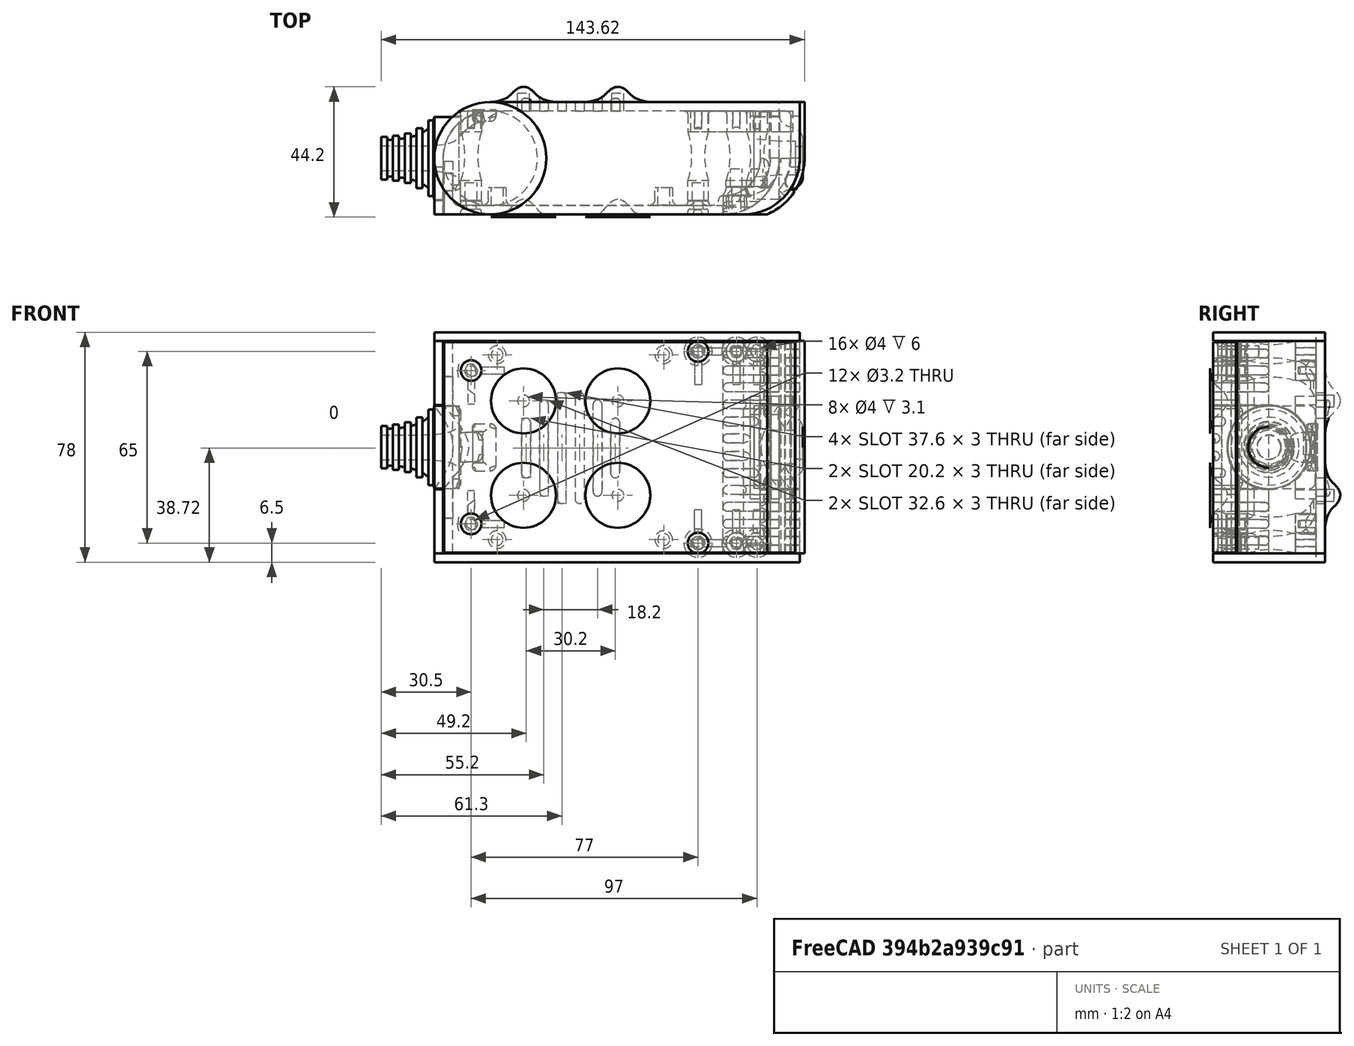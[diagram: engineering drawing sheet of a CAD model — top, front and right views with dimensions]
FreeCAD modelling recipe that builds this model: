
FCSTD DOCUMENT  (FreeCAD 0.19R0.19.2)
Label: enclosure_150
License: All rights reserved
LicenseURL: http://en.wikipedia.org/wiki/All_rights_reserved
objects: Part::Feature×96, Part::Revolution×96, Part::MultiFuse×79, Sketcher::SketchObject×53, Part::Extrusion×41, Part::Cut×39, Part::Fillet×37, Part::Cylinder×36, Part::Box×23, App::MeasureDistance×4
note: 500 computed .brp shape members not serialized (recipe doc carries the construction recipe); baked Part::Feature solids carry a one-line shape summary decoded from their .brp

FEATURE [Sketcher::SketchObject] Sketch  label="topSketch"
  FullyConstrained = true
  sketch-geometry (20):
    g0: LineSegment StartX=5.21097e-06 StartY=3 StartZ=0 EndX=5.21097e-06 EndY=19 EndZ=0
    g1: ArcOfCircle CenterX=19 CenterY=19 CenterZ=0 NormalX=0 NormalY=0 NormalZ=1 AngleXU=0 Radius=19 StartAngle=1.5708 EndAngle=3.14159
    g2: ArcOfCircle CenterX=19 CenterY=19 CenterZ=0 NormalX=0 NormalY=0 NormalZ=1 AngleXU=0 Radius=16 StartAngle=1.5708 EndAngle=3.14159
    g3: LineSegment StartX=114 StartY=35 StartZ=0 EndX=19 EndY=35 EndZ=0
    g4: LineSegment StartX=5.21097e-06 StartY=3 StartZ=0 EndX=5.21097e-06 EndY=0 EndZ=0
    g5: LineSegment StartX=3 StartY=0 StartZ=0 EndX=5.21097e-06 EndY=0 EndZ=0
    g6: LineSegment StartX=3 StartY=19 StartZ=0 EndX=3 EndY=0 EndZ=0
    g7: LineSegment StartX=19 StartY=38 StartZ=0 EndX=124 EndY=38 EndZ=0
    g8: Circle CenterX=119 CenterY=35 CenterZ=0 NormalX=0 NormalY=0 NormalZ=1 AngleXU=0 Radius=1
    g9: Circle CenterX=121 CenterY=35 CenterZ=0 NormalX=0 NormalY=0 NormalZ=1 AngleXU=0 Radius=1
    g10: Circle CenterX=121 CenterY=33 CenterZ=0 NormalX=0 NormalY=0 NormalZ=1 AngleXU=0 Radius=1
    g11: BSplineCurve PolesCount=3 KnotsCount=2 Degree=2 IsPeriodic=0
    g12: GeomPoint X=119 Y=35 Z=0
    g13: GeomPoint X=121 Y=33 Z=0
    g14: LineSegment StartX=119 StartY=35 StartZ=0 EndX=114 EndY=35 EndZ=0
    g15: ArcOfCircle CenterX=105 CenterY=19 CenterZ=0 NormalX=0 NormalY=0 NormalZ=1 AngleXU=0 Radius=19 StartAngle=5.7297 EndAngle=6.28319
    g16: ArcOfCircle CenterX=105 CenterY=19 CenterZ=0 NormalX=0 NormalY=0 NormalZ=1 AngleXU=0 Radius=16 StartAngle=5.60905 EndAngle=6.28319
    g17: LineSegment StartX=121 StartY=33 StartZ=0 EndX=121 EndY=19 EndZ=0
    g18: LineSegment StartX=124 StartY=38 StartZ=0 EndX=124 EndY=19 EndZ=0
    g19: LineSegment StartX=117.5 StartY=9.01251 StartZ=0 EndX=121.163 EndY=9.0125 EndZ=0
  constraints (46):
    c: Vertical(g0)
    c: Block(g0)
    c: Coincident(g1,g0)
    c: Block(g1)
    c: Coincident(g2,g1)
    c: Block(g2)
    c: Coincident(g3,g2)
    c: Horizontal(g3)
    c: Tangent(g3,g2)
    c: Coincident(g4,g0)
    c: Distance(g4) = 3
    c: Vertical(g4)
    c: Coincident(g5,g4)
    c: Horizontal(g5)
    c: Coincident(g6,g2)
    c: Coincident(g6,g5)
    c: Vertical(g6)
    c: Horizontal(g7)
    c: Distance(g7) = 105
    c: Coincident(g7,g1)
    c: Block(g3)
    c: Weight(g8) = 1
    c: Equal(g8,g9)
    c: Equal(g8,g10)
    c: InternalAlignment(g8,g11)
    c: InternalAlignment(g9,g11)
    c: InternalAlignment(g10,g11)
    c: InternalAlignment(g12,g11)
    c: InternalAlignment(g13,g11)
    c: Block(g11)
    c: Coincident(g14,g11)
    c: Coincident(g14,g3)
    c: Horizontal(g14)
    c: Block(g15)
    c: Coincident(g16,g15)
    c: Block(g16)
    c: Coincident(g17,g11)
    c: Coincident(g17,g16)
    c: Vertical(g17)
    c: Distance(g17) = 14
    c: Coincident(g18,g7)
    c: Coincident(g18,g15)
    c: Vertical(g18)
    c: Distance(g18) = 19
    c: Coincident(g19,g16)
    c: Coincident(g19,g15)
FEATURE [Sketcher::SketchObject] Sketch001  label="bottomSketch"
  FullyConstrained = true
  sketch-geometry (32):
    g0: LineSegment StartX=3.3 StartY=-6.03275e-07 StartZ=0 EndX=98 EndY=-6.03275e-07 EndZ=0
    g1: ArcOfCircle CenterX=98 CenterY=19 CenterZ=0 NormalX=0 NormalY=0 NormalZ=1 AngleXU=0 Radius=19 StartAngle=4.71239 EndAngle=5.71103
    g2: LineSegment StartX=6.3 StartY=8 StartZ=0 EndX=3.3 EndY=8 EndZ=0
    g3: LineSegment StartX=3.3 StartY=8 StartZ=0 EndX=3.3 EndY=-6.03275e-07 EndZ=0
    g4: ArcOfCircle CenterX=8.3 CenterY=5 CenterZ=0 NormalX=0 NormalY=0 NormalZ=1 AngleXU=0 Radius=2 StartAngle=3.14159 EndAngle=4.71239
    g5: LineSegment StartX=6.3 StartY=8 StartZ=0 EndX=6.3 EndY=5 EndZ=0
    g6: ArcOfCircle CenterX=98 CenterY=19 CenterZ=0 NormalX=0 NormalY=0 NormalZ=1 AngleXU=0 Radius=12.7 StartAngle=4.71239 EndAngle=6.28319
    g7: LineSegment StartX=94.7 StartY=3 StartZ=0 EndX=8.3 EndY=3 EndZ=0
    g8-g12: Circle x5 (B-spline internal-alignment scaffolding for g13; pole/knot coordinates omitted)
    g13: BSplineCurve PolesCount=5 KnotsCount=3 Degree=3 IsPeriodic=0
    g14: GeomPoint X=98 Y=6.3 Z=0
    g15: GeomPoint X=96.3938 Y=4.71946 Z=0
    g16: GeomPoint X=94.7 Y=3 Z=0
    g17-g23: Circle x7 (B-spline internal-alignment scaffolding for g24; pole/knot coordinates omitted)
    g24: BSplineCurve PolesCount=7 KnotsCount=5 Degree=3 IsPeriodic=0
    g25-g29: GeomPoint x5 (B-spline internal-alignment scaffolding for g24; pole/knot coordinates omitted)
    g30: ArcOfCircle CenterX=98 CenterY=19 CenterZ=0 NormalX=0 NormalY=0 NormalZ=1 AngleXU=0 Radius=15.7 StartAngle=5.81226 EndAngle=6.28319
    g31: LineSegment StartX=110.7 StartY=19 StartZ=0 EndX=113.7 EndY=19 EndZ=0
  constraints (41):
    c: Horizontal(g0)
    c: Coincident(g1,g0)
    c: Block(g1)
    c: Horizontal(g2)
    c: Distance(g2) = 3
    c: Coincident(g3,g2)
    c: Vertical(g3)
    c: Coincident(g3,g0)
    c: Block(g4)
    c: Block(g2)
    c: Coincident(g5,g2)
    c: Coincident(g5,g4)
    c: Vertical(g5)
    c: Coincident(g6,g1)
    c: Block(g6)
    c: Coincident(g7,g4)
    c: Horizontal(g7)
    c: Block(g0)
    c: Block(g7)
    c: Block(g3)
    c: Coincident(g13,g6)
    c: Weight(g8) = 1
    c: Equal(g8, g9-g12) x4
    c: Coincident(g13,g7)
    c: InternalAlignment(g8-g12 -> g13) x5
    c: InternalAlignment(g14,g13)
    c: InternalAlignment(g15,g13)
    c: InternalAlignment(g16,g13)
    c: Block(g13)
    c: Weight(g17) = 1
    c: Equal(g17, g18-g23) x6
    c: Coincident(g24,g1)
    c: InternalAlignment(g17-g23 -> g24) x7
    c: InternalAlignment(g25-g29 -> g24) x5
    c: Block(g24)
    c: Coincident(g30,g24)
    c: Coincident(g31,g6)
    c: Coincident(g31,g30)
    c: Horizontal(g31)
    c: Block(g31)
    c: Block(g30)
FEATURE [Part::Extrusion] Extrude  label="top"
  Base = -> Sketch
  Dir = (0,0,1)
  DirMode = 2
  FaceMakerClass = Part::FaceMakerBullseye
  LengthFwd = 72
  LengthRev = 0
  Solid = true
  Symmetric = false
FEATURE [Part::Extrusion] Extrude001  label="bottom"
  Base = -> Sketch001
  Dir = (0,0,1)
  DirMode = 2
  FaceMakerClass = Part::FaceMakerBullseye
  LengthFwd = 71.4
  LengthRev = 0
  Placement = pos=(0,0,0.3) rot=(0,0,1;0rad)
  Solid = true
  Symmetric = false
FEATURE [Sketcher::SketchObject] Sketch002  label="topSketch001"
  FullyConstrained = true
  sketch-geometry (6):
    g0: ArcOfCircle CenterX=19 CenterY=19 CenterZ=0 NormalX=0 NormalY=0 NormalZ=1 AngleXU=0 Radius=19 StartAngle=1.5708 EndAngle=3.14159
    g1: LineSegment StartX=5.22862e-06 StartY=19 StartZ=0 EndX=5.22862e-06 EndY=1.19904e-11 EndZ=0
    g2: LineSegment StartX=19 StartY=38 StartZ=0 EndX=124 EndY=38 EndZ=0
    g3: LineSegment StartX=5.22862e-06 StartY=1.19904e-11 StartZ=0 EndX=105 EndY=1.19904e-11 EndZ=0
    g4: ArcOfCircle CenterX=105 CenterY=19 CenterZ=0 NormalX=0 NormalY=0 NormalZ=1 AngleXU=0 Radius=19 StartAngle=4.71239 EndAngle=6.28319
    g5: LineSegment StartX=124 StartY=38 StartZ=0 EndX=124 EndY=19 EndZ=0
  constraints (16):
    c: Block(g0)
    c: Coincident(g1,g0)
    c: Vertical(g1)
    c: Horizontal(g2)
    c: Distance(g2) = 105
    c: Coincident(g2,g0)
    c: Distance(g1) = 19
    c: Coincident(g3,g1)
    c: Horizontal(g3)
    c: Distance(g3) = 105
    c: Block(g4)
    c: Coincident(g4,g3)
    c: Coincident(g5,g2)
    c: Coincident(g5,g4)
    c: Vertical(g5)
    c: Distance(g5) = 19
FEATURE [Part::Extrusion] Extrude002  label="sideA"
  Base = -> Sketch002
  Dir = (0,0,1)
  DirMode = 2
  FaceMakerClass = Part::FaceMakerBullseye
  LengthFwd = 3
  LengthRev = 0
  Placement = pos=(0,0,-3) rot=(0,0,1;0rad)
  Solid = true
  Symmetric = false
FEATURE [Sketcher::SketchObject] Sketch003  label="topSketch002"
  FullyConstrained = true
  sketch-geometry (6):
    g0: LineSegment StartX=19 StartY=38 StartZ=0 EndX=117 EndY=38 EndZ=0
    g1: ArcOfCircle CenterX=19 CenterY=19 CenterZ=0 NormalX=0 NormalY=0 NormalZ=1 AngleXU=0 Radius=19 StartAngle=1.5708 EndAngle=3.14159
    g2: LineSegment StartX=117 StartY=38 StartZ=0 EndX=117 EndY=19 EndZ=0
    g3: LineSegment StartX=98 StartY=1.0161e-12 StartZ=0 EndX=5.22862e-06 EndY=1.0161e-12 EndZ=0
    g4: LineSegment StartX=5.22862e-06 StartY=19 StartZ=0 EndX=5.22862e-06 EndY=1.0161e-12 EndZ=0
    g5: ArcOfCircle CenterX=98 CenterY=19 CenterZ=0 NormalX=0 NormalY=0 NormalZ=1 AngleXU=0 Radius=19 StartAngle=4.71239 EndAngle=6.28319
  constraints (16):
    c: Horizontal(g0)
    c: Distance(g0) = 98
    c: Coincident(g1,g0)
    c: Block(g1)
    c: Coincident(g2,g0)
    c: Vertical(g2)
    c: Distance(g2) = 19
    c: Horizontal(g3)
    c: Coincident(g4,g1)
    c: Vertical(g4)
    c: Coincident(g3,g4)
    c: Block(g3)
    c: Coincident(g5,g2)
    c: Coincident(g5,g3)
    c: Block(g0)
    c: Block(g5)
FEATURE [Sketcher::SketchObject] Sketch004
  FullyConstrained = true
  MapMode = 3
  Placement = pos=(0,0,0) rot=(1,0,0;1.5708rad)
  Support = -> [Extrude]
  sketch-geometry (8):
    g0: Circle CenterX=80.351 CenterY=-67.6202 CenterZ=0 NormalX=0 NormalY=0 NormalZ=1 AngleXU=0 Radius=2
    g1: Circle CenterX=80.351 CenterY=-67.6202 CenterZ=0 NormalX=0 NormalY=0 NormalZ=1 AngleXU=0 Radius=3
    g2: Circle CenterX=80.351 CenterY=-4.92017 CenterZ=0 NormalX=0 NormalY=0 NormalZ=1 AngleXU=0 Radius=2
    g3: Circle CenterX=80.351 CenterY=-4.92017 CenterZ=0 NormalX=0 NormalY=0 NormalZ=1 AngleXU=0 Radius=3
    g4: Circle CenterX=23.851 CenterY=-4.92017 CenterZ=0 NormalX=0 NormalY=0 NormalZ=1 AngleXU=0 Radius=2
    g5: Circle CenterX=23.851 CenterY=-4.92017 CenterZ=0 NormalX=0 NormalY=0 NormalZ=1 AngleXU=0 Radius=3
    g6: Circle CenterX=23.851 CenterY=-67.6202 CenterZ=0 NormalX=0 NormalY=0 NormalZ=1 AngleXU=0 Radius=2
    g7: Circle CenterX=23.851 CenterY=-67.6202 CenterZ=0 NormalX=0 NormalY=0 NormalZ=1 AngleXU=0 Radius=3
  constraints (8):
    c: Block(g3)
    c: Block(g2)
    c: Block(g1)
    c: Block(g0)
    c: Block(g6)
    c: Block(g7)
    c: Block(g4)
    c: Block(g5)
FEATURE [Part::Extrusion] Extrude004
  Base = -> Sketch004
  Dir = (0,-1,2e-16)
  DirMode = 2
  FaceMakerClass = Part::FaceMakerBullseye
  LengthFwd = 6
  LengthRev = 0
  Placement = pos=(0,9,0) rot=(0,0,1;0rad)
  Solid = true
  Symmetric = false
FEATURE [Sketcher::SketchObject] Sketch005
  FullyConstrained = true
  MapMode = 3
  Placement = pos=(0,0,0) rot=(1,0,0;1.5708rad)
  Support = -> [Extrude]
  sketch-geometry (8):
    g0: Circle CenterX=80.351 CenterY=-67.6202 CenterZ=0 NormalX=0 NormalY=0 NormalZ=1 AngleXU=0 Radius=3
    g1: Circle CenterX=80.351 CenterY=-4.92017 CenterZ=0 NormalX=0 NormalY=0 NormalZ=1 AngleXU=0 Radius=3
    g2: Circle CenterX=23.851 CenterY=-4.92017 CenterZ=0 NormalX=0 NormalY=0 NormalZ=1 AngleXU=0 Radius=3
    g3: Circle CenterX=23.851 CenterY=-67.6202 CenterZ=0 NormalX=0 NormalY=0 NormalZ=1 AngleXU=0 Radius=3
    g4: Circle CenterX=23.851 CenterY=-67.6202 CenterZ=0 NormalX=0 NormalY=0 NormalZ=1 AngleXU=0 Radius=5
    g5: Circle CenterX=80.351 CenterY=-67.6202 CenterZ=0 NormalX=0 NormalY=0 NormalZ=1 AngleXU=0 Radius=5
    g6: Circle CenterX=23.851 CenterY=-4.92017 CenterZ=0 NormalX=0 NormalY=0 NormalZ=1 AngleXU=0 Radius=5
    g7: Circle CenterX=80.351 CenterY=-4.92017 CenterZ=0 NormalX=0 NormalY=0 NormalZ=1 AngleXU=0 Radius=5
  constraints (8):
    c: Block(g1)
    c: Block(g0)
    c: Block(g3)
    c: Block(g2)
    c: Block(g5)
    c: Block(g4)
    c: Block(g6)
    c: Block(g7)
FEATURE [Part::Extrusion] Extrude005
  Base = -> Sketch005
  Dir = (0,-1,2e-16)
  DirMode = 2
  FaceMakerClass = Part::FaceMakerBullseye
  LengthFwd = 2
  LengthRev = 0
  Solid = true
  Symmetric = false
FEATURE [Sketcher::SketchObject] Sketch006
  FullyConstrained = true
  MapMode = 3
  Placement = pos=(0,0,0) rot=(1,0,0;1.5708rad)
  sketch-geometry (8):
    g0: Circle CenterX=80.351 CenterY=-67.6202 CenterZ=0 NormalX=0 NormalY=0 NormalZ=1 AngleXU=0 Radius=3
    g1: Circle CenterX=80.351 CenterY=-4.92017 CenterZ=0 NormalX=0 NormalY=0 NormalZ=1 AngleXU=0 Radius=3
    g2: Circle CenterX=23.851 CenterY=-4.92017 CenterZ=0 NormalX=0 NormalY=0 NormalZ=1 AngleXU=0 Radius=3
    g3: Circle CenterX=23.851 CenterY=-67.6202 CenterZ=0 NormalX=0 NormalY=0 NormalZ=1 AngleXU=0 Radius=3
    g4: Circle CenterX=23.851 CenterY=-67.6202 CenterZ=0 NormalX=0 NormalY=0 NormalZ=1 AngleXU=0 Radius=5
    g5: Circle CenterX=80.351 CenterY=-67.6202 CenterZ=0 NormalX=0 NormalY=0 NormalZ=1 AngleXU=0 Radius=5
    g6: Circle CenterX=23.851 CenterY=-4.92017 CenterZ=0 NormalX=0 NormalY=0 NormalZ=1 AngleXU=0 Radius=5
    g7: Circle CenterX=80.351 CenterY=-4.92017 CenterZ=0 NormalX=0 NormalY=0 NormalZ=1 AngleXU=0 Radius=5
  constraints (8):
    c: Block(g1)
    c: Block(g0)
    c: Block(g3)
    c: Block(g2)
    c: Block(g5)
    c: Block(g4)
    c: Block(g6)
    c: Block(g7)
FEATURE [Part::Extrusion] Extrude007
  Base = -> Sketch006
  Dir = (0,-1,2e-16)
  DirMode = 2
  FaceMakerClass = Part::FaceMakerBullseye
  LengthFwd = 2
  LengthRev = 0
  Solid = true
  Symmetric = false
FEATURE [Part::Fillet] Fillet
  Base = -> Extrude007
  Edges = 4 edges r=1.99: [Edge6,Edge12,Edge18,Edge24]
FEATURE [Part::Cut] Cut
  Base = -> Extrude005
  Placement = pos=(0,5,0) rot=(0,0,1;0rad)
  Tool = -> Fillet
FEATURE [Part::MultiFuse] Fusion  label="pCBScrews"
  Placement = pos=(-2.5,0,72.3) rot=(0,0,1;0rad)
  Shapes = -> [Extrude004,Cut]
FEATURE [App::MeasureDistance] Distance  label="Distance: 0.69 mm"
  Distance = 0.685967
  P1 = (24.0138,2.9647,0.3)
  P2 = (23.8901,3,-0.373787)
FEATURE [App::MeasureDistance] Distance001  label="Distance: 0.53 mm"
  Distance = 0.533607
  P1 = (80.2939,3,72.2334)
  P2 = (80.281,2.99661,71.7)
FEATURE [Part::Fillet] Fillet001
  Base = -> Extrude001
  Edges = 1 edges r=2.4: [Edge17]
FEATURE [Part::Fillet] Fillet002  label="bottom001"
  Base = -> Fillet001
  Edges = 1 edges r=2.4: [Edge36]
FEATURE [Part::Fillet] Fillet003  label="top001"
  Base = -> Extrude
  Edges = 1 edges r=2: [Edge1]
FEATURE [Sketcher::SketchObject] Sketch007
  FullyConstrained = true
  sketch-geometry (16):
    g0: LineSegment StartX=4 StartY=0 StartZ=0 EndX=4 EndY=2.4 EndZ=0
    g1: LineSegment StartX=4 StartY=2.4 StartZ=0 EndX=7 EndY=2.4 EndZ=0
    g2: LineSegment StartX=4 StartY=0 StartZ=0 EndX=5.7 EndY=0 EndZ=0
    g3: LineSegment StartX=5.7 StartY=0 StartZ=0 EndX=5.7 EndY=-5.6 EndZ=0
    g4-g8: Circle x5 (B-spline internal-alignment scaffolding for g9; pole/knot coordinates omitted)
    g9: BSplineCurve PolesCount=5 KnotsCount=3 Degree=3 IsPeriodic=0
    g10: GeomPoint X=7 Y=2.4 Z=0
    g11: GeomPoint X=10.4582 Y=-1.55472 Z=0
    g12: GeomPoint X=14 Y=-5.6 Z=0
    g13: LineSegment StartX=14 StartY=-5.6 StartZ=0 EndX=14 EndY=-14.1 EndZ=0
    g14: LineSegment StartX=14 StartY=-14.1 StartZ=0 EndX=6.5 EndY=-14.1 EndZ=0
    g15: LineSegment StartX=5.7 StartY=-5.6 StartZ=0 EndX=6.5 EndY=-14.1 EndZ=0
  constraints (28):
    c: Distance(g0) = 2.4
    c: Vertical(g0)
    c: Block(g0)
    c: Coincident(g1,g0)
    c: Horizontal(g1)
    c: Distance(g1) = 3
    c: Coincident(g2,g0)
    c: Horizontal(g2)
    c: Distance(g2) = 1.7
    c: Coincident(g3,g2)
    c: Vertical(g3)
    c: Distance(g3) = 5.6
    c: Coincident(g9,g1)
    c: Weight(g4) = 1
    c: Equal(g4, g5-g8) x4
    c: InternalAlignment(g4-g8 -> g9) x5
    c: InternalAlignment(g10,g9)
    c: InternalAlignment(g11,g9)
    c: InternalAlignment(g12,g9)
    c: Block(g9)
    c: Coincident(g13,g9)
    c: Vertical(g13)
    c: Distance(g13) = 8.5
    c: Coincident(g14,g13)
    c: Horizontal(g14)
    c: Distance(g14) = 7.5
    c: Coincident(g15,g3)
    c: Coincident(g15,g14)
FEATURE [Part::Feature] Face
  shape: bbox 10 x 16.5 x 2e-07 mm, 1 faces, 0 solids (baked)
FEATURE [Part::Revolution] Revolve  label="plugHousing"
  Angle = 360
  Axis = (0,1,0)
  Base = (0,0,0)
  FaceMakerClass = Part::FaceMakerBullseye
  Placement = pos=(0,0,36.15) rot=(0,0,1;0rad)
  Solid = false
  Source = -> Face
  Symmetric = false
FEATURE [Part::Feature] Face001
  shape: bbox 10 x 16.5 x 2e-07 mm, 1 faces, 0 solids (baked)
FEATURE [Part::Revolution] Revolve001  label="plugHousing001"
  Angle = 360
  Axis = (0,1,0)
  Base = (0,0,0)
  FaceMakerClass = Part::FaceMakerBullseye
  Placement = pos=(0,0,36.15) rot=(0,0,1;0rad)
  Solid = false
  Source = -> Face001
  Symmetric = false
FEATURE [Part::MultiFuse] Fusion001  label="plugHousing002"
  Placement = pos=(0,0,0) rot=(0,0,1;1.5708rad)
  Shapes = -> [Revolve001,Revolve]
FEATURE [Part::Feature] Face002
  shape: bbox 10 x 16.5 x 2e-07 mm, 1 faces, 0 solids (baked)
FEATURE [Part::Revolution] Revolve003  label="plugHousing005"
  Angle = 360
  Axis = (0,1,0)
  Base = (0,0,0)
  FaceMakerClass = Part::FaceMakerBullseye
  Placement = pos=(0,0,36.15) rot=(0,0,1;0rad)
  Solid = false
  Source = -> Face002
  Symmetric = false
FEATURE [Part::Feature] Face003
  shape: bbox 10 x 16.5 x 2e-07 mm, 1 faces, 0 solids (baked)
FEATURE [Part::Revolution] Revolve002  label="plugHousing003"
  Angle = 360
  Axis = (0,1,0)
  Base = (0,0,0)
  FaceMakerClass = Part::FaceMakerBullseye
  Placement = pos=(0,0,36.15) rot=(0,0,1;0rad)
  Solid = false
  Source = -> Face003
  Symmetric = false
FEATURE [Part::MultiFuse] Fusion002  label="plugHousing004"
  Placement = pos=(0,0,0) rot=(0,0,1;1.5708rad)
  Shapes = -> [Revolve002,Revolve003]
FEATURE [Part::MultiFuse] Fusion003  label="plugHousing006"
  Placement = pos=(0,19,0) rot=(0,0,1;3.14159rad)
  Shapes = -> [Fusion002,Fusion001]
FEATURE [Part::Feature] Face004
  shape: bbox 10 x 16.5 x 2e-07 mm, 1 faces, 0 solids (baked)
FEATURE [Part::Revolution] Revolve006  label="plugHousing010"
  Angle = 360
  Axis = (0,1,0)
  Base = (0,0,0)
  FaceMakerClass = Part::FaceMakerBullseye
  Placement = pos=(0,0,36.15) rot=(0,0,1;0rad)
  Solid = false
  Source = -> Face004
  Symmetric = false
FEATURE [Part::Feature] Face005
  shape: bbox 10 x 16.5 x 2e-07 mm, 1 faces, 0 solids (baked)
FEATURE [Part::Revolution] Revolve007  label="plugHousing011"
  Angle = 360
  Axis = (0,1,0)
  Base = (0,0,0)
  FaceMakerClass = Part::FaceMakerBullseye
  Placement = pos=(0,0,36.15) rot=(0,0,1;0rad)
  Solid = false
  Source = -> Face005
  Symmetric = false
FEATURE [Part::Feature] Face006
  shape: bbox 10 x 16.5 x 2e-07 mm, 1 faces, 0 solids (baked)
FEATURE [Part::Revolution] Revolve004  label="plugHousing007"
  Angle = 360
  Axis = (0,1,0)
  Base = (0,0,0)
  FaceMakerClass = Part::FaceMakerBullseye
  Placement = pos=(0,0,36.15) rot=(0,0,1;0rad)
  Solid = false
  Source = -> Face006
  Symmetric = false
FEATURE [Part::MultiFuse] Fusion004  label="plugHousing009"
  Placement = pos=(0,0,0) rot=(0,0,1;1.5708rad)
  Shapes = -> [Revolve004,Revolve007]
FEATURE [Part::Feature] Face007
  shape: bbox 10 x 16.5 x 2e-07 mm, 1 faces, 0 solids (baked)
FEATURE [Part::Revolution] Revolve005  label="plugHousing008"
  Angle = 360
  Axis = (0,1,0)
  Base = (0,0,0)
  FaceMakerClass = Part::FaceMakerBullseye
  Placement = pos=(0,0,36.15) rot=(0,0,1;0rad)
  Solid = false
  Source = -> Face007
  Symmetric = false
FEATURE [Part::MultiFuse] Fusion005  label="plugHousing012"
  Placement = pos=(0,0,0) rot=(0,0,1;1.5708rad)
  Shapes = -> [Revolve006,Revolve005]
FEATURE [Part::MultiFuse] Fusion006  label="plugHousing013"
  Placement = pos=(0,19,0) rot=(0,0,1;3.14159rad)
  Shapes = -> [Fusion005,Fusion004]
FEATURE [Part::MultiFuse] Fusion007  label="plugHousing014"
  Placement = pos=(122.621,0,-0.15) rot=(0,0,1;0rad)
  Shapes = -> [Fusion003,Fusion006]
FEATURE [Part::Cylinder] Cylinder002
  Angle = 360
  AttacherType = Attacher::AttachEngine3D
  Height = 20
  Placement = pos=(0,0,36.15) rot=(0,0,1;0rad)
  Radius = 4
FEATURE [Part::Cylinder] Cylinder003
  Angle = 360
  AttacherType = Attacher::AttachEngine3D
  Height = 10
  Placement = pos=(0,0,36.15) rot=(0,0,1;0rad)
  Radius = 4
FEATURE [Part::MultiFuse] Fusion009  label="removeToCreateHoleForPlugHousing"
  Placement = pos=(70,19,36.15) rot=(0,1,0;1.5708rad)
  Shapes = -> [Cylinder002,Cylinder003]
FEATURE [Part::Cylinder] Cylinder004
  Angle = 360
  AttacherType = Attacher::AttachEngine3D
  Height = 20
  Placement = pos=(0,0,36.15) rot=(0,0,1;0rad)
  Radius = 4
FEATURE [Part::Cylinder] Cylinder005
  Angle = 360
  AttacherType = Attacher::AttachEngine3D
  Height = 10
  Placement = pos=(0,0,36.15) rot=(0,0,1;0rad)
  Radius = 4
FEATURE [Part::MultiFuse] Fusion010  label="removeToCreateHoleForPlugHousing001"
  Placement = pos=(70,19,36.15) rot=(0,1,0;1.5708rad)
  Shapes = -> [Cylinder004,Cylinder005]
FEATURE [Part::Cut] Cut001
  Base = -> Fillet003
  Tool = -> Fusion010
FEATURE [Part::Cut] Cut002  label="Bottom"
  Base = -> Fillet002
  Tool = -> Fusion009
FEATURE [Part::Feature] Face008
  shape: bbox 10 x 16.5 x 2e-07 mm, 1 faces, 0 solids (baked)
FEATURE [Part::Revolution] Revolve011  label="plugHousing021"
  Angle = 360
  Axis = (0,1,0)
  Base = (0,0,0)
  FaceMakerClass = Part::FaceMakerBullseye
  Placement = pos=(0,0,36.15) rot=(0,0,1;0rad)
  Solid = false
  Source = -> Face008
  Symmetric = false
FEATURE [Part::Feature] Face009
  shape: bbox 10 x 16.5 x 2e-07 mm, 1 faces, 0 solids (baked)
FEATURE [Part::Revolution] Revolve012  label="plugHousing022"
  Angle = 360
  Axis = (0,1,0)
  Base = (0,0,0)
  FaceMakerClass = Part::FaceMakerBullseye
  Placement = pos=(0,0,36.15) rot=(0,0,1;0rad)
  Solid = false
  Source = -> Face009
  Symmetric = false
FEATURE [Part::Feature] Face010 .. Face013  x4 (patterned run collapsed; names and placements below)
  shape: bbox 10 x 16.5 x 2e-07 mm, 1 faces, 0 solids (baked)
FEATURE [Part::Revolution] Revolve015  label="plugHousing027"
  Angle = 360
  Axis = (0,1,0)
  Base = (0,0,0)
  FaceMakerClass = Part::FaceMakerBullseye
  Placement = pos=(0,0,36.15) rot=(0,0,1;0rad)
  Solid = false
  Source = -> Face013
  Symmetric = false
FEATURE [Part::Feature] Face014
  shape: bbox 10 x 16.5 x 2e-07 mm, 1 faces, 0 solids (baked)
FEATURE [Part::Feature] Face015
  shape: bbox 10 x 16.5 x 2e-07 mm, 1 faces, 0 solids (baked)
FEATURE [Part::Feature] Face016
  shape: bbox 10 x 16.5 x 2e-07 mm, 1 faces, 0 solids (baked)
FEATURE [Part::Revolution] Revolve019  label="plugHousing033"
  Angle = 360
  Axis = (0,1,0)
  Base = (0,0,0)
  FaceMakerClass = Part::FaceMakerBullseye
  Placement = pos=(0,0,36.15) rot=(0,0,1;0rad)
  Solid = false
  Source = -> Face016
  Symmetric = false
FEATURE [Part::Feature] Face017
  shape: bbox 10 x 16.5 x 2e-07 mm, 1 faces, 0 solids (baked)
FEATURE [Part::Revolution] Revolve020  label="plugHousing034"
  Angle = 360
  Axis = (0,1,0)
  Base = (0,0,0)
  FaceMakerClass = Part::FaceMakerBullseye
  Placement = pos=(0,0,36.15) rot=(0,0,1;0rad)
  Solid = false
  Source = -> Face017
  Symmetric = false
FEATURE [Part::Feature] Face018
  shape: bbox 10 x 16.5 x 2e-07 mm, 1 faces, 0 solids (baked)
FEATURE [Part::Revolution] Revolve016  label="plugHousing030"
  Angle = 360
  Axis = (0,1,0)
  Base = (0,0,0)
  FaceMakerClass = Part::FaceMakerBullseye
  Placement = pos=(0,0,36.15) rot=(0,0,1;0rad)
  Solid = false
  Source = -> Face018
  Symmetric = false
FEATURE [Part::MultiFuse] Fusion020  label="plugHousing038"
  Placement = pos=(0,0,0) rot=(0,0,1;1.5708rad)
  Shapes = -> [Revolve016,Revolve020]
FEATURE [Part::Feature] Face019
  shape: bbox 10 x 16.5 x 2e-07 mm, 1 faces, 0 solids (baked)
FEATURE [Part::Feature] Face020
  shape: bbox 10 x 16.5 x 2e-07 mm, 1 faces, 0 solids (baked)
FEATURE [Part::Revolution] Revolve017  label="plugHousing031"
  Angle = 360
  Axis = (0,1,0)
  Base = (0,0,0)
  FaceMakerClass = Part::FaceMakerBullseye
  Placement = pos=(0,0,36.15) rot=(0,0,1;0rad)
  Solid = false
  Source = -> Face020
  Symmetric = false
FEATURE [Part::MultiFuse] Fusion021  label="plugHousing039"
  Placement = pos=(0,0,0) rot=(0,0,1;1.5708rad)
  Shapes = -> [Revolve019,Revolve017]
FEATURE [Part::MultiFuse] Fusion023  label="plugHousing041"
  Placement = pos=(0,19,0) rot=(0,0,1;3.14159rad)
  Shapes = -> [Fusion021,Fusion020]
FEATURE [Part::Revolution] Revolve022  label="plugHousing043"
  Angle = 360
  Axis = (0,1,0)
  Base = (0,0,0)
  FaceMakerClass = Part::FaceMakerBullseye
  Placement = pos=(0,0,36.15) rot=(0,0,1;0rad)
  Solid = false
  Source = -> Face019
  Symmetric = false
FEATURE [Part::Feature] Face021
  shape: bbox 10 x 16.5 x 2e-07 mm, 1 faces, 0 solids (baked)
FEATURE [Part::Revolution] Revolve023  label="plugHousing044"
  Angle = 360
  Axis = (0,1,0)
  Base = (0,0,0)
  FaceMakerClass = Part::FaceMakerBullseye
  Placement = pos=(0,0,36.15) rot=(0,0,1;0rad)
  Solid = false
  Source = -> Face021
  Symmetric = false
FEATURE [Part::Feature] Face022
  shape: bbox 10 x 16.5 x 2e-07 mm, 1 faces, 0 solids (baked)
FEATURE [Part::Revolution] Revolve018  label="plugHousing032"
  Angle = 360
  Axis = (0,1,0)
  Base = (0,0,0)
  FaceMakerClass = Part::FaceMakerBullseye
  Placement = pos=(0,0,36.15) rot=(0,0,1;0rad)
  Solid = false
  Source = -> Face022
  Symmetric = false
FEATURE [Part::MultiFuse] Fusion022  label="plugHousing040"
  Placement = pos=(0,0,0) rot=(0,0,1;1.5708rad)
  Shapes = -> [Revolve018,Revolve023]
FEATURE [Part::Feature] Face023
  shape: bbox 10 x 16.5 x 2e-07 mm, 1 faces, 0 solids (baked)
FEATURE [Part::Revolution] Revolve021  label="plugHousing035"
  Angle = 360
  Axis = (0,1,0)
  Base = (0,0,0)
  FaceMakerClass = Part::FaceMakerBullseye
  Placement = pos=(0,0,36.15) rot=(0,0,1;0rad)
  Solid = false
  Source = -> Face023
  Symmetric = false
FEATURE [Part::MultiFuse] Fusion018  label="plugHousing036"
  Placement = pos=(0,0,0) rot=(0,0,1;1.5708rad)
  Shapes = -> [Revolve022,Revolve021]
FEATURE [Part::MultiFuse] Fusion019  label="plugHousing037"
  Placement = pos=(0,19,0) rot=(0,0,1;3.14159rad)
  Shapes = -> [Fusion018,Fusion022]
FEATURE [Part::MultiFuse] Fusion024  label="plugHousing042"
  Placement = pos=(122.621,0,-0.15) rot=(0,0,1;0rad)
  Shapes = -> [Fusion023,Fusion019]
FEATURE [Part::Cylinder] Cylinder006
  Angle = 360
  AttacherType = Attacher::AttachEngine3D
  Height = 20
  Placement = pos=(0,0,36.15) rot=(0,0,1;0rad)
  Radius = 14.3
FEATURE [Part::Cylinder] Cylinder007
  Angle = 360
  AttacherType = Attacher::AttachEngine3D
  Height = 10
  Placement = pos=(0,0,36.15) rot=(0,0,1;0rad)
  Radius = 4
FEATURE [Part::MultiFuse] Fusion026  label="removeToCreteHoleForPlugHousing"
  Placement = pos=(70,19,36) rot=(0,1,0;1.5708rad)
  Shapes = -> [Cylinder006,Cylinder007]
FEATURE [Part::Box] Box001  label="Cube001"
  AttacherType = Attacher::AttachEngine3D
  Height = 28
  Length = 3
  Placement = pos=(110.7,19,22) rot=(0,0,1;0rad)
  Width = 15.7
FEATURE [Part::Cut] Cut003  label="top002"
  Base = -> Cut001
  Tool = -> Fusion007
FEATURE [Part::Revolution] Revolve008  label="plugHousing015"
  Angle = 360
  Axis = (0,1,0)
  Base = (0,0,0)
  FaceMakerClass = Part::FaceMakerBullseye
  Placement = pos=(0,0,36.15) rot=(0,0,1;0rad)
  Solid = false
  Source = -> Face010
  Symmetric = false
FEATURE [Part::MultiFuse] Fusion013  label="plugHousing020"
  Placement = pos=(0,0,0) rot=(0,0,1;1.5708rad)
  Shapes = -> [Revolve008,Revolve012]
FEATURE [Part::Cut] Cut004  label="top003"
  Base = -> Cut003
  Placement = pos=(1,0,0) rot=(0,0,1;0rad)
  Tool = -> Fusion026
FEATURE [Part::Cylinder] Cylinder008
  Angle = 360
  AttacherType = Attacher::AttachEngine3D
  Height = 20
  Placement = pos=(0,0,36.15) rot=(0,0,1;0rad)
  Radius = 10.3
FEATURE [Part::Cylinder] Cylinder009
  Angle = 360
  AttacherType = Attacher::AttachEngine3D
  Height = 10
  Placement = pos=(0,0,36.15) rot=(0,0,1;0rad)
  Radius = 4
FEATURE [Part::MultiFuse] Fusion027  label="removeToCreteHoleForPlugHousing001"
  Placement = pos=(70,19,36) rot=(0,1,0;1.5708rad)
  Shapes = -> [Cylinder008,Cylinder009]
FEATURE [Part::Cut] Cut005  label="plugHousingTab"
  Base = -> Box001
  Tool = -> Fusion027
FEATURE [Part::MultiFuse] Fusion028  label="plugHousing045"
  Shapes = -> [Fusion024,Cut005]
FEATURE [Part::Box] Box002  label="Cube002"
  AttacherType = Attacher::AttachEngine3D
  Height = 28.8
  Length = 3
  Placement = pos=(107.3,28,21.6) rot=(0,0,1;0rad)
  Width = 7
FEATURE [Part::Box] Box003  label="Cube003"
  AttacherType = Attacher::AttachEngine3D
  Height = 3
  Length = 6.4
  Placement = pos=(107.3,28,18.6) rot=(0,0,1;0rad)
  Width = 7
FEATURE [Part::Box] Box004  label="Cube004"
  AttacherType = Attacher::AttachEngine3D
  Height = 3
  Length = 6.4
  Placement = pos=(107.3,28,50.4) rot=(0,0,1;0rad)
  Width = 7
FEATURE [Part::MultiFuse] Fusion029  label="plugHousingBracketHolder"
  Shapes = -> [Box004,Box002,Box003]
FEATURE [Part::Cylinder] Cylinder010
  Angle = 360
  AttacherType = Attacher::AttachEngine3D
  Height = 20
  Placement = pos=(0,0,36.15) rot=(0,0,1;0rad)
  Radius = 14.3
FEATURE [Part::Cylinder] Cylinder011
  Angle = 360
  AttacherType = Attacher::AttachEngine3D
  Height = 10
  Placement = pos=(0,0,36.15) rot=(0,0,1;0rad)
  Radius = 4
FEATURE [Part::MultiFuse] Fusion030  label="removeToCreteHoleForPlugHousing002"
  Placement = pos=(70,19,36) rot=(0,1,0;1.5708rad)
  Shapes = -> [Cylinder010,Cylinder011]
FEATURE [Part::Cut] Cut006  label="plugHousingBracketHolder001"
  Base = -> Fusion029
  Tool = -> Fusion030
FEATURE [Part::Cylinder] Cylinder012
  Angle = 360
  AttacherType = Attacher::AttachEngine3D
  Height = 20
  Placement = pos=(0,0,36.15) rot=(0,0,1;0rad)
  Radius = 7
FEATURE [Part::Cylinder] Cylinder013
  Angle = 360
  AttacherType = Attacher::AttachEngine3D
  Height = 10
  Placement = pos=(0,0,36.15) rot=(0,0,1;0rad)
  Radius = 4
FEATURE [Part::MultiFuse] Fusion032  label="removeToCreteHoleForPlugHousing003"
  Placement = pos=(70,19,36) rot=(0,1,0;1.5708rad)
  Shapes = -> [Cylinder012,Cylinder013]
FEATURE [Part::Cut] Cut007  label="bottom002"
  Base = -> Cut002
  Tool = -> Fusion032
FEATURE [Sketcher::SketchObject] Sketch008
  FullyConstrained = true
  sketch-geometry (54):
    g0: LineSegment StartX=-4.2 StartY=0 StartZ=0 EndX=-6.2 EndY=0 EndZ=0
    g1: LineSegment StartX=-14 StartY=-18 StartZ=0 EndX=-14 EndY=-26.5 EndZ=0
    g2: LineSegment StartX=-4.2 StartY=0 StartZ=0 EndX=-4.2 EndY=-13.4877 EndZ=0
    g3: Circle CenterX=-4.2 CenterY=-13.4877 CenterZ=0 NormalX=0 NormalY=0 NormalZ=1 AngleXU=0 Radius=1
    g4: Circle CenterX=-4.2 CenterY=-26.5 CenterZ=0 NormalX=0 NormalY=0 NormalZ=1 AngleXU=0 Radius=1
    g5: Circle CenterX=-8.2 CenterY=-26.5 CenterZ=0 NormalX=0 NormalY=0 NormalZ=1 AngleXU=0 Radius=1
    g6: BSplineCurve PolesCount=3 KnotsCount=2 Degree=2 IsPeriodic=0
    g7: GeomPoint X=-4.2 Y=-13.4877 Z=0
    g8: GeomPoint X=-8.2 Y=-26.5 Z=0
    g9: LineSegment StartX=-14 StartY=-26.5 StartZ=0 EndX=-8.2 EndY=-26.5 EndZ=0
    g10: LineSegment StartX=-10.15 StartY=-12 StartZ=0 EndX=-10.15 EndY=-14 EndZ=0
    g11: LineSegment StartX=-12.8401 StartY=-16 StartZ=0 EndX=-10.1571 EndY=-16 EndZ=0
    g12: LineSegment StartX=-10.15 StartY=-14 StartZ=0 EndX=-8.70761 EndY=-14 EndZ=0
    g13: LineSegment StartX=-12.8401 StartY=-16 StartZ=0 EndX=-12.8401 EndY=-17.6958 EndZ=0
    g14: LineSegment StartX=-10.15 StartY=-12 StartZ=0 EndX=-7.79258 EndY=-12 EndZ=0
    g15: Circle CenterX=-6.2215 CenterY=-2 CenterZ=0 NormalX=0 NormalY=0 NormalZ=1 AngleXU=0 Radius=1
    g16: Circle CenterX=-6.22762 CenterY=-2.58724 CenterZ=0 NormalX=0 NormalY=0 NormalZ=1 AngleXU=0 Radius=1
    g17: Circle CenterX=-6.32538 CenterY=-4 CenterZ=0 NormalX=0 NormalY=0 NormalZ=1 AngleXU=0 Radius=1
    g18: BSplineCurve PolesCount=3 KnotsCount=2 Degree=2 IsPeriodic=0
    g19: GeomPoint X=-6.2215 Y=-2 Z=0
    g20: GeomPoint X=-6.32538 Y=-4 Z=0
    g21: Circle CenterX=-6.48644 CenterY=-5.99526 CenterZ=0 NormalX=0 NormalY=0 NormalZ=1 AngleXU=0 Radius=1
    g22: Circle CenterX=-6.58486 CenterY=-6.99526 CenterZ=0 NormalX=0 NormalY=0 NormalZ=1 AngleXU=0 Radius=1
    g23: Circle CenterX=-6.77343 CenterY=-8 CenterZ=0 NormalX=0 NormalY=0 NormalZ=1 AngleXU=0 Radius=1
    g24: BSplineCurve PolesCount=3 KnotsCount=2 Degree=2 IsPeriodic=0
    g25: GeomPoint X=-6.48644 Y=-5.99526 Z=0
    g26: GeomPoint X=-6.77343 Y=-8 Z=0
    g27: Circle CenterX=-7.19003 CenterY=-10 CenterZ=0 NormalX=0 NormalY=0 NormalZ=1 AngleXU=0 Radius=1
    g28: Circle CenterX=-7.44407 CenterY=-11.0915 CenterZ=0 NormalX=0 NormalY=0 NormalZ=1 AngleXU=0 Radius=1
    g29: Circle CenterX=-7.79258 CenterY=-12 CenterZ=0 NormalX=0 NormalY=0 NormalZ=1 AngleXU=0 Radius=1
    g30: BSplineCurve PolesCount=3 KnotsCount=2 Degree=2 IsPeriodic=0
    g31: GeomPoint X=-7.19003 Y=-10 Z=0
    g32: GeomPoint X=-7.79258 Y=-12 Z=0
    g33: Circle CenterX=-8.70761 CenterY=-14 CenterZ=0 NormalX=0 NormalY=0 NormalZ=1 AngleXU=0 Radius=1
    g34: Circle CenterX=-9.33087 CenterY=-15.1837 CenterZ=0 NormalX=0 NormalY=0 NormalZ=1 AngleXU=0 Radius=1
    g35: Circle CenterX=-10.1571 CenterY=-16 CenterZ=0 NormalX=0 NormalY=0 NormalZ=1 AngleXU=0 Radius=1
    g36: BSplineCurve PolesCount=3 KnotsCount=2 Degree=2 IsPeriodic=0
    g37: GeomPoint X=-8.70761 Y=-14 Z=0
    g38: GeomPoint X=-10.1571 Y=-16 Z=0
    g39: Circle CenterX=-12.8401 CenterY=-17.6958 CenterZ=0 NormalX=0 NormalY=0 NormalZ=1 AngleXU=0 Radius=1
    g40: Circle CenterX=-13.3521 CenterY=-17.9027 CenterZ=0 NormalX=0 NormalY=0 NormalZ=1 AngleXU=0 Radius=1
    g41: Circle CenterX=-14 CenterY=-18 CenterZ=0 NormalX=0 NormalY=0 NormalZ=1 AngleXU=0 Radius=1
    g42: BSplineCurve PolesCount=3 KnotsCount=2 Degree=2 IsPeriodic=0
    g43: GeomPoint X=-12.8401 Y=-17.6958 Z=0
    g44: GeomPoint X=-14 Y=-18 Z=0
    g45: LineSegment StartX=-6.2 StartY=0 StartZ=0 EndX=-7.2 EndY=0 EndZ=0
    g46: LineSegment StartX=-7.2 StartY=0 StartZ=0 EndX=-7.2 EndY=-2 EndZ=0
    g47: LineSegment StartX=-7.2 StartY=-2 StartZ=0 EndX=-6.2215 EndY=-2 EndZ=0
    g48: LineSegment StartX=-6.32538 StartY=-4 StartZ=0 EndX=-7.65538 EndY=-4 EndZ=0
    g49: LineSegment StartX=-7.65538 StartY=-4 StartZ=0 EndX=-7.65538 EndY=-5.99526 EndZ=0
    g50: LineSegment StartX=-7.65538 StartY=-5.99526 StartZ=0 EndX=-6.48644 EndY=-5.99526 EndZ=0
    g51: LineSegment StartX=-6.77343 StartY=-8 StartZ=0 EndX=-8.43343 EndY=-8 EndZ=0
    g52: LineSegment StartX=-8.43343 StartY=-8 StartZ=0 EndX=-8.43343 EndY=-10 EndZ=0
    g53: LineSegment StartX=-8.43343 StartY=-10 StartZ=0 EndX=-7.19003 EndY=-10 EndZ=0
  constraints (112):
    c: Horizontal(g0)
    c: Distance(g0) = 2
    c: Block(g0)
    c: Vertical(g1)
    c: Coincident(g2,g0)
    c: Vertical(g2)
    c: Block(g2)
    c: Coincident(g6,g2)
    c: Weight(g3) = 1
    c: Equal(g3,g4)
    c: Equal(g3,g5)
    c: InternalAlignment(g3,g6)
    c: InternalAlignment(g4,g6)
    c: InternalAlignment(g5,g6)
    c: InternalAlignment(g7,g6)
    c: InternalAlignment(g8,g6)
    c: Block(g6)
    c: Coincident(g9,g1)
    c: Coincident(g9,g6)
    c: Horizontal(g9)
    c: Vertical(g10)
    c: Block(g10)
    c: Horizontal(g11)
    c: Block(g11)
    c: Coincident(g12,g10)
    c: Horizontal(g12)
    c: Block(g12)
    c: Coincident(g13,g11)
    c: Vertical(g13)
    c: Block(g13)
    c: Coincident(g14,g10)
    c: Horizontal(g14)
    c: Block(g14)
    c: Block(g9)
    c: Block(g1)
    c: Weight(g15) = 1
    c: Equal(g15,g16)
    c: Equal(g15,g17)
    c: InternalAlignment(g15,g18)
    c: InternalAlignment(g16,g18)
    c: InternalAlignment(g17,g18)
    c: InternalAlignment(g19,g18)
    c: InternalAlignment(g20,g18)
    c: Weight(g21) = 1
    c: Equal(g21,g22)
    c: Equal(g21,g23)
    c: InternalAlignment(g21,g24)
    c: InternalAlignment(g22,g24)
    c: InternalAlignment(g23,g24)
    c: InternalAlignment(g25,g24)
    c: InternalAlignment(g26,g24)
    c: Weight(g27) = 1
    c: Equal(g27,g28)
    c: Equal(g27,g29)
    c: Coincident(g30,g14)
    c: InternalAlignment(g27,g30)
    c: InternalAlignment(g28,g30)
    c: InternalAlignment(g29,g30)
    c: InternalAlignment(g31,g30)
    c: InternalAlignment(g32,g30)
    c: Coincident(g36,g12)
    c: Weight(g33) = 1
    c: Equal(g33,g34)
    c: Equal(g33,g35)
    c: Coincident(g36,g11)
    c: InternalAlignment(g33,g36)
    c: InternalAlignment(g34,g36)
    c: InternalAlignment(g35,g36)
    c: InternalAlignment(g37,g36)
    c: InternalAlignment(g38,g36)
    c: Coincident(g42,g13)
    c: Weight(g39) = 1
    c: Equal(g39,g40)
    c: Equal(g39,g41)
    c: Coincident(g42,g1)
    c: InternalAlignment(g39,g42)
    c: InternalAlignment(g40,g42)
    c: InternalAlignment(g41,g42)
    c: InternalAlignment(g43,g42)
    c: InternalAlignment(g44,g42)
    c: Block(g18)
    c: Block(g24)
    c: Block(g30)
    c: Block(g36)
    c: Block(g42)
    c: Horizontal(g45)
    c: Coincident(g45,g0)
    c: Vertical(g46)
    c: Coincident(g46,g45)
    c: Coincident(g47,g46)
    c: Coincident(g47,g18)
    c: Horizontal(g47)
    c: Block(g46)
    c: Coincident(g48,g18)
    c: Horizontal(g48)
    c: Distance(g48) = 1.33
    c: Vertical(g49)
    c: Coincident(g49,g48)
    c: Coincident(g50,g49)
    c: Coincident(g50,g24)
    c: Horizontal(g50)
    c: Tangent(g50,g22)
    c: Horizontal(g51)
    c: Coincident(g51,g24)
    c: Block(g51)
    c: Vertical(g52)
    c: Block(g52)
    c: Coincident(g52,g51)
    c: Coincident(g53,g52)
    c: Coincident(g53,g30)
    c: Horizontal(g53)
    c: Distance(g1) = 8.5
FEATURE [Part::Feature] Face024
  shape: bbox 9.8 x 26.5 x 2e-07 mm, 1 faces, 0 solids (baked)
FEATURE [Part::Revolution] Revolve024
  Angle = 360
  Axis = (0,1,0)
  Base = (0,0,0)
  FaceMakerClass = Part::FaceMakerBullseye
  Placement = pos=(0,0,0) rot=(0,0,1;1.5708rad)
  Solid = false
  Source = -> Face024
  Symmetric = false
FEATURE [Part::Feature] Face025
  shape: bbox 9.8 x 26.5 x 2e-07 mm, 1 faces, 0 solids (baked)
FEATURE [Part::Revolution] Revolve025
  Angle = 360
  Axis = (0,1,0)
  Base = (0,0,0)
  FaceMakerClass = Part::FaceMakerBullseye
  Placement = pos=(0,0,0) rot=(0,0,1;1.5708rad)
  Solid = false
  Source = -> Face025
  Symmetric = false
FEATURE [Part::MultiFuse] Fusion033
  Placement = pos=(-18,19,36) rot=(0,0,1;0rad)
  Shapes = -> [Revolve025,Revolve024]
FEATURE [Part::Cylinder] Cylinder014
  Angle = 360
  AttacherType = Attacher::AttachEngine3D
  Height = 20
  Placement = pos=(0,0,36.15) rot=(0,0,1;0rad)
  Radius = 14.3
FEATURE [Part::Cylinder] Cylinder015
  Angle = 360
  AttacherType = Attacher::AttachEngine3D
  Height = 10
  Placement = pos=(0,0,36.15) rot=(0,0,1;0rad)
  Radius = 4
FEATURE [Part::MultiFuse] Fusion034  label="removeToCreteHoleForPlugHousing004"
  Placement = pos=(-42,19,36) rot=(0,1,0;1.5708rad)
  Shapes = -> [Cylinder014,Cylinder015]
FEATURE [Part::Cut] Cut008  label="top004"
  Base = -> Cut004
  Placement = pos=(-1,0,0) rot=(0,0,1;0rad)
  Tool = -> Fusion034
FEATURE [Part::Box] Box005  label="Cube005"
  AttacherType = Attacher::AttachEngine3D
  Height = 28
  Length = 3
  Placement = pos=(110.7,19,22) rot=(0,0,1;0rad)
  Width = 15.7
FEATURE [Part::Cylinder] Cylinder016
  Angle = 360
  AttacherType = Attacher::AttachEngine3D
  Height = 10
  Placement = pos=(0,0,36.15) rot=(0,0,1;0rad)
  Radius = 4
FEATURE [Part::Cylinder] Cylinder017
  Angle = 360
  AttacherType = Attacher::AttachEngine3D
  Height = 20
  Placement = pos=(0,0,36.15) rot=(0,0,1;0rad)
  Radius = 10.3
FEATURE [Part::MultiFuse] Fusion035  label="removeToCreteHoleForPlugHousing005"
  Placement = pos=(70,19,36) rot=(0,1,0;1.5708rad)
  Shapes = -> [Cylinder017,Cylinder016]
FEATURE [Part::Cut] Cut009  label="plugHousingTab001"
  Base = -> Box005
  Placement = pos=(-107.4,-14,0) rot=(0,0,1;0rad)
  Tool = -> Fusion035
FEATURE [Part::Box] Box006  label="Cube006"
  AttacherType = Attacher::AttachEngine3D
  Height = 28
  Length = 3
  Placement = pos=(110.7,19,22) rot=(0,0,1;0rad)
  Width = 15.7
FEATURE [Part::Cylinder] Cylinder018
  Angle = 360
  AttacherType = Attacher::AttachEngine3D
  Height = 10
  Placement = pos=(0,0,36.15) rot=(0,0,1;0rad)
  Radius = 4
FEATURE [Part::Cylinder] Cylinder019
  Angle = 360
  AttacherType = Attacher::AttachEngine3D
  Height = 20
  Placement = pos=(0,0,36.15) rot=(0,0,1;0rad)
  Radius = 10.3
FEATURE [Part::MultiFuse] Fusion036  label="removeToCreteHoleForPlugHousing006"
  Placement = pos=(70,19,36) rot=(0,1,0;1.5708rad)
  Shapes = -> [Cylinder019,Cylinder018]
FEATURE [Part::Cut] Cut010  label="plugHousingTab002"
  Base = -> Box006
  Placement = pos=(-107.4,-14,0) rot=(0,0,1;0rad)
  Tool = -> Fusion036
FEATURE [Part::MultiFuse] Fusion037
  Placement = pos=(9.6,23,0) rot=(0,0,1;3.14159rad)
  Shapes = -> [Cut009,Cut010]
FEATURE [Part::Box] Box  label="Cube"
  AttacherType = Attacher::AttachEngine3D
  Height = 10
  Length = 3
  Placement = pos=(3.3,4,12) rot=(0,0,1;0rad)
  Width = 10
FEATURE [Part::Fillet] Fillet004
  Base = -> Fusion028
  Edges = 1 edges r=2: [Edge25]
FEATURE [Part::Fillet] Fillet005  label="plugHousing046"
  Base = -> Fillet004
  Edges = 1 edges r=2: [Edge8]
FEATURE [Part::Fillet] Fillet006
  Base = -> Box
  Edges = 1 edges r=2: [Edge11]
FEATURE [Part::Box] Box007  label="Cube007"
  AttacherType = Attacher::AttachEngine3D
  Height = 10
  Length = 3
  Placement = pos=(3.3,4,50) rot=(0,0,1;0rad)
  Width = 10
FEATURE [Part::Fillet] Fillet007
  Base = -> Box007
  Edges = 1 edges r=2: [Edge12]
FEATURE [Part::Box] Box008  label="Cube008"
  AttacherType = Attacher::AttachEngine3D
  Height = 28
  Length = 4
  Placement = pos=(5,0,22) rot=(0,0,1;0rad)
  Width = 10
FEATURE [Part::Fillet] Fillet008
  Base = -> Box008
  Edges = 1 edges r=1: [Edge7]
FEATURE [Part::Fillet] Fillet009
  Base = -> Fillet008
  Edges = 1 edges r=2: [Edge5]
FEATURE [Part::Fillet] Fillet010
  Base = -> Fillet009
  Edges = 1 edges r=2: [Edge2]
FEATURE [Sketcher::SketchObject] Sketch009  label="topSketch003"
  FullyConstrained = true
  sketch-geometry (4):
    g0: LineSegment StartX=16.8446 StartY=31.512 StartZ=0 EndX=16.3251 EndY=34.4666 EndZ=0
    g1: ArcOfCircle CenterX=19 CenterY=19.2524 CenterZ=0 NormalX=0 NormalY=0 NormalZ=1 AngleXU=0 Radius=15.4476 StartAngle=1.74483 EndAngle=2.72717
    g2: ArcOfCircle CenterX=19 CenterY=19.2524 CenterZ=0 NormalX=0 NormalY=0 NormalZ=1 AngleXU=0 Radius=12.4476 StartAngle=1.74483 EndAngle=2.73189
    g3: LineSegment StartX=4.86004 StartY=25.4725 StartZ=0 EndX=7.58253 EndY=24.2107 EndZ=0
  constraints (7):
    c: Block(g0)
    c: Coincident(g1,g0)
    c: Coincident(g2,g0)
    c: Coincident(g3,g1)
    c: Coincident(g3,g2)
    c: Block(g1)
    c: Block(g2)
FEATURE [Part::Extrusion] Extrude008
  Base = -> Sketch009
  Dir = (0,0,1)
  DirMode = 2
  FaceMakerClass = Part::FaceMakerBullseye
  LengthFwd = 10
  LengthRev = 0
  Placement = pos=(0,0,31) rot=(0,0,1;0rad)
  Solid = true
  Symmetric = false
FEATURE [Part::Cylinder] Cylinder020
  Angle = 360
  AttacherType = Attacher::AttachEngine3D
  Height = 20
  Placement = pos=(0,0,36.15) rot=(0,0,1;0rad)
  Radius = 8.2
FEATURE [Part::Cylinder] Cylinder021
  Angle = 360
  AttacherType = Attacher::AttachEngine3D
  Height = 10
  Placement = pos=(0,0,36.15) rot=(0,0,1;0rad)
  Radius = 4
FEATURE [Part::MultiFuse] Fusion038  label="removeToCreteHoleForPlugHousing007"
  Placement = pos=(-42,19,36) rot=(0,1,0;1.5708rad)
  Shapes = -> [Cylinder020,Cylinder021]
FEATURE [Part::Cut] Cut011
  Base = -> Extrude008
  Tool = -> Fusion038
FEATURE [Part::Fillet] Fillet011
  Base = -> Cut011
  Edges = 1 edges r=2: [Edge1]
FEATURE [Part::Fillet] Fillet012
  Base = -> Fillet011
  Edges = 1 edges r=2.5: [Edge1]
FEATURE [Part::Fillet] Fillet013
  Base = -> Fillet012
  Edges = 1 edges r=2.5: [Edge2]
FEATURE [Part::Box] Box010  label="Cube010"
  AttacherType = Attacher::AttachEngine3D
  Height = 16
  Length = 8
  Placement = pos=(12.7,31.52,28) rot=(0,0,1;0rad)
  Width = 4
FEATURE [Sketcher::SketchObject] Sketch010  label="topSketch004"
  FullyConstrained = true
  sketch-geometry (4):
    g0: LineSegment StartX=16.8446 StartY=31.512 StartZ=0 EndX=16.3251 EndY=34.4666 EndZ=0
    g1: ArcOfCircle CenterX=19 CenterY=19.2524 CenterZ=0 NormalX=0 NormalY=0 NormalZ=1 AngleXU=0 Radius=15.4476 StartAngle=1.74483 EndAngle=2.72717
    g2: ArcOfCircle CenterX=19 CenterY=19.2524 CenterZ=0 NormalX=0 NormalY=0 NormalZ=1 AngleXU=0 Radius=12.4476 StartAngle=1.74483 EndAngle=2.73189
    g3: LineSegment StartX=4.86004 StartY=25.4725 StartZ=0 EndX=7.58253 EndY=24.2107 EndZ=0
  constraints (7):
    c: Block(g0)
    c: Coincident(g1,g0)
    c: Coincident(g2,g0)
    c: Coincident(g3,g1)
    c: Coincident(g3,g2)
    c: Block(g1)
    c: Block(g2)
FEATURE [Part::Cylinder] Cylinder022
  Angle = 360
  AttacherType = Attacher::AttachEngine3D
  Height = 10
  Placement = pos=(0,0,36.15) rot=(0,0,1;0rad)
  Radius = 4
FEATURE [Sketcher::SketchObject] Sketch011  label="topSketch005"
  FullyConstrained = true
  sketch-geometry (4):
    g0: LineSegment StartX=16.8446 StartY=31.512 StartZ=0 EndX=16.3251 EndY=34.4666 EndZ=0
    g1: ArcOfCircle CenterX=19 CenterY=19.2524 CenterZ=0 NormalX=0 NormalY=0 NormalZ=1 AngleXU=0 Radius=15.4476 StartAngle=1.74483 EndAngle=2.72717
    g2: ArcOfCircle CenterX=19 CenterY=19.2524 CenterZ=0 NormalX=0 NormalY=0 NormalZ=1 AngleXU=0 Radius=12.4476 StartAngle=1.74483 EndAngle=2.73189
    g3: LineSegment StartX=4.86004 StartY=25.4725 StartZ=0 EndX=7.58253 EndY=24.2107 EndZ=0
  constraints (7):
    c: Block(g0)
    c: Coincident(g1,g0)
    c: Coincident(g2,g0)
    c: Coincident(g3,g1)
    c: Coincident(g3,g2)
    c: Block(g1)
    c: Block(g2)
FEATURE [Part::Extrusion] Extrude010
  Base = -> Sketch011
  Dir = (0,0,1)
  DirMode = 2
  FaceMakerClass = Part::FaceMakerBullseye
  LengthFwd = 10.6
  LengthRev = 0
  Placement = pos=(0,0,31) rot=(0,0,1;0rad)
  Solid = true
  Symmetric = false
FEATURE [Part::Cylinder] Cylinder023
  Angle = 360
  AttacherType = Attacher::AttachEngine3D
  Height = 20
  Placement = pos=(0,0,36.15) rot=(0,0,1;0rad)
  Radius = 8.2
FEATURE [Part::MultiFuse] Fusion039  label="removeToCreteHoleForPlugHousing008"
  Placement = pos=(-42,19,36) rot=(0,1,0;1.5708rad)
  Shapes = -> [Cylinder023,Cylinder022]
FEATURE [Part::Cut] Cut012
  Base = -> Extrude010
  Placement = pos=(0,0,-0.3) rot=(0,0,1;0rad)
  Tool = -> Fusion039
FEATURE [Part::Cut] Cut013
  Base = -> Box010
  Tool = -> Cut012
FEATURE [Part::Fillet] Fillet014
  Base = -> Cut013
  Edges = 1 edges r=0.7: [Edge13]
FEATURE [Part::Fillet] Fillet015
  Base = -> Fillet014
  Edges = 1 edges r=0.7: [Edge13]
FEATURE [Part::Fillet] Fillet016
  Base = -> Fillet015
  Edges = 1 edges r=0.7: [Edge16]
FEATURE [Part::Fillet] Fillet017
  Base = -> Fillet016
  Edges = 1 edges r=0.7: [Edge11]
FEATURE [Part::Fillet] Fillet018
  Base = -> Fillet017
  Edges = 1 edges r=0.7: [Edge10]
FEATURE [Part::Fillet] Fillet019
  Base = -> Fillet018
  Edges = 1 edges r=1.2: [Edge5]
FEATURE [Part::Fillet] Fillet020
  Base = -> Fillet019
  Edges = 1 edges r=1.2: [Edge12]
FEATURE [Part::Fillet] Fillet021
  Base = -> Fillet020
  Edges = 1 edges r=2: [Edge1]
  Placement = pos=(0.3,0,0) rot=(0,0,1;0rad)
FEATURE [Part::MultiFuse] Fusion040  label="top005"
  Shapes = -> [Cut008,Fillet021]
FEATURE [Part::MultiFuse] Fusion041  label="wireHolder"
  Shapes = -> [Fusion033,Fillet013]
FEATURE [Part::MultiFuse] Fusion042
  Shapes = -> [Fillet007,Fusion041]
FEATURE [Part::MultiFuse] Fusion043  label="wireHolder001"
  Shapes = -> [Fusion042,Fillet010]
FEATURE [Part::MultiFuse] Fusion044  label="wireHolder002"
  Shapes = -> [Fillet006,Fusion037,Fusion043]
FEATURE [Part::Feature] Face026
  shape: bbox 11 x 6 x 2e-07 mm, 1 faces, 0 solids (baked)
FEATURE [Part::Revolution] Revolve026
  Angle = 360
  Axis = (0,1,0)
  Base = (0,0,0)
  FaceMakerClass = Part::FaceMakerBullseye
  Placement = pos=(30.3,-1,19.7) rot=(0,0,1;0rad)
  Solid = false
  Source = -> Face026
  Symmetric = false
FEATURE [Sketcher::SketchObject] Sketch013  label="topSketch006"
  FullyConstrained = true
  sketch-geometry (13):
    g0: LineSegment StartX=117 StartY=19 StartZ=0 EndX=117 EndY=38 EndZ=0
    g1: ArcOfCircle CenterX=98 CenterY=19 CenterZ=0 NormalX=0 NormalY=0 NormalZ=1 AngleXU=0 Radius=19 StartAngle=5.7297 EndAngle=6.28319
    g2: LineSegment StartX=0 StartY=3 StartZ=0 EndX=0 EndY=19 EndZ=0
    g3: LineSegment StartX=19 StartY=38 StartZ=0 EndX=117 EndY=38 EndZ=0
    g4: ArcOfCircle CenterX=19 CenterY=19 CenterZ=0 NormalX=0 NormalY=0 NormalZ=1 AngleXU=0 Radius=19 StartAngle=1.5708 EndAngle=3.14159
    g5: ArcOfCircle CenterX=19 CenterY=19 CenterZ=0 NormalX=0 NormalY=0 NormalZ=1 AngleXU=0 Radius=16 StartAngle=1.5708 EndAngle=3.14159
    g6: ArcOfCircle CenterX=98 CenterY=19 CenterZ=0 NormalX=0 NormalY=0 NormalZ=1 AngleXU=0 Radius=16 StartAngle=5.60905 EndAngle=6.28319
    g7: LineSegment StartX=114 StartY=19 StartZ=0 EndX=114 EndY=35 EndZ=0
    g8: LineSegment StartX=110.5 StartY=9.01251 StartZ=0 EndX=114.163 EndY=9.01251 EndZ=0
    g9: LineSegment StartX=114 StartY=35 StartZ=0 EndX=19 EndY=35 EndZ=0
    g10: LineSegment StartX=0 StartY=3 StartZ=0 EndX=0 EndY=0 EndZ=0
    g11: LineSegment StartX=3 StartY=0 StartZ=0 EndX=0 EndY=0 EndZ=0
    g12: LineSegment StartX=3 StartY=19 StartZ=0 EndX=3 EndY=0 EndZ=0
  constraints (33):
    c: Vertical(g0)
    c: Distance(g0) = 19
    c: Block(g0)
    c: Coincident(g1,g0)
    c: Block(g1)
    c: Vertical(g2)
    c: Block(g2)
    c: Coincident(g3,g0)
    c: Horizontal(g3)
    c: Distance(g3) = 98
    c: Coincident(g4,g3)
    c: Coincident(g4,g2)
    c: Block(g4)
    c: Coincident(g5,g4)
    c: Coincident(g6,g1)
    c: Block(g6)
    c: Block(g5)
    c: Coincident(g7,g6)
    c: Vertical(g7)
    c: Coincident(g8,g6)
    c: Coincident(g8,g1)
    c: Coincident(g9,g7)
    c: Coincident(g9,g5)
    c: Horizontal(g9)
    c: Tangent(g9,g5)
    c: Coincident(g10,g2)
    c: Distance(g10) = 3
    c: Vertical(g10)
    c: Coincident(g11,g10)
    c: Horizontal(g11)
    c: Coincident(g12,g5)
    c: Coincident(g12,g11)
    c: Vertical(g12)
FEATURE [Part::Extrusion] Extrude011  label="top006"
  Base = -> Sketch013
  Dir = (0,0,1)
  DirMode = 2
  FaceMakerClass = Part::FaceMakerBullseye
  LengthFwd = 72
  LengthRev = 0
  Solid = true
  Symmetric = false
FEATURE [Sketcher::SketchObject] Sketch014
  FullyConstrained = true
  MapMode = 3
  Placement = pos=(0,0,0) rot=(1,0,0;1.5708rad)
  Support = -> [Extrude011]
  sketch-geometry (8):
    g0: Circle CenterX=80.351 CenterY=-67.6202 CenterZ=0 NormalX=0 NormalY=0 NormalZ=1 AngleXU=0 Radius=2
    g1: Circle CenterX=80.351 CenterY=-67.6202 CenterZ=0 NormalX=0 NormalY=0 NormalZ=1 AngleXU=0 Radius=3
    g2: Circle CenterX=80.351 CenterY=-4.92017 CenterZ=0 NormalX=0 NormalY=0 NormalZ=1 AngleXU=0 Radius=2
    g3: Circle CenterX=80.351 CenterY=-4.92017 CenterZ=0 NormalX=0 NormalY=0 NormalZ=1 AngleXU=0 Radius=3
    g4: Circle CenterX=23.851 CenterY=-4.92017 CenterZ=0 NormalX=0 NormalY=0 NormalZ=1 AngleXU=0 Radius=2
    g5: Circle CenterX=23.851 CenterY=-4.92017 CenterZ=0 NormalX=0 NormalY=0 NormalZ=1 AngleXU=0 Radius=3
    g6: Circle CenterX=23.851 CenterY=-67.6202 CenterZ=0 NormalX=0 NormalY=0 NormalZ=1 AngleXU=0 Radius=2
    g7: Circle CenterX=23.851 CenterY=-67.6202 CenterZ=0 NormalX=0 NormalY=0 NormalZ=1 AngleXU=0 Radius=3
  constraints (8):
    c: Block(g3)
    c: Block(g2)
    c: Block(g1)
    c: Block(g0)
    c: Block(g6)
    c: Block(g7)
    c: Block(g4)
    c: Block(g5)
FEATURE [Part::Feature] Face027
  shape: bbox 11 x 6 x 2e-07 mm, 1 faces, 0 solids (baked)
FEATURE [Part::Revolution] Revolve027
  Angle = 360
  Axis = (0,1,0)
  Base = (0,0,0)
  FaceMakerClass = Part::FaceMakerBullseye
  Placement = pos=(30.3,-1,51.7) rot=(0,0,1;0rad)
  Solid = false
  Source = -> Face027
  Symmetric = false
FEATURE [Part::Feature] Face028
  shape: bbox 11 x 6 x 2e-07 mm, 1 faces, 0 solids (baked)
FEATURE [Part::Revolution] Revolve028
  Angle = 360
  Axis = (0,1,0)
  Base = (0,0,0)
  FaceMakerClass = Part::FaceMakerBullseye
  Placement = pos=(62.3,-1,19.7) rot=(0,0,1;0rad)
  Solid = false
  Source = -> Face028
  Symmetric = false
FEATURE [Part::Feature] Face029
  shape: bbox 11 x 6 x 2e-07 mm, 1 faces, 0 solids (baked)
FEATURE [Part::Revolution] Revolve029
  Angle = 360
  Axis = (0,1,0)
  Base = (0,0,0)
  FaceMakerClass = Part::FaceMakerBullseye
  Placement = pos=(62.3,-1,51.7) rot=(0,0,1;0rad)
  Solid = false
  Source = -> Face029
  Symmetric = false
FEATURE [Part::Feature] Wire
  shape: bbox 11 x 5.2 x 2e-07 mm, 0 faces, 0 solids (baked)
FEATURE [Part::Revolution] Revolve030
  Angle = 360
  Axis = (0,1,0)
  Base = (0,0,0)
  FaceMakerClass = Part::FaceMakerBullseye
  Placement = pos=(30.3,38,19.7) rot=(0,0,1;0rad)
  Solid = true
  Source = -> Wire
  Symmetric = false
FEATURE [Part::Feature] Wire001
  shape: bbox 11 x 5.2 x 2e-07 mm, 0 faces, 0 solids (baked)
FEATURE [Part::Revolution] Revolve031
  Angle = 360
  Axis = (0,1,0)
  Base = (0,0,0)
  FaceMakerClass = Part::FaceMakerBullseye
  Placement = pos=(30.3,38,51.7) rot=(0,0,1;0rad)
  Solid = true
  Source = -> Wire001
  Symmetric = false
FEATURE [Part::Feature] Wire002
  shape: bbox 11 x 5.2 x 2e-07 mm, 0 faces, 0 solids (baked)
FEATURE [Part::Revolution] Revolve032
  Angle = 360
  Axis = (0,1,0)
  Base = (0,0,0)
  FaceMakerClass = Part::FaceMakerBullseye
  Placement = pos=(62.3,38,51.7) rot=(0,0,1;0rad)
  Solid = true
  Source = -> Wire002
  Symmetric = false
FEATURE [Part::Feature] Wire003
  shape: bbox 11 x 5.2 x 2e-07 mm, 0 faces, 0 solids (baked)
FEATURE [Part::Revolution] Revolve033
  Angle = 360
  Axis = (0,1,0)
  Base = (0,0,0)
  FaceMakerClass = Part::FaceMakerBullseye
  Placement = pos=(62.3,38,19.7) rot=(0,0,1;0rad)
  Solid = true
  Source = -> Wire003
  Symmetric = false
FEATURE [Part::MultiFuse] Fusion045  label="altRandScrewHousing"
  Shapes = -> [Revolve029,Revolve027,Revolve028,Revolve026]
FEATURE [Part::MultiFuse] Fusion046  label="fanScrewHousing"
  Shapes = -> [Revolve033,Revolve032,Revolve031,Revolve030]
FEATURE [Sketcher::SketchObject] Sketch015
  FullyConstrained = true
  sketch-geometry (17):
    g0: Circle CenterX=-3.5 CenterY=23.5 CenterZ=0 NormalX=0 NormalY=0 NormalZ=1 AngleXU=0 Radius=1
    g1: Circle CenterX=-1 CenterY=15.25 CenterZ=0 NormalX=0 NormalY=0 NormalZ=1 AngleXU=0 Radius=1
    g2: Circle CenterX=-3.5 CenterY=7 CenterZ=0 NormalX=0 NormalY=0 NormalZ=1 AngleXU=0 Radius=1
    g3: BSplineCurve PolesCount=3 KnotsCount=2 Degree=2 IsPeriodic=0
    g4: GeomPoint X=-3.5 Y=23.5 Z=0
    g5: GeomPoint X=-3.5 Y=7 Z=0
    g6: Circle CenterX=-4.8 CenterY=30.5 CenterZ=0 NormalX=0 NormalY=0 NormalZ=1 AngleXU=0 Radius=1
    g7: Circle CenterX=-3.5 CenterY=30.5 CenterZ=0 NormalX=0 NormalY=0 NormalZ=1 AngleXU=0 Radius=1
    g8: Circle CenterX=-3.5 CenterY=29.2 CenterZ=0 NormalX=0 NormalY=0 NormalZ=1 AngleXU=0 Radius=1
    g9: BSplineCurve PolesCount=3 KnotsCount=2 Degree=2 IsPeriodic=0
    g10: GeomPoint X=-4.8 Y=30.5 Z=0
    g11: GeomPoint X=-3.5 Y=29.2 Z=0
    g12: LineSegment StartX=-3.5 StartY=29.2 StartZ=0 EndX=-3.5 EndY=23.5 EndZ=0
    g13: LineSegment StartX=-4.8 StartY=30.5 StartZ=0 EndX=0 EndY=30.5 EndZ=0
    g14: LineSegment StartX=-3.5 StartY=0.3 StartZ=0 EndX=0 EndY=0.3 EndZ=0
    g15: LineSegment StartX=-3.5 StartY=0.3 StartZ=0 EndX=-3.5 EndY=7 EndZ=0
    g16: LineSegment StartX=0 StartY=0.3 StartZ=0 EndX=0 EndY=30.5 EndZ=0
  constraints (33):
    c: Weight(g0) = 1
    c: Equal(g0,g1)
    c: Equal(g0,g2)
    c: InternalAlignment(g0,g3)
    c: InternalAlignment(g1,g3)
    c: InternalAlignment(g2,g3)
    c: InternalAlignment(g4,g3)
    c: InternalAlignment(g5,g3)
    c: Block(g3)
    c: Weight(g6) = 1
    c: Equal(g6,g7)
    c: Equal(g6,g8)
    c: InternalAlignment(g6,g9)
    c: InternalAlignment(g7,g9)
    c: InternalAlignment(g8,g9)
    c: InternalAlignment(g10,g9)
    c: InternalAlignment(g11,g9)
    c: Block(g9)
    c: Coincident(g12,g9)
    c: Coincident(g12,g3)
    c: Vertical(g12)
    c: Coincident(g13,g9)
    c: Horizontal(g13)
    c: Distance(g13) = 4.8
    c: Horizontal(g14)
    c: Block(g14)
    c: Coincident(g15,g14)
    c: Coincident(g15,g3)
    c: Vertical(g15)
    c: Coincident(g16,g14)
    c: Coincident(g16,g13)
    c: Vertical(g16)
    c: Tangent(g16,g1)
FEATURE [Sketcher::SketchObject] Sketch016
  FullyConstrained = true
  sketch-geometry (16):
    g0: Circle CenterX=-3.5 CenterY=23.5 CenterZ=0 NormalX=0 NormalY=0 NormalZ=1 AngleXU=0 Radius=1
    g1: Circle CenterX=-1 CenterY=15.25 CenterZ=0 NormalX=0 NormalY=0 NormalZ=1 AngleXU=0 Radius=1
    g2: Circle CenterX=-3.5 CenterY=7 CenterZ=0 NormalX=0 NormalY=0 NormalZ=1 AngleXU=0 Radius=1
    g3: BSplineCurve PolesCount=3 KnotsCount=2 Degree=2 IsPeriodic=0
    g4: GeomPoint X=-3.5 Y=23.5 Z=0
    g5: GeomPoint X=-3.5 Y=7 Z=0
    g6: LineSegment StartX=-3.5 StartY=28.2 StartZ=0 EndX=-3.5 EndY=23.5 EndZ=0
    g7: LineSegment StartX=0 StartY=29.5 StartZ=0 EndX=0 EndY=30 EndZ=0
    g8: LineSegment StartX=-3.5 StartY=28.2 StartZ=0 EndX=-3.5 EndY=30 EndZ=0
    g9: LineSegment StartX=0 StartY=30 StartZ=0 EndX=0 EndY=30.5 EndZ=0
    g10: LineSegment StartX=0 StartY=30.5 StartZ=0 EndX=-3.5 EndY=30.5 EndZ=0
    g11: LineSegment StartX=-3.5 StartY=30.5 StartZ=0 EndX=-3.5 EndY=30 EndZ=0
    g12: LineSegment StartX=0 StartY=29.5 StartZ=0 EndX=0 EndY=5 EndZ=0
    g13: LineSegment StartX=-3.5 StartY=0.3 StartZ=0 EndX=-3.5 EndY=7 EndZ=0
    g14: LineSegment StartX=-3.5 StartY=0.3 StartZ=0 EndX=0 EndY=0.3 EndZ=0
    g15: LineSegment StartX=0 StartY=5 StartZ=0 EndX=0 EndY=0.3 EndZ=0
  constraints (39):
    c: Weight(g0) = 1
    c: Equal(g0,g1)
    c: Equal(g0,g2)
    c: InternalAlignment(g0,g3)
    c: InternalAlignment(g1,g3)
    c: InternalAlignment(g2,g3)
    c: InternalAlignment(g4,g3)
    c: InternalAlignment(g5,g3)
    c: Block(g3)
    c: Coincident(g6,g3)
    c: Vertical(g6)
    c: Vertical(g7)
    c: Distance(g7) = 0.5
    c: Coincident(g8,g6)
    c: Vertical(g8)
    c: Block(g6)
    c: Block(g7)
    c: Vertical(g9)
    c: Equal(g7,g9) = 0.5
    c: Block(g9)
    c: Coincident(g9,g7)
    c: Horizontal(g10)
    c: Coincident(g10,g9)
    c: Coincident(g11,g10)
    c: Coincident(g11,g8)
    c: Vertical(g11)
    c: Block(g11)
    c: Coincident(g12,g7)
    c: Vertical(g12)
    c: Coincident(g13,g3)
    c: Vertical(g13)
    c: Distance(g13) = 6.7
    c: Coincident(g14,g13)
    c: Horizontal(g14)
    c: Block(g14)
    c: Coincident(g15,g12)
    c: Coincident(g15,g14)
    c: Vertical(g15)
    c: Block(g15)
FEATURE [Sketcher::SketchObject] Sketch017
  FullyConstrained = true
  sketch-geometry (11):
    g0: LineSegment StartX=-3.5 StartY=1e-16 StartZ=0 EndX=-1.6 EndY=1e-16 EndZ=0
    g1: LineSegment StartX=-1.6 StartY=1e-16 StartZ=0 EndX=-1.6 EndY=1.5 EndZ=0
    g2: LineSegment StartX=-3.5 StartY=1.5 StartZ=0 EndX=-1.6 EndY=1.5 EndZ=0
    g3: LineSegment StartX=-3.5 StartY=1e-16 StartZ=0 EndX=-4.8 EndY=1e-16 EndZ=0
    g4: Circle CenterX=-3.5 CenterY=1.3 CenterZ=0 NormalX=0 NormalY=0 NormalZ=1 AngleXU=0 Radius=1
    g5: Circle CenterX=-3.5 CenterY=1e-16 CenterZ=0 NormalX=0 NormalY=0 NormalZ=1 AngleXU=0 Radius=1
    g6: Circle CenterX=-4.8 CenterY=1e-16 CenterZ=0 NormalX=0 NormalY=0 NormalZ=1 AngleXU=0 Radius=1
    g7: BSplineCurve PolesCount=3 KnotsCount=2 Degree=2 IsPeriodic=0
    g8: GeomPoint X=-3.5 Y=1.3 Z=0
    g9: GeomPoint X=-4.8 Y=1e-16 Z=0
    g10: LineSegment StartX=-3.5 StartY=1.3 StartZ=0 EndX=-3.5 EndY=1.5 EndZ=0
  constraints (24):
    c: Horizontal(g0)
    c: Distance(g0) = 1.9
    c: Block(g0)
    c: Coincident(g1,g0)
    c: Vertical(g1)
    c: Coincident(g2,g1)
    c: Horizontal(g2)
    c: Coincident(g3,g0)
    c: Horizontal(g3)
    c: Distance(g3) = 1.3
    c: Weight(g4) = 1
    c: Equal(g4,g5)
    c: Coincident(g5,g0)
    c: Equal(g4,g6)
    c: Coincident(g7,g3)
    c: InternalAlignment(g4,g7)
    c: InternalAlignment(g5,g7)
    c: InternalAlignment(g6,g7)
    c: InternalAlignment(g8,g7)
    c: InternalAlignment(g9,g7)
    c: Coincident(g10,g7)
    c: Coincident(g10,g2)
    c: Vertical(g10)
    c: Block(g10)
FEATURE [Part::Feature] Face035
  shape: bbox 3.2 x 1.5 x 2e-07 mm, 1 faces, 0 solids (baked)
FEATURE [Part::Revolution] Revolve039  label="backCaseScrewRetainer"
  Angle = 360
  Axis = (0,1,0)
  Base = (0,0,0)
  FaceMakerClass = Part::FaceMakerBullseye
  Placement = pos=(12.5,3,62) rot=(0,0,1;0rad)
  Solid = false
  Source = -> Face035
  Symmetric = false
FEATURE [Part::Feature] Face036
  shape: bbox 3.2 x 1.5 x 2e-07 mm, 1 faces, 0 solids (baked)
FEATURE [Part::Feature] Face039
  shape: bbox 4.8 x 30.2 x 2e-07 mm, 1 faces, 0 solids (baked)
FEATURE [Part::Revolution] Revolve043  label="frontCaseScrewPost002"
  Angle = 360
  Axis = (0,1,0)
  Base = (0,0,0)
  FaceMakerClass = Part::FaceMakerBullseye
  Placement = pos=(89.5,4.5,3.5) rot=(0,0,1;0rad)
  Solid = false
  Source = -> Face039
  Symmetric = false
FEATURE [Part::Feature] Face042
  shape: bbox 4.8 x 30.2 x 2e-07 mm, 1 faces, 0 solids (baked)
FEATURE [Part::Revolution] Revolve046  label="frontCaseScrewPost003"
  Angle = 360
  Axis = (0,1,0)
  Base = (0,0,0)
  FaceMakerClass = Part::FaceMakerBullseye
  Placement = pos=(89.5,4.5,68.5) rot=(0,0,1;0rad)
  Solid = false
  Source = -> Face042
  Symmetric = false
FEATURE [Part::Feature] Face043
  shape: bbox 3.2 x 1.5 x 2e-07 mm, 1 faces, 0 solids (baked)
FEATURE [Part::Revolution] Revolve047  label="frontCaseScrewRetainer002"
  Angle = 360
  Axis = (0,1,0)
  Base = (0,0,0)
  FaceMakerClass = Part::FaceMakerBullseye
  Placement = pos=(89.5,3,68.5) rot=(0,0,1;0rad)
  Solid = false
  Source = -> Face043
  Symmetric = false
FEATURE [Part::Feature] Face044
  shape: bbox 3.2 x 1.5 x 2e-07 mm, 1 faces, 0 solids (baked)
FEATURE [Part::Revolution] Revolve048  label="frontCaseScrewRetainer003"
  Angle = 360
  Axis = (0,1,0)
  Base = (0,0,0)
  FaceMakerClass = Part::FaceMakerBullseye
  Placement = pos=(89.5,3,3.5) rot=(0,0,1;0rad)
  Solid = false
  Source = -> Face044
  Symmetric = false
FEATURE [App::MeasureDistance] Distance002  label="Distance: 1.67 mm"
  Distance = 1.66921
  P1 = (99.2361,4.7524,71.7)
  P2 = (99.2347,6.42161,71.7)
FEATURE [Sketcher::SketchObject] Sketch018
  FullyConstrained = true
  sketch-geometry (7):
    g0: LineSegment StartX=0 StartY=0 StartZ=0 EndX=0 EndY=6 EndZ=0
    g1: Circle CenterX=0 CenterY=0 CenterZ=0 NormalX=0 NormalY=0 NormalZ=1 AngleXU=0 Radius=1
    g2: Circle CenterX=8 CenterY=6 CenterZ=0 NormalX=0 NormalY=0 NormalZ=1 AngleXU=0 Radius=1
    g3: BSplineCurve PolesCount=3 KnotsCount=2 Degree=2 IsPeriodic=0
    g4: GeomPoint X=0 Y=0 Z=0
    g5: GeomPoint X=8 Y=6 Z=0
    g6: LineSegment StartX=0 StartY=6 StartZ=0 EndX=8 EndY=6 EndZ=0
  constraints (14):
    c: Coincident(g0,g-1)
    c: Distance(g0) = 6
    c: Vertical(g0)
    c: Coincident(g3,g0)
    c: Weight(g1) = 1
    c: Equal(g1,g2)
    c: InternalAlignment(g1,g3)
    c: InternalAlignment(g2,g3)
    c: InternalAlignment(g4,g3)
    c: InternalAlignment(g5,g3)
    c: Block(g3)
    c: Coincident(g6,g0)
    c: Coincident(g6,g3)
    c: Horizontal(g6)
FEATURE [Part::Extrusion] Extrude012  label="caseScrewPillarBracket"
  Base = -> Sketch018
  Dir = (0,0,1)
  DirMode = 2
  FaceMakerClass = Part::FaceMakerBullseye
  LengthFwd = 2.4
  LengthRev = 0
  Placement = pos=(15.76,29,8.8) rot=(0,1,0;0rad)
  Solid = true
  Symmetric = false
FEATURE [Sketcher::SketchObject] Sketch019
  FullyConstrained = true
  sketch-geometry (7):
    g0: LineSegment StartX=0 StartY=0 StartZ=0 EndX=0 EndY=6 EndZ=0
    g1: Circle CenterX=0 CenterY=0 CenterZ=0 NormalX=0 NormalY=0 NormalZ=1 AngleXU=0 Radius=1
    g2: Circle CenterX=8 CenterY=6 CenterZ=0 NormalX=0 NormalY=0 NormalZ=1 AngleXU=0 Radius=1
    g3: BSplineCurve PolesCount=3 KnotsCount=2 Degree=2 IsPeriodic=0
    g4: GeomPoint X=0 Y=0 Z=0
    g5: GeomPoint X=8 Y=6 Z=0
    g6: LineSegment StartX=0 StartY=6 StartZ=0 EndX=8 EndY=6 EndZ=0
  constraints (14):
    c: Coincident(g0,g-1)
    c: Distance(g0) = 6
    c: Vertical(g0)
    c: Coincident(g3,g0)
    c: Weight(g1) = 1
    c: Equal(g1,g2)
    c: InternalAlignment(g1,g3)
    c: InternalAlignment(g2,g3)
    c: InternalAlignment(g4,g3)
    c: InternalAlignment(g5,g3)
    c: Block(g3)
    c: Coincident(g6,g0)
    c: Coincident(g6,g3)
    c: Horizontal(g6)
FEATURE [Part::Extrusion] Extrude013  label="caseScrewPillarBracket001"
  Base = -> Sketch019
  Dir = (0,0,1)
  DirMode = 2
  FaceMakerClass = Part::FaceMakerBullseye
  LengthFwd = 2.4
  LengthRev = 0
  Placement = pos=(15.76,29,60.8) rot=(0,0,1;0rad)
  Solid = true
  Symmetric = false
FEATURE [Sketcher::SketchObject] Sketch020
  FullyConstrained = true
  sketch-geometry (7):
    g0: LineSegment StartX=0 StartY=0 StartZ=0 EndX=0 EndY=6 EndZ=0
    g1: Circle CenterX=0 CenterY=0 CenterZ=0 NormalX=0 NormalY=0 NormalZ=1 AngleXU=0 Radius=1
    g2: Circle CenterX=8 CenterY=6 CenterZ=0 NormalX=0 NormalY=0 NormalZ=1 AngleXU=0 Radius=1
    g3: BSplineCurve PolesCount=3 KnotsCount=2 Degree=2 IsPeriodic=0
    g4: GeomPoint X=0 Y=0 Z=0
    g5: GeomPoint X=8 Y=6 Z=0
    g6: LineSegment StartX=0 StartY=6 StartZ=0 EndX=8 EndY=6 EndZ=0
  constraints (14):
    c: Coincident(g0,g-1)
    c: Distance(g0) = 6
    c: Vertical(g0)
    c: Coincident(g3,g0)
    c: Weight(g1) = 1
    c: Equal(g1,g2)
    c: InternalAlignment(g1,g3)
    c: InternalAlignment(g2,g3)
    c: InternalAlignment(g4,g3)
    c: InternalAlignment(g5,g3)
    c: Block(g3)
    c: Coincident(g6,g0)
    c: Coincident(g6,g3)
    c: Horizontal(g6)
FEATURE [Part::Extrusion] Extrude014  label="caseScrewPillarBracket002"
  Base = -> Sketch020
  Dir = (0,0,1)
  DirMode = 2
  FaceMakerClass = Part::FaceMakerBullseye
  LengthFwd = 2.4
  LengthRev = 0
  Placement = pos=(13.7,29,13.26) rot=(0,-1,0;1.5708rad)
  Solid = true
  Symmetric = false
FEATURE [Sketcher::SketchObject] Sketch021
  FullyConstrained = true
  sketch-geometry (7):
    g0: LineSegment StartX=0 StartY=0 StartZ=0 EndX=0 EndY=6 EndZ=0
    g1: Circle CenterX=0 CenterY=0 CenterZ=0 NormalX=0 NormalY=0 NormalZ=1 AngleXU=0 Radius=1
    g2: Circle CenterX=8 CenterY=6 CenterZ=0 NormalX=0 NormalY=0 NormalZ=1 AngleXU=0 Radius=1
    g3: BSplineCurve PolesCount=3 KnotsCount=2 Degree=2 IsPeriodic=0
    g4: GeomPoint X=0 Y=0 Z=0
    g5: GeomPoint X=8 Y=6 Z=0
    g6: LineSegment StartX=0 StartY=6 StartZ=0 EndX=8 EndY=6 EndZ=0
  constraints (14):
    c: Coincident(g0,g-1)
    c: Distance(g0) = 6
    c: Vertical(g0)
    c: Coincident(g3,g0)
    c: Weight(g1) = 1
    c: Equal(g1,g2)
    c: InternalAlignment(g1,g3)
    c: InternalAlignment(g2,g3)
    c: InternalAlignment(g4,g3)
    c: InternalAlignment(g5,g3)
    c: Block(g3)
    c: Coincident(g6,g0)
    c: Coincident(g6,g3)
    c: Horizontal(g6)
FEATURE [Part::Extrusion] Extrude015  label="caseScrewPillarBracket003"
  Base = -> Sketch021
  Dir = (0,0,1)
  DirMode = 2
  FaceMakerClass = Part::FaceMakerBullseye
  LengthFwd = 2.4
  LengthRev = 0
  Placement = pos=(11.3,29,58.74) rot=(0,1,0;1.5708rad)
  Solid = true
  Symmetric = false
FEATURE [Sketcher::SketchObject] Sketch022
  FullyConstrained = true
  sketch-geometry (7):
    g0: LineSegment StartX=0 StartY=0 StartZ=0 EndX=0 EndY=6 EndZ=0
    g1: Circle CenterX=0 CenterY=0 CenterZ=0 NormalX=0 NormalY=0 NormalZ=1 AngleXU=0 Radius=1
    g2: Circle CenterX=8 CenterY=6 CenterZ=0 NormalX=0 NormalY=0 NormalZ=1 AngleXU=0 Radius=1
    g3: BSplineCurve PolesCount=3 KnotsCount=2 Degree=2 IsPeriodic=0
    g4: GeomPoint X=0 Y=0 Z=0
    g5: GeomPoint X=8 Y=6 Z=0
    g6: LineSegment StartX=0 StartY=6 StartZ=0 EndX=8 EndY=6 EndZ=0
  constraints (14):
    c: Coincident(g0,g-1)
    c: Distance(g0) = 6
    c: Vertical(g0)
    c: Coincident(g3,g0)
    c: Weight(g1) = 1
    c: Equal(g1,g2)
    c: InternalAlignment(g1,g3)
    c: InternalAlignment(g2,g3)
    c: InternalAlignment(g4,g3)
    c: InternalAlignment(g5,g3)
    c: Block(g3)
    c: Coincident(g6,g0)
    c: Coincident(g6,g3)
    c: Horizontal(g6)
FEATURE [Part::Extrusion] Extrude016  label="caseScrewPillarBracket004"
  Base = -> Sketch022
  Dir = (0,0,1)
  DirMode = 2
  FaceMakerClass = Part::FaceMakerBullseye
  LengthFwd = 2.4
  LengthRev = 0
  Placement = pos=(88.3,29,65.23) rot=(0,1,0;1.5708rad)
  Solid = true
  Symmetric = false
FEATURE [Sketcher::SketchObject] Sketch023
  FullyConstrained = true
  sketch-geometry (7):
    g0: LineSegment StartX=0 StartY=0 StartZ=0 EndX=0 EndY=6 EndZ=0
    g1: Circle CenterX=0 CenterY=0 CenterZ=0 NormalX=0 NormalY=0 NormalZ=1 AngleXU=0 Radius=1
    g2: Circle CenterX=8 CenterY=6 CenterZ=0 NormalX=0 NormalY=0 NormalZ=1 AngleXU=0 Radius=1
    g3: BSplineCurve PolesCount=3 KnotsCount=2 Degree=2 IsPeriodic=0
    g4: GeomPoint X=0 Y=0 Z=0
    g5: GeomPoint X=8 Y=6 Z=0
    g6: LineSegment StartX=0 StartY=6 StartZ=0 EndX=8 EndY=6 EndZ=0
  constraints (14):
    c: Coincident(g0,g-1)
    c: Distance(g0) = 6
    c: Vertical(g0)
    c: Coincident(g3,g0)
    c: Weight(g1) = 1
    c: Equal(g1,g2)
    c: InternalAlignment(g1,g3)
    c: InternalAlignment(g2,g3)
    c: InternalAlignment(g4,g3)
    c: InternalAlignment(g5,g3)
    c: Block(g3)
    c: Coincident(g6,g0)
    c: Coincident(g6,g3)
    c: Horizontal(g6)
FEATURE [Part::Extrusion] Extrude017  label="caseScrewPillarBracket005"
  Base = -> Sketch023
  Dir = (0,0,1)
  DirMode = 2
  FaceMakerClass = Part::FaceMakerBullseye
  LengthFwd = 2.4
  LengthRev = 0
  Placement = pos=(90.7,29,6.77) rot=(0,-1,0;1.5708rad)
  Solid = true
  Symmetric = false
FEATURE [Sketcher::SketchObject] Sketch024
  FullyConstrained = true
  sketch-geometry (7):
    g0: LineSegment StartX=0 StartY=0 StartZ=0 EndX=0 EndY=6 EndZ=0
    g1: Circle CenterX=0 CenterY=0 CenterZ=0 NormalX=0 NormalY=0 NormalZ=1 AngleXU=0 Radius=1
    g2: Circle CenterX=8 CenterY=6 CenterZ=0 NormalX=0 NormalY=0 NormalZ=1 AngleXU=0 Radius=1
    g3: BSplineCurve PolesCount=3 KnotsCount=2 Degree=2 IsPeriodic=0
    g4: GeomPoint X=0 Y=0 Z=0
    g5: GeomPoint X=8 Y=6 Z=0
    g6: LineSegment StartX=0 StartY=6 StartZ=0 EndX=8 EndY=6 EndZ=0
  constraints (14):
    c: Coincident(g0,g-1)
    c: Distance(g0) = 6
    c: Vertical(g0)
    c: Coincident(g3,g0)
    c: Weight(g1) = 1
    c: Equal(g1,g2)
    c: InternalAlignment(g1,g3)
    c: InternalAlignment(g2,g3)
    c: InternalAlignment(g4,g3)
    c: InternalAlignment(g5,g3)
    c: Block(g3)
    c: Coincident(g6,g0)
    c: Coincident(g6,g3)
    c: Horizontal(g6)
FEATURE [Part::Extrusion] Extrude018  label="caseScrewPillarBracket006"
  Base = -> Sketch024
  Dir = (0,0,1)
  DirMode = 2
  FaceMakerClass = Part::FaceMakerBullseye
  LengthFwd = 2.4
  LengthRev = 0
  Placement = pos=(103.7,29,6.77) rot=(0,-1,0;1.5708rad)
  Solid = true
  Symmetric = false
FEATURE [Sketcher::SketchObject] Sketch025
  FullyConstrained = true
  sketch-geometry (7):
    g0: LineSegment StartX=0 StartY=0 StartZ=0 EndX=0 EndY=6 EndZ=0
    g1: Circle CenterX=0 CenterY=0 CenterZ=0 NormalX=0 NormalY=0 NormalZ=1 AngleXU=0 Radius=1
    g2: Circle CenterX=8 CenterY=6 CenterZ=0 NormalX=0 NormalY=0 NormalZ=1 AngleXU=0 Radius=1
    g3: BSplineCurve PolesCount=3 KnotsCount=2 Degree=2 IsPeriodic=0
    g4: GeomPoint X=0 Y=0 Z=0
    g5: GeomPoint X=8 Y=6 Z=0
    g6: LineSegment StartX=0 StartY=6 StartZ=0 EndX=8 EndY=6 EndZ=0
  constraints (14):
    c: Coincident(g0,g-1)
    c: Distance(g0) = 6
    c: Vertical(g0)
    c: Coincident(g3,g0)
    c: Weight(g1) = 1
    c: Equal(g1,g2)
    c: InternalAlignment(g1,g3)
    c: InternalAlignment(g2,g3)
    c: InternalAlignment(g4,g3)
    c: InternalAlignment(g5,g3)
    c: Block(g3)
    c: Coincident(g6,g0)
    c: Coincident(g6,g3)
    c: Horizontal(g6)
FEATURE [Part::Extrusion] Extrude019  label="caseScrewPillarBracket007"
  Base = -> Sketch025
  Dir = (0,0,1)
  DirMode = 2
  FaceMakerClass = Part::FaceMakerBullseye
  LengthFwd = 2.4
  LengthRev = 0
  Placement = pos=(101.3,29,65.23) rot=(0,1,0;1.5708rad)
  Solid = true
  Symmetric = false
FEATURE [Part::Box] Box011  label="frontCaseScrewPillarBracket"
  AttacherType = Attacher::AttachEngine3D
  Height = 2.4
  Length = 16
  Placement = pos=(87,28,2.3) rot=(0,0,1;0rad)
  Width = 7
FEATURE [Part::Box] Box012  label="frontCaseScrewPillarBracket001"
  AttacherType = Attacher::AttachEngine3D
  Height = 2.4
  Length = 16
  Placement = pos=(87,28,67.3) rot=(0,0,1;0rad)
  Width = 7
FEATURE [Sketcher::SketchObject] Sketch026
  FullyConstrained = true
  sketch-geometry (17):
    g0: Circle CenterX=-3.5 CenterY=23.5 CenterZ=0 NormalX=0 NormalY=0 NormalZ=1 AngleXU=0 Radius=1
    g1: Circle CenterX=-1 CenterY=15.25 CenterZ=0 NormalX=0 NormalY=0 NormalZ=1 AngleXU=0 Radius=1
    g2: Circle CenterX=-3.5 CenterY=7 CenterZ=0 NormalX=0 NormalY=0 NormalZ=1 AngleXU=0 Radius=1
    g3: BSplineCurve PolesCount=3 KnotsCount=2 Degree=2 IsPeriodic=0
    g4: GeomPoint X=-3.5 Y=23.5 Z=0
    g5: GeomPoint X=-3.5 Y=7 Z=0
    g6: Circle CenterX=-4.8 CenterY=30.5 CenterZ=0 NormalX=0 NormalY=0 NormalZ=1 AngleXU=0 Radius=1
    g7: Circle CenterX=-3.5 CenterY=30.5 CenterZ=0 NormalX=0 NormalY=0 NormalZ=1 AngleXU=0 Radius=1
    g8: Circle CenterX=-3.5 CenterY=29.2 CenterZ=0 NormalX=0 NormalY=0 NormalZ=1 AngleXU=0 Radius=1
    g9: BSplineCurve PolesCount=3 KnotsCount=2 Degree=2 IsPeriodic=0
    g10: GeomPoint X=-4.8 Y=30.5 Z=0
    g11: GeomPoint X=-3.5 Y=29.2 Z=0
    g12: LineSegment StartX=-3.5 StartY=29.2 StartZ=0 EndX=-3.5 EndY=23.5 EndZ=0
    g13: LineSegment StartX=-4.8 StartY=30.5 StartZ=0 EndX=0 EndY=30.5 EndZ=0
    g14: LineSegment StartX=-3.5 StartY=5 StartZ=0 EndX=-3.5 EndY=7 EndZ=0
    g15: LineSegment StartX=0 StartY=5 StartZ=0 EndX=0 EndY=30.5 EndZ=0
    g16: LineSegment StartX=-3.5 StartY=5 StartZ=0 EndX=0 EndY=5 EndZ=0
  constraints (33):
    c: Weight(g0) = 1
    c: Equal(g0,g1)
    c: Equal(g0,g2)
    c: InternalAlignment(g0,g3)
    c: InternalAlignment(g1,g3)
    c: InternalAlignment(g2,g3)
    c: InternalAlignment(g4,g3)
    c: InternalAlignment(g5,g3)
    c: Block(g3)
    c: Weight(g6) = 1
    c: Equal(g6,g7)
    c: Equal(g6,g8)
    c: InternalAlignment(g6,g9)
    c: InternalAlignment(g7,g9)
    c: InternalAlignment(g8,g9)
    c: InternalAlignment(g10,g9)
    c: InternalAlignment(g11,g9)
    c: Block(g9)
    c: Coincident(g12,g9)
    c: Coincident(g12,g3)
    c: Vertical(g12)
    c: Coincident(g13,g9)
    c: Horizontal(g13)
    c: Distance(g13) = 4.8
    c: Coincident(g14,g3)
    c: Vertical(g14)
    c: Coincident(g15,g13)
    c: Vertical(g15)
    c: Tangent(g15,g1)
    c: Distance(g14) = 2
    c: Coincident(g16,g14)
    c: Horizontal(g16)
    c: Coincident(g15,g16)
FEATURE [Part::Feature] Face050
  shape: bbox 4.8 x 25.5 x 2e-07 mm, 1 faces, 0 solids (baked)
FEATURE [Part::Revolution] Revolve054  label="moreFrontCaseScrewPost001"
  Angle = 360
  Axis = (0,1,0)
  Base = (0,0,0)
  FaceMakerClass = Part::FaceMakerBullseye
  Placement = pos=(102.5,4.5,3.5) rot=(0,0,1;0rad)
  Solid = false
  Source = -> Face050
  Symmetric = false
FEATURE [Part::Feature] Face051
  shape: bbox 4.8 x 25.5 x 2e-07 mm, 1 faces, 0 solids (baked)
FEATURE [Part::Revolution] Revolve055  label="moreFrontCaseScrewPost002"
  Angle = 360
  Axis = (0,1,0)
  Base = (0,0,0)
  FaceMakerClass = Part::FaceMakerBullseye
  Placement = pos=(102.5,4.5,68.5) rot=(0,0,1;0rad)
  Solid = false
  Source = -> Face051
  Symmetric = false
FEATURE [Sketcher::SketchObject] Sketch027
  FullyConstrained = true
  sketch-geometry (10):
    g0: LineSegment StartX=-1.6 StartY=4.7 StartZ=0 EndX=-1.6 EndY=1.7 EndZ=0
    g1: LineSegment StartX=-3.5 StartY=4.7 StartZ=0 EndX=-1.6 EndY=4.7 EndZ=0
    g2: LineSegment StartX=-1.6 StartY=1.7 StartZ=0 EndX=-1.6 EndY=1.5 EndZ=0
    g3: LineSegment StartX=-1.6 StartY=1.5 StartZ=0 EndX=-5.2 EndY=1.5 EndZ=0
    g4: Circle CenterX=-3.5 CenterY=4.7 CenterZ=0 NormalX=0 NormalY=0 NormalZ=1 AngleXU=0 Radius=1
    g5: Circle CenterX=-3.59627 CenterY=2.99743 CenterZ=0 NormalX=0 NormalY=0 NormalZ=1 AngleXU=0 Radius=1
    g6: Circle CenterX=-5.2 CenterY=1.5 CenterZ=0 NormalX=0 NormalY=0 NormalZ=1 AngleXU=0 Radius=1
    g7: BSplineCurve PolesCount=3 KnotsCount=2 Degree=2 IsPeriodic=0
    g8: GeomPoint X=-3.5 Y=4.7 Z=0
    g9: GeomPoint X=-5.2 Y=1.5 Z=0
  constraints (23):
    c: Vertical(g0)
    c: Distance(g0) = 3
    c: Coincident(g1,g0)
    c: Horizontal(g1)
    c: Block(g0)
    c: Block(g1)
    c: Coincident(g2,g0)
    c: Vertical(g2)
    c: Distance(g2) = 0.2
    c: Coincident(g3,g2)
    c: Horizontal(g3)
    c: Block(g3)
    c: Coincident(g7,g1)
    c: Weight(g4) = 1
    c: Equal(g4,g5)
    c: Equal(g4,g6)
    c: Coincident(g7,g3)
    c: InternalAlignment(g4,g7)
    c: InternalAlignment(g5,g7)
    c: InternalAlignment(g6,g7)
    c: InternalAlignment(g8,g7)
    c: InternalAlignment(g9,g7)
    c: Block(g7)
FEATURE [Sketcher::SketchObject] Sketch028
  FullyConstrained = true
  sketch-geometry (18):
    g0: LineSegment StartX=0 StartY=3e-16 StartZ=0 EndX=0 EndY=1.7 EndZ=0
    g1: LineSegment StartX=-3.5 StartY=0 StartZ=0 EndX=-3.5 EndY=0.9 EndZ=0
    g2: Circle CenterX=-2.7 CenterY=1.7 CenterZ=0 NormalX=0 NormalY=0 NormalZ=1 AngleXU=0 Radius=1
    g3: Circle CenterX=-3.5 CenterY=1.7 CenterZ=0 NormalX=0 NormalY=0 NormalZ=1 AngleXU=0 Radius=1
    g4: Circle CenterX=-3.5 CenterY=0.9 CenterZ=0 NormalX=0 NormalY=0 NormalZ=1 AngleXU=0 Radius=1
    g5: BSplineCurve PolesCount=3 KnotsCount=2 Degree=2 IsPeriodic=0
    g6: GeomPoint X=-2.7 Y=1.7 Z=0
    g7: GeomPoint X=-3.5 Y=0.9 Z=0
    g8: LineSegment StartX=-3.5 StartY=0 StartZ=0 EndX=-3.5 EndY=-7 EndZ=0
    g9: LineSegment StartX=0 StartY=3e-16 StartZ=0 EndX=0 EndY=-7 EndZ=0
    g10: LineSegment StartX=-3.5 StartY=-7 StartZ=0 EndX=0 EndY=-7 EndZ=0
    g11: LineSegment StartX=-2.7 StartY=1.7 StartZ=0 EndX=-1.6 EndY=1.7 EndZ=0
    g12: LineSegment StartX=0 StartY=1.7 StartZ=0 EndX=0 EndY=4.5 EndZ=0
    g13: LineSegment StartX=0 StartY=4.5 StartZ=0 EndX=0 EndY=10.8 EndZ=0
    g14: LineSegment StartX=0 StartY=10.8 StartZ=0 EndX=-2 EndY=10.8 EndZ=0
    g15: LineSegment StartX=-1.6 StartY=4.7 StartZ=0 EndX=-1.6 EndY=1.7 EndZ=0
    g16: LineSegment StartX=-1.6 StartY=4.7 StartZ=0 EndX=-2 EndY=4.7 EndZ=0
    g17: LineSegment StartX=-2 StartY=4.7 StartZ=0 EndX=-2 EndY=10.8 EndZ=0
  constraints (44):
    c: Vertical(g0)
    c: Vertical(g1)
    c: Distance(g1) = 0.9
    c: Block(g0)
    c: Distance(g0) = 1.7
    c: Weight(g2) = 1
    c: Equal(g2,g3)
    c: Equal(g2,g4)
    c: Coincident(g5,g1)
    c: InternalAlignment(g2,g5)
    c: InternalAlignment(g3,g5)
    c: InternalAlignment(g4,g5)
    c: InternalAlignment(g6,g5)
    c: InternalAlignment(g7,g5)
    c: Block(g5)
    c: Coincident(g8,g1)
    c: Vertical(g8)
    c: Distance(g8) = 7
    c: Vertical(g9)
    c: Equal(g8,g9) = 7
    c: Coincident(g9,g0)
    c: Coincident(g10,g8)
    c: Coincident(g10,g9)
    c: Horizontal(g10)
    c: Coincident(g11,g5)
    c: Horizontal(g11)
    c: Coincident(g12,g0)
    c: Vertical(g12)
    c: Distance(g12) = 2.8
    c: Coincident(g13,g12)
    c: Vertical(g13)
    c: Distance(g13) = 6.3
    c: Coincident(g14,g13)
    c: Horizontal(g14)
    c: Distance(g14) = 2
    c: Vertical(g15)
    c: Distance(g15) = 3
    c: Block(g11)
    c: Coincident(g15,g11)
    c: Coincident(g16,g15)
    c: Horizontal(g16)
    c: Coincident(g17,g16)
    c: Coincident(g17,g14)
    c: Vertical(g17)
FEATURE [Part::Revolution] Revolve040  label="backCaseScrewRetainer001"
  Angle = 360
  Axis = (0,1,0)
  Base = (0,0,0)
  FaceMakerClass = Part::FaceMakerBullseye
  Placement = pos=(12.5,3,10) rot=(0,0,1;0rad)
  Solid = false
  Source = -> Face036
  Symmetric = false
FEATURE [Part::Feature] Face055
  shape: bbox 3.5 x 30.2 x 2e-07 mm, 1 faces, 0 solids (baked)
FEATURE [Part::Revolution] Revolve059  label="backCaseScrewPost"
  Angle = 360
  Axis = (0,1,0)
  Base = (0,0,0)
  FaceMakerClass = Part::FaceMakerBullseye
  Placement = pos=(12.5,4.5,10) rot=(0,0,1;0rad)
  Solid = false
  Source = -> Face055
  Symmetric = false
FEATURE [Part::Feature] Face056
  shape: bbox 3.5 x 30.2 x 2e-07 mm, 1 faces, 0 solids (baked)
FEATURE [Part::Revolution] Revolve060  label="backCaseScrewPost001"
  Angle = 360
  Axis = (0,1,0)
  Base = (0,0,0)
  FaceMakerClass = Part::FaceMakerBullseye
  Placement = pos=(12.5,4.5,62) rot=(0,0,1;0rad)
  Solid = false
  Source = -> Face056
  Symmetric = false
FEATURE [Part::Feature] Face057
  shape: bbox 3.5 x 17.8 x 2e-07 mm, 1 faces, 0 solids (baked)
FEATURE [Part::Revolution] Revolve061  label="removeToCreateScrewAndThreadedInsertHole"
  Angle = 360
  Axis = (0,1,0)
  Base = (0,0,0)
  FaceMakerClass = Part::FaceMakerBullseye
  Placement = pos=(12.5,0,10) rot=(0,0,1;0rad)
  Solid = false
  Source = -> Face057
  Symmetric = false
FEATURE [Part::Feature] Face058
  shape: bbox 3.5 x 17.8 x 2e-07 mm, 1 faces, 0 solids (baked)
FEATURE [Part::Revolution] Revolve062  label="removeToCreateScrewAndThreadedInsertHole001"
  Angle = 360
  Axis = (0,1,0)
  Base = (0,0,0)
  FaceMakerClass = Part::FaceMakerBullseye
  Placement = pos=(12.5,0,62) rot=(0,0,1;0rad)
  Solid = false
  Source = -> Face058
  Symmetric = false
FEATURE [Part::Feature] Face059
  shape: bbox 3.5 x 17.8 x 2e-07 mm, 1 faces, 0 solids (baked)
FEATURE [Part::Revolution] Revolve063  label="removeToCreateScrewAndThreadedInsertHole002"
  Angle = 360
  Axis = (0,1,0)
  Base = (0,0,0)
  FaceMakerClass = Part::FaceMakerBullseye
  Placement = pos=(89.5,0,68.5) rot=(0,0,1;0rad)
  Solid = false
  Source = -> Face059
  Symmetric = false
FEATURE [Part::Feature] Face060
  shape: bbox 3.5 x 17.8 x 2e-07 mm, 1 faces, 0 solids (baked)
FEATURE [Part::Revolution] Revolve064  label="removeToCreateScrewAndThreadedInsertHole003"
  Angle = 360
  Axis = (0,1,0)
  Base = (0,0,0)
  FaceMakerClass = Part::FaceMakerBullseye
  Placement = pos=(89.5,0,3.5) rot=(0,0,1;0rad)
  Solid = false
  Source = -> Face060
  Symmetric = false
FEATURE [Part::Feature] Face061
  shape: bbox 3.5 x 17.8 x 2e-07 mm, 1 faces, 0 solids (baked)
FEATURE [Part::Revolution] Revolve065  label="removeToCreateScrewAndThreadedInsertHole004"
  Angle = 360
  Axis = (0,1,0)
  Base = (0,0,0)
  FaceMakerClass = Part::FaceMakerBullseye
  Placement = pos=(102.5,4.7,3.5) rot=(0,0,1;0rad)
  Solid = false
  Source = -> Face061
  Symmetric = false
FEATURE [Part::Feature] Face062
  shape: bbox 3.5 x 17.8 x 2e-07 mm, 1 faces, 0 solids (baked)
FEATURE [Part::Revolution] Revolve066  label="removeToCreateScrewAndThreadedInsertHole005"
  Angle = 360
  Axis = (0,1,0)
  Base = (0,0,0)
  FaceMakerClass = Part::FaceMakerBullseye
  Placement = pos=(102.5,4.7,68.5) rot=(0,0,1;0rad)
  Solid = false
  Source = -> Face062
  Symmetric = false
FEATURE [Part::MultiFuse] Fusion047  label="makeHoles"
  Shapes = -> [Revolve066,Revolve065,Revolve064,Revolve063,Revolve062,Revolve061]
FEATURE [Part::Feature] Face063
  shape: bbox 3.6 x 3.2 x 2e-07 mm, 1 faces, 0 solids (baked)
FEATURE [Part::Revolution] Revolve067  label="moreFrontCaseScrewRetainer002"
  Angle = 360
  Axis = (0,1,0)
  Base = (0,0,0)
  FaceMakerClass = Part::FaceMakerBullseye
  Placement = pos=(102.5,4.5,68.5) rot=(0,0,1;0rad)
  Solid = false
  Source = -> Face063
  Symmetric = false
FEATURE [Part::Feature] Face064
  shape: bbox 3.6 x 3.2 x 2e-07 mm, 1 faces, 0 solids (baked)
FEATURE [Part::Revolution] Revolve068  label="moreFrontCaseScrewRetainer003"
  Angle = 360
  Axis = (0,1,0)
  Base = (0,0,0)
  FaceMakerClass = Part::FaceMakerBullseye
  Placement = pos=(102.5,4.5,3.5) rot=(0,0,1;0rad)
  Solid = false
  Source = -> Face064
  Symmetric = false
FEATURE [Part::Feature] Face065
  shape: bbox 3.5 x 17.8 x 2e-07 mm, 1 faces, 0 solids (baked)
FEATURE [Part::Revolution] Revolve069  label="removeToCreateScrewAndThreadedInsertHole006"
  Angle = 360
  Axis = (0,1,0)
  Base = (0,0,0)
  FaceMakerClass = Part::FaceMakerBullseye
  Placement = pos=(12.5,0,10) rot=(0,0,1;0rad)
  Solid = false
  Source = -> Face065
  Symmetric = false
FEATURE [Part::Feature] Face066
  shape: bbox 3.5 x 17.8 x 2e-07 mm, 1 faces, 0 solids (baked)
FEATURE [Part::Revolution] Revolve070  label="removeToCreateScrewAndThreadedInsertHole007"
  Angle = 360
  Axis = (0,1,0)
  Base = (0,0,0)
  FaceMakerClass = Part::FaceMakerBullseye
  Placement = pos=(12.5,0,62) rot=(0,0,1;0rad)
  Solid = false
  Source = -> Face066
  Symmetric = false
FEATURE [Part::Feature] Face067
  shape: bbox 3.5 x 17.8 x 2e-07 mm, 1 faces, 0 solids (baked)
FEATURE [Part::Revolution] Revolve071  label="removeToCreateScrewAndThreadedInsertHole008"
  Angle = 360
  Axis = (0,1,0)
  Base = (0,0,0)
  FaceMakerClass = Part::FaceMakerBullseye
  Placement = pos=(89.5,0,68.5) rot=(0,0,1;0rad)
  Solid = false
  Source = -> Face067
  Symmetric = false
FEATURE [Part::Feature] Face068
  shape: bbox 3.5 x 17.8 x 2e-07 mm, 1 faces, 0 solids (baked)
FEATURE [Part::Revolution] Revolve072  label="removeToCreateScrewAndThreadedInsertHole009"
  Angle = 360
  Axis = (0,1,0)
  Base = (0,0,0)
  FaceMakerClass = Part::FaceMakerBullseye
  Placement = pos=(89.5,0,3.5) rot=(0,0,1;0rad)
  Solid = false
  Source = -> Face068
  Symmetric = false
FEATURE [Part::Feature] Face069
  shape: bbox 3.5 x 17.8 x 2e-07 mm, 1 faces, 0 solids (baked)
FEATURE [Part::Feature] Face070
  shape: bbox 3.5 x 17.8 x 2e-07 mm, 1 faces, 0 solids (baked)
FEATURE [Part::Revolution] Revolve073  label="removeToCreateScrewAndThreadedInsertHole010"
  Angle = 360
  Axis = (0,1,0)
  Base = (0,0,0)
  FaceMakerClass = Part::FaceMakerBullseye
  Placement = pos=(102.5,4.7,3.5) rot=(0,0,1;0rad)
  Solid = false
  Source = -> Face069
  Symmetric = false
FEATURE [Part::Revolution] Revolve074  label="removeToCreateScrewAndThreadedInsertHole011"
  Angle = 360
  Axis = (0,1,0)
  Base = (0,0,0)
  FaceMakerClass = Part::FaceMakerBullseye
  Placement = pos=(102.5,4.7,68.5) rot=(0,0,1;0rad)
  Solid = false
  Source = -> Face070
  Symmetric = false
FEATURE [Part::MultiFuse] Fusion048  label="makeHoles001"
  Shapes = -> [Revolve074,Revolve073,Revolve072,Revolve071,Revolve070,Revolve069]
FEATURE [Part::MultiFuse] Fusion049  label="caseScrewRetainers"
  Shapes = -> [Revolve067,Revolve068,Revolve048,Revolve047,Revolve039,Revolve040]
FEATURE [Part::Cut] Cut015  label="caseScrewRetainers001"
  Base = -> Fusion049
  Tool = -> Fusion048
FEATURE [Part::MultiFuse] Fusion050  label="casePillars"
  Shapes = -> [Revolve055,Revolve054,Revolve043,Revolve046,Revolve059,Revolve060]
FEATURE [Part::Feature] Face071 .. Face076  x6 (patterned run collapsed; names and placements below)
  shape: bbox 3.5 x 17.8 x 2e-07 mm, 1 faces, 0 solids (baked)
FEATURE [Part::Revolution] Revolve075  label="removeToCreateScrewAndThreadedInsertHole012"
  Angle = 360
  Axis = (0,1,0)
  Base = (0,0,0)
  FaceMakerClass = Part::FaceMakerBullseye
  Placement = pos=(12.5,0,10) rot=(0,0,1;0rad)
  Solid = false
  Source = -> Face071
  Symmetric = false
FEATURE [Part::Revolution] Revolve076  label="removeToCreateScrewAndThreadedInsertHole013"
  Angle = 360
  Axis = (0,1,0)
  Base = (0,0,0)
  FaceMakerClass = Part::FaceMakerBullseye
  Placement = pos=(12.5,0,62) rot=(0,0,1;0rad)
  Solid = false
  Source = -> Face072
  Symmetric = false
FEATURE [Part::Revolution] Revolve077  label="removeToCreateScrewAndThreadedInsertHole014"
  Angle = 360
  Axis = (0,1,0)
  Base = (0,0,0)
  FaceMakerClass = Part::FaceMakerBullseye
  Placement = pos=(89.5,0,68.5) rot=(0,0,1;0rad)
  Solid = false
  Source = -> Face073
  Symmetric = false
FEATURE [Part::Revolution] Revolve078  label="removeToCreateScrewAndThreadedInsertHole015"
  Angle = 360
  Axis = (0,1,0)
  Base = (0,0,0)
  FaceMakerClass = Part::FaceMakerBullseye
  Placement = pos=(89.5,0,3.5) rot=(0,0,1;0rad)
  Solid = false
  Source = -> Face074
  Symmetric = false
FEATURE [Part::Revolution] Revolve079  label="removeToCreateScrewAndThreadedInsertHole016"
  Angle = 360
  Axis = (0,1,0)
  Base = (0,0,0)
  FaceMakerClass = Part::FaceMakerBullseye
  Placement = pos=(102.5,4.7,3.5) rot=(0,0,1;0rad)
  Solid = false
  Source = -> Face075
  Symmetric = false
FEATURE [Part::Revolution] Revolve080  label="removeToCreateScrewAndThreadedInsertHole017"
  Angle = 360
  Axis = (0,1,0)
  Base = (0,0,0)
  FaceMakerClass = Part::FaceMakerBullseye
  Placement = pos=(102.5,4.7,68.5) rot=(0,0,1;0rad)
  Solid = false
  Source = -> Face076
  Symmetric = false
FEATURE [Part::MultiFuse] Fusion051  label="makeHoles002"
  Shapes = -> [Revolve080,Revolve079,Revolve078,Revolve077,Revolve076,Revolve075]
FEATURE [Part::Cut] Cut016  label="caesPillars"
  Base = -> Fusion050
  Tool = -> Fusion051
FEATURE [Part::Revolution] Revolve009  label="plugHousing016"
  Angle = 360
  Axis = (0,1,0)
  Base = (0,0,0)
  FaceMakerClass = Part::FaceMakerBullseye
  Placement = pos=(0,0,36.15) rot=(0,0,1;0rad)
  Solid = false
  Source = -> Face012
  Symmetric = false
FEATURE [Part::MultiFuse] Fusion014  label="plugHousing023"
  Placement = pos=(0,0,0) rot=(0,0,1;1.5708rad)
  Shapes = -> [Revolve011,Revolve009]
FEATURE [Part::Revolution] Revolve010  label="plugHousing017"
  Angle = 360
  Axis = (0,1,0)
  Base = (0,0,0)
  FaceMakerClass = Part::FaceMakerBullseye
  Placement = pos=(0,0,36.15) rot=(0,0,1;0rad)
  Solid = false
  Source = -> Face014
  Symmetric = false
FEATURE [Part::MultiFuse] Fusion015  label="plugHousing024"
  Placement = pos=(0,0,0) rot=(0,0,1;1.5708rad)
  Shapes = -> [Revolve010,Revolve015]
FEATURE [Part::Revolution] Revolve014  label="plugHousing026"
  Angle = 360
  Axis = (0,1,0)
  Base = (0,0,0)
  FaceMakerClass = Part::FaceMakerBullseye
  Placement = pos=(0,0,36.15) rot=(0,0,1;0rad)
  Solid = false
  Source = -> Face011
  Symmetric = false
FEATURE [Part::Revolution] Revolve013  label="plugHousing025"
  Angle = 360
  Axis = (0,1,0)
  Base = (0,0,0)
  FaceMakerClass = Part::FaceMakerBullseye
  Placement = pos=(0,0,36.15) rot=(0,0,1;0rad)
  Solid = false
  Source = -> Face015
  Symmetric = false
FEATURE [Part::MultiFuse] Fusion016  label="plugHousing028"
  Placement = pos=(0,19,0) rot=(0,0,1;3.14159rad)
  Shapes = -> [Fusion014,Fusion013]
FEATURE [Part::MultiFuse] Fusion011  label="plugHousing018"
  Placement = pos=(0,0,0) rot=(0,0,1;1.5708rad)
  Shapes = -> [Revolve014,Revolve013]
FEATURE [Part::MultiFuse] Fusion012  label="plugHousing019"
  Placement = pos=(0,19,0) rot=(0,0,1;3.14159rad)
  Shapes = -> [Fusion011,Fusion015]
FEATURE [Part::MultiFuse] Fusion017  label="plugHousing029"
  Placement = pos=(122.621,0,-0.15) rot=(0,0,1;0rad)
  Shapes = -> [Fusion016,Fusion012]
FEATURE [Part::MultiFuse] Fusion052  label="casePillarRetainers"
  Shapes = -> [Extrude012,Extrude013,Extrude014,Extrude015,Extrude016,Extrude017,Extrude018,Extrude019,Box011,Box012]
FEATURE [Part::Feature] Face077
  shape: bbox 3.5 x 17.8 x 2e-07 mm, 1 faces, 0 solids (baked)
FEATURE [Part::Revolution] Revolve081  label="removeToCreateScrewAndThreadedInsertHole018"
  Angle = 360
  Axis = (0,1,0)
  Base = (0,0,0)
  FaceMakerClass = Part::FaceMakerBullseye
  Placement = pos=(62.3,30.3,19.7) rot=(0,0,1;0rad)
  Solid = false
  Source = -> Face077
  Symmetric = false
FEATURE [Part::Feature] Face078
  shape: bbox 3.5 x 17.8 x 2e-07 mm, 1 faces, 0 solids (baked)
FEATURE [Part::Revolution] Revolve082  label="removeToCreateScrewAndThreadedInsertHole019"
  Angle = 360
  Axis = (0,1,0)
  Base = (0,0,0)
  FaceMakerClass = Part::FaceMakerBullseye
  Placement = pos=(62.3,30.3,51.7) rot=(0,0,1;0rad)
  Solid = false
  Source = -> Face078
  Symmetric = false
FEATURE [Part::Feature] Face079
  shape: bbox 3.5 x 17.8 x 2e-07 mm, 1 faces, 0 solids (baked)
FEATURE [Part::Revolution] Revolve083  label="removeToCreateScrewAndThreadedInsertHole020"
  Angle = 360
  Axis = (0,1,0)
  Base = (0,0,0)
  FaceMakerClass = Part::FaceMakerBullseye
  Placement = pos=(30.3,30.3,19.7) rot=(0,0,1;0rad)
  Solid = false
  Source = -> Face079
  Symmetric = false
FEATURE [Part::Feature] Face080
  shape: bbox 3.5 x 17.8 x 2e-07 mm, 1 faces, 0 solids (baked)
FEATURE [Part::Revolution] Revolve084  label="removeToCreateScrewAndThreadedInsertHole021"
  Angle = 360
  Axis = (0,1,0)
  Base = (0,0,0)
  FaceMakerClass = Part::FaceMakerBullseye
  Placement = pos=(30.3,30.3,51.7) rot=(0,0,1;0rad)
  Solid = false
  Source = -> Face080
  Symmetric = false
FEATURE [Part::MultiFuse] Fusion053  label="createThreadedInsertHolesForFan"
  Shapes = -> [Revolve081,Revolve082,Revolve083,Revolve084]
FEATURE [Part::Cut] Cut017  label="fanScrewHousing001"
  Base = -> Fusion046
  Tool = -> Fusion053
FEATURE [Part::Feature] Face081
  shape: bbox 3.5 x 17.8 x 2e-07 mm, 1 faces, 0 solids (baked)
FEATURE [Part::Revolution] Revolve085  label="removeToCreateScrewAndThreadedInsertHole022"
  Angle = 360
  Axis = (0,1,0)
  Base = (0,0,0)
  FaceMakerClass = Part::FaceMakerBullseye
  Placement = pos=(62.3,30.3,19.7) rot=(0,0,1;0rad)
  Solid = false
  Source = -> Face081
  Symmetric = false
FEATURE [Part::Feature] Face082
  shape: bbox 3.5 x 17.8 x 2e-07 mm, 1 faces, 0 solids (baked)
FEATURE [Part::Revolution] Revolve086  label="removeToCreateScrewAndThreadedInsertHole023"
  Angle = 360
  Axis = (0,1,0)
  Base = (0,0,0)
  FaceMakerClass = Part::FaceMakerBullseye
  Placement = pos=(62.3,30.3,51.7) rot=(0,0,1;0rad)
  Solid = false
  Source = -> Face082
  Symmetric = false
FEATURE [Part::Feature] Face083
  shape: bbox 3.5 x 17.8 x 2e-07 mm, 1 faces, 0 solids (baked)
FEATURE [Part::Revolution] Revolve087  label="removeToCreateScrewAndThreadedInsertHole024"
  Angle = 360
  Axis = (0,1,0)
  Base = (0,0,0)
  FaceMakerClass = Part::FaceMakerBullseye
  Placement = pos=(30.3,30.3,19.7) rot=(0,0,1;0rad)
  Solid = false
  Source = -> Face083
  Symmetric = false
FEATURE [Part::Feature] Face084
  shape: bbox 3.5 x 17.8 x 2e-07 mm, 1 faces, 0 solids (baked)
FEATURE [Part::Revolution] Revolve088  label="removeToCreateScrewAndThreadedInsertHole025"
  Angle = 360
  Axis = (0,1,0)
  Base = (0,0,0)
  FaceMakerClass = Part::FaceMakerBullseye
  Placement = pos=(30.3,30.3,51.7) rot=(0,0,1;0rad)
  Solid = false
  Source = -> Face084
  Symmetric = false
FEATURE [Part::MultiFuse] Fusion054  label="createThreadedInsertHolesForFan001"
  Shapes = -> [Revolve085,Revolve086,Revolve087,Revolve088]
FEATURE [Part::Cut] Cut018  label="top007"
  Base = -> Fusion040
  Tool = -> Fusion054
FEATURE [Sketcher::SketchObject] Sketch029
  FullyConstrained = false
  Placement = pos=(0,0,0) rot=(1,0,0;1.5708rad)
  sketch-geometry (24):
    g0: ArcOfCircle CenterX=-4 CenterY=-10.5 CenterZ=0 NormalX=0 NormalY=0 NormalZ=1 AngleXU=0 Radius=1.5 StartAngle=6e-16 EndAngle=3.14159
    g1: ArcOfCircle CenterX=-34.2 CenterY=-10.5 CenterZ=0 NormalX=0 NormalY=0 NormalZ=1 AngleXU=0 Radius=1.5 StartAngle=0 EndAngle=3.14159
    g2: ArcOfCircle CenterX=-34.2 CenterY=-27.7 CenterZ=0 NormalX=0 NormalY=0 NormalZ=1 AngleXU=0 Radius=1.5 StartAngle=3.14159 EndAngle=6.28319
    g3: ArcOfCircle CenterX=-4 CenterY=-27.7 CenterZ=0 NormalX=0 NormalY=0 NormalZ=1 AngleXU=0 Radius=1.5 StartAngle=3.1416 EndAngle=6.28319
    g4: ArcOfCircle CenterX=-10 CenterY=-4.3 CenterZ=0 NormalX=0 NormalY=0 NormalZ=1 AngleXU=0 Radius=1.5 StartAngle=2e-16 EndAngle=3.14159
    g5: ArcOfCircle CenterX=-16.1 CenterY=-1.8 CenterZ=0 NormalX=0 NormalY=0 NormalZ=1 AngleXU=0 Radius=1.5 StartAngle=5e-16 EndAngle=3.14159
    g6: ArcOfCircle CenterX=-22.1 CenterY=-1.8 CenterZ=0 NormalX=0 NormalY=0 NormalZ=1 AngleXU=0 Radius=1.5 StartAngle=5e-16 EndAngle=3.14159
    g7: ArcOfCircle CenterX=-28.2 CenterY=-4.3 CenterZ=0 NormalX=0 NormalY=0 NormalZ=1 AngleXU=0 Radius=1.5 StartAngle=2e-16 EndAngle=3.14159
    g8: ArcOfCircle CenterX=-10 CenterY=-33.9 CenterZ=0 NormalX=0 NormalY=0 NormalZ=1 AngleXU=0 Radius=1.5 StartAngle=3.14159 EndAngle=6.28319
    g9: ArcOfCircle CenterX=-16.1 CenterY=-36.4 CenterZ=0 NormalX=0 NormalY=0 NormalZ=1 AngleXU=0 Radius=1.5 StartAngle=3.14159 EndAngle=6.28319
    g10: ArcOfCircle CenterX=-22.1 CenterY=-36.4 CenterZ=0 NormalX=0 NormalY=0 NormalZ=1 AngleXU=0 Radius=1.5 StartAngle=3.14159 EndAngle=6.28319
    g11: ArcOfCircle CenterX=-28.2 CenterY=-33.9 CenterZ=0 NormalX=0 NormalY=0 NormalZ=1 AngleXU=0 Radius=1.5 StartAngle=3.14159 EndAngle=6.28319
    g12: LineSegment StartX=-35.7 StartY=-10.5 StartZ=0 EndX=-35.7 EndY=-27.7 EndZ=0
    g13: LineSegment StartX=-32.7 StartY=-10.5 StartZ=0 EndX=-32.7 EndY=-27.7 EndZ=0
    g14: LineSegment StartX=-29.7 StartY=-33.9 StartZ=0 EndX=-29.7 EndY=-4.3 EndZ=0
    g15: LineSegment StartX=-26.7 StartY=-33.9 StartZ=0 EndX=-26.7 EndY=-4.3 EndZ=0
    g16: LineSegment StartX=-2.5 StartY=-10.5 StartZ=0 EndX=-2.5 EndY=-27.7 EndZ=0
    g17: LineSegment StartX=-8.5 StartY=-4.3 StartZ=0 EndX=-8.5 EndY=-33.9 EndZ=0
    g18: LineSegment StartX=-5.5 StartY=-10.5 StartZ=0 EndX=-5.5 EndY=-27.7 EndZ=0
    g19: LineSegment StartX=-11.5 StartY=-4.3 StartZ=0 EndX=-11.5 EndY=-33.9 EndZ=0
    g20: LineSegment StartX=-14.6 StartY=-1.8 StartZ=0 EndX=-14.6 EndY=-36.4 EndZ=0
    g21: LineSegment StartX=-17.6 StartY=-1.8 StartZ=0 EndX=-17.6 EndY=-36.4 EndZ=0
    g22: LineSegment StartX=-20.6 StartY=-36.4 StartZ=0 EndX=-20.6 EndY=-1.8 EndZ=0
    g23: LineSegment StartX=-23.6 StartY=-1.8 StartZ=0 EndX=-23.6 EndY=-36.4 EndZ=0
  constraints (48):
    c: Block(g0)
    c: Block(g1)
    c: Block(g2)
    c: Block(g3)
    c: Block(g4)
    c: Block(g5)
    c: Block(g6)
    c: Block(g7)
    c: Block(g8)
    c: Block(g9)
    c: Block(g10)
    c: Block(g11)
    c: Coincident(g12,g1)
    c: Coincident(g12,g2)
    c: Vertical(g12)
    c: Coincident(g13,g1)
    c: Coincident(g13,g2)
    c: Vertical(g13)
    c: Coincident(g14,g11)
    c: Coincident(g14,g7)
    c: Vertical(g14)
    c: Coincident(g15,g11)
    c: Coincident(g15,g7)
    c: Vertical(g15)
    c: Coincident(g16,g0)
    c: Coincident(g16,g3)
    c: Vertical(g16)
    c: Coincident(g17,g4)
    c: Coincident(g17,g8)
    c: Vertical(g17)
    c: Coincident(g18,g0)
    c: Coincident(g18,g3)
    c: Vertical(g18)
    c: Coincident(g19,g4)
    c: Coincident(g19,g8)
    c: Vertical(g19)
    c: Coincident(g20,g5)
    c: Coincident(g20,g9)
    c: Vertical(g20)
    c: Coincident(g21,g5)
    c: Coincident(g21,g9)
    c: Vertical(g21)
    c: Coincident(g22,g10)
    c: Coincident(g22,g6)
    c: Vertical(g22)
    c: Coincident(g23,g6)
    c: Coincident(g23,g10)
    c: Vertical(g23)
FEATURE [Part::Extrusion] Extrude020  label="removeToCreateFanGrillHoles"
  Base = -> Sketch029
  Dir = (0,-1,6e-16)
  DirMode = 2
  FaceMakerClass = Part::FaceMakerBullseye
  LengthFwd = 10
  LengthRev = 0
  Placement = pos=(65.4,44,54.82) rot=(0,0,1;0rad)
  Solid = true
  Symmetric = false
FEATURE [Part::MultiFuse] Fusion055  label="top008"
  Shapes = -> [Cut017,Cut018]
FEATURE [Part::Cut] Cut019  label="top009"
  Base = -> Fusion055
  Tool = -> Extrude020
FEATURE [App::MeasureDistance] Distance003  label="Distance: 71.95 mm"
  Distance = 71.9513
  P1 = (117,38,72)
  P2 = (117,38,0.0487319)
FEATURE [Sketcher::SketchObject] Sketch030
  FullyConstrained = true
  Placement = pos=(117,19,0) rot=(0.57735,0.57735,0.57735;2.0944rad)
  sketch-geometry (48):
    g0: LineSegment StartX=-49.19 StartY=69.25 StartZ=0 EndX=-49.19 EndY=66.25 EndZ=0
    g1: LineSegment StartX=-49.19 StartY=63.5 StartZ=0 EndX=-49.19 EndY=60.5 EndZ=0
    g2: LineSegment StartX=-49.19 StartY=57.75 StartZ=0 EndX=-49.19 EndY=54.75 EndZ=0
    g3: LineSegment StartX=-49.19 StartY=52 StartZ=0 EndX=-49.19 EndY=49 EndZ=0
    g4: LineSegment StartX=-49.19 StartY=46.25 StartZ=0 EndX=-49.19 EndY=43.25 EndZ=0
    g5: LineSegment StartX=-49.19 StartY=40.5 StartZ=0 EndX=-49.19 EndY=37.5 EndZ=0
    g6: LineSegment StartX=-49.19 StartY=34.5 StartZ=0 EndX=-49.19 EndY=31.5 EndZ=0
    g7: LineSegment StartX=-49.19 StartY=28.75 StartZ=0 EndX=-49.19 EndY=25.75 EndZ=0
    g8: LineSegment StartX=-49.19 StartY=23 StartZ=0 EndX=-49.19 EndY=20 EndZ=0
    g9: LineSegment StartX=-49.19 StartY=17.25 StartZ=0 EndX=-49.19 EndY=14.25 EndZ=0
    g10: LineSegment StartX=-49.19 StartY=11.5 StartZ=0 EndX=-49.19 EndY=8.5 EndZ=0
    g11: LineSegment StartX=-49.19 StartY=5.75 StartZ=0 EndX=-49.19 EndY=2.75 EndZ=0
    g12: ArcOfCircle CenterX=-1.5 CenterY=67.75 CenterZ=0 NormalX=0 NormalY=0 NormalZ=1 AngleXU=0 Radius=1.5 StartAngle=4.71239 EndAngle=7.85398
    g13: ArcOfCircle CenterX=-1.5 CenterY=62 CenterZ=0 NormalX=0 NormalY=0 NormalZ=1 AngleXU=0 Radius=1.5 StartAngle=4.71239 EndAngle=7.85398
    g14: ArcOfCircle CenterX=-1.5 CenterY=56.25 CenterZ=0 NormalX=0 NormalY=0 NormalZ=1 AngleXU=0 Radius=1.5 StartAngle=4.71239 EndAngle=7.85398
    g15: ArcOfCircle CenterX=-11.49 CenterY=50.5 CenterZ=0 NormalX=0 NormalY=0 NormalZ=1 AngleXU=0 Radius=1.5 StartAngle=4.71239 EndAngle=7.85398
    g16: ArcOfCircle CenterX=-16.28 CenterY=44.75 CenterZ=0 NormalX=0 NormalY=0 NormalZ=1 AngleXU=0 Radius=1.5 StartAngle=4.71239 EndAngle=7.85398
    g17: ArcOfCircle CenterX=-18.2337 CenterY=39 CenterZ=0 NormalX=0 NormalY=0 NormalZ=1 AngleXU=0 Radius=1.5 StartAngle=4.71485 EndAngle=7.85398
    g18: ArcOfCircle CenterX=-16.2837 CenterY=27.25 CenterZ=0 NormalX=0 NormalY=0 NormalZ=1 AngleXU=0 Radius=1.5 StartAngle=4.71485 EndAngle=7.85398
    g19: ArcOfCircle CenterX=-18.2337 CenterY=33 CenterZ=0 NormalX=0 NormalY=0 NormalZ=1 AngleXU=0 Radius=1.5 StartAngle=4.71485 EndAngle=7.85398
    g20: ArcOfCircle CenterX=-11.49 CenterY=21.5 CenterZ=0 NormalX=0 NormalY=0 NormalZ=1 AngleXU=0 Radius=1.5 StartAngle=4.71239 EndAngle=7.85398
    g21: ArcOfCircle CenterX=-1.5 CenterY=4.25 CenterZ=0 NormalX=0 NormalY=0 NormalZ=1 AngleXU=0 Radius=1.5 StartAngle=4.71239 EndAngle=7.85398
    g22: ArcOfCircle CenterX=-1.5 CenterY=10 CenterZ=0 NormalX=0 NormalY=0 NormalZ=1 AngleXU=0 Radius=1.5 StartAngle=4.71239 EndAngle=7.85398
    g23: ArcOfCircle CenterX=-1.5 CenterY=15.75 CenterZ=0 NormalX=0 NormalY=0 NormalZ=1 AngleXU=0 Radius=1.5 StartAngle=4.71239 EndAngle=7.85398
    g24: LineSegment StartX=-49.19 StartY=69.25 StartZ=0 EndX=-1.5 EndY=69.25 EndZ=0
    g25: LineSegment StartX=-49.19 StartY=66.25 StartZ=0 EndX=-1.5 EndY=66.25 EndZ=0
    g26: LineSegment StartX=-49.19 StartY=63.5 StartZ=0 EndX=-1.5 EndY=63.5 EndZ=0
    g27: LineSegment StartX=-49.19 StartY=60.5 StartZ=0 EndX=-1.5 EndY=60.5 EndZ=0
    g28: LineSegment StartX=-49.19 StartY=57.75 StartZ=0 EndX=-1.5 EndY=57.75 EndZ=0
    g29: LineSegment StartX=-49.19 StartY=54.75 StartZ=0 EndX=-1.5 EndY=54.75 EndZ=0
    g30: LineSegment StartX=-49.19 StartY=52 StartZ=0 EndX=-11.49 EndY=52 EndZ=0
    g31: LineSegment StartX=-49.19 StartY=49 StartZ=0 EndX=-11.49 EndY=49 EndZ=0
    g32: LineSegment StartX=-49.19 StartY=46.25 StartZ=0 EndX=-16.28 EndY=46.25 EndZ=0
    g33: LineSegment StartX=-49.19 StartY=43.25 StartZ=0 EndX=-16.28 EndY=43.25 EndZ=0
    g34: LineSegment StartX=-49.19 StartY=40.5 StartZ=0 EndX=-18.2337 EndY=40.5 EndZ=0
    g35: LineSegment StartX=-49.19 StartY=37.5 StartZ=0 EndX=-18.23 EndY=37.5 EndZ=0
    g36: LineSegment StartX=-49.19 StartY=34.5 StartZ=0 EndX=-18.2337 EndY=34.5 EndZ=0
    g37: LineSegment StartX=-49.19 StartY=31.5 StartZ=0 EndX=-18.23 EndY=31.5 EndZ=0
    g38: LineSegment StartX=-49.19 StartY=28.75 StartZ=0 EndX=-16.2837 EndY=28.75 EndZ=0
    g39: LineSegment StartX=-49.19 StartY=25.75 StartZ=0 EndX=-16.28 EndY=25.75 EndZ=0
    g40: LineSegment StartX=-49.19 StartY=23 StartZ=0 EndX=-11.49 EndY=23 EndZ=0
    g41: LineSegment StartX=-49.19 StartY=20 StartZ=0 EndX=-11.49 EndY=20 EndZ=0
    g42: LineSegment StartX=-49.19 StartY=17.25 StartZ=0 EndX=-1.5 EndY=17.25 EndZ=0
    g43: LineSegment StartX=-49.19 StartY=14.25 StartZ=0 EndX=-1.5 EndY=14.25 EndZ=0
    g44: LineSegment StartX=-49.19 StartY=11.5 StartZ=0 EndX=-1.5 EndY=11.5 EndZ=0
    g45: LineSegment StartX=-49.19 StartY=8.5 StartZ=0 EndX=-1.5 EndY=8.5 EndZ=0
    g46: LineSegment StartX=-49.19 StartY=5.75 StartZ=0 EndX=-1.5 EndY=5.75 EndZ=0
    g47: LineSegment StartX=-49.19 StartY=2.75 StartZ=0 EndX=-1.5 EndY=2.75 EndZ=0
  constraints (120):
    c: Vertical(g0)
    c: Distance(g0) = 3
    c: Block(g0)
    c: Vertical(g1)
    c: Distance(g1) = 3
    c: Vertical(g2)
    c: Equal(g0,g2) = 3
    c: Block(g2)
    c: Vertical(g3)
    c: Equal(g1,g3) = 3
    c: Vertical(g4)
    c: Equal(g0,g4) = 3
    c: Block(g4)
    c: Vertical(g5)
    c: Equal(g1,g5) = 3
    c: Vertical(g6)
    c: Equal(g0,g6) = 3
    c: Block(g6)
    c: Vertical(g7)
    c: Equal(g1,g7) = 3
    c: Vertical(g8)
    c: Equal(g0,g8) = 3
    c: Block(g8)
    c: Vertical(g9)
    c: Equal(g1,g9) = 3
    c: Vertical(g10)
    c: Equal(g0,g10) = 3
    c: Block(g10)
    c: Vertical(g11)
    c: Equal(g1,g11) = 3
    c: Block(g12)
    c: Block(g13)
    c: Block(g14)
    c: Block(g15)
    c: Block(g16)
    c: Block(g17)
    c: Block(g18)
    c: Block(g19)
    c: Block(g20)
    c: Block(g21)
    c: Block(g22)
    c: Block(g23)
    c: Block(g11)
    c: Block(g9)
    c: Block(g7)
    c: Block(g5)
    c: Block(g3)
    c: Block(g1)
    c: Coincident(g24,g0)
    c: Coincident(g24,g12)
    c: Horizontal(g24)
    c: Coincident(g25,g0)
    c: Coincident(g25,g12)
    c: Horizontal(g25)
    c: Coincident(g26,g1)
    c: Coincident(g26,g13)
    c: Horizontal(g26)
    c: Coincident(g27,g1)
    c: Coincident(g27,g13)
    c: Horizontal(g27)
    c: Coincident(g28,g2)
    c: Coincident(g28,g14)
    c: Horizontal(g28)
    c: Coincident(g29,g2)
    c: Coincident(g29,g14)
    c: Horizontal(g29)
    c: Coincident(g30,g3)
    c: Coincident(g30,g15)
    c: Horizontal(g30)
    c: Coincident(g31,g3)
    c: Coincident(g31,g15)
    c: Horizontal(g31)
    c: Coincident(g32,g4)
    c: Coincident(g32,g16)
    c: Horizontal(g32)
    c: Coincident(g33,g4)
    c: Coincident(g33,g16)
    c: Horizontal(g33)
    c: Coincident(g34,g5)
    c: Coincident(g34,g17)
    c: Horizontal(g34)
    c: Coincident(g35,g5)
    c: Coincident(g35,g17)
    c: Horizontal(g35)
    c: Coincident(g36,g6)
    c: Coincident(g36,g19)
    c: Horizontal(g36)
    c: Coincident(g37,g6)
    c: Coincident(g37,g19)
    c: Horizontal(g37)
    c: Coincident(g38,g7)
    c: Coincident(g38,g18)
    c: Horizontal(g38)
    c: Coincident(g39,g7)
    c: Coincident(g39,g18)
    c: Horizontal(g39)
    c: Coincident(g40,g8)
    c: Coincident(g40,g20)
    c: Horizontal(g40)
    c: Coincident(g41,g8)
    c: Coincident(g41,g20)
    c: Horizontal(g41)
    c: Coincident(g42,g9)
    c: Coincident(g42,g23)
    c: Horizontal(g42)
    c: Coincident(g43,g9)
    c: Coincident(g43,g23)
    c: Horizontal(g43)
    c: Coincident(g44,g10)
    c: Coincident(g44,g22)
    c: Horizontal(g44)
    c: Coincident(g45,g10)
    c: Coincident(g45,g22)
    c: Horizontal(g45)
    c: Coincident(g46,g11)
    c: Coincident(g46,g21)
    c: Horizontal(g46)
    c: Coincident(g47,g11)
    c: Coincident(g47,g21)
    c: Horizontal(g47)
FEATURE [Sketcher::SketchObject] Sketch031
  FullyConstrained = true
  Placement = pos=(117,19,0) rot=(0.57735,0.57735,0.57735;2.0944rad)
  sketch-geometry (24):
    g0: ArcOfCircle CenterX=-49.19 CenterY=67.75 CenterZ=0 NormalX=0 NormalY=0 NormalZ=1 AngleXU=0 Radius=1.5 StartAngle=1.5708 EndAngle=4.71239
    g1: ArcOfCircle CenterX=-49.19 CenterY=62 CenterZ=0 NormalX=0 NormalY=0 NormalZ=1 AngleXU=0 Radius=1.5 StartAngle=1.5708 EndAngle=4.71239
    g2: ArcOfCircle CenterX=-49.19 CenterY=56.25 CenterZ=0 NormalX=0 NormalY=0 NormalZ=1 AngleXU=0 Radius=1.5 StartAngle=1.5708 EndAngle=4.71239
    g3: ArcOfCircle CenterX=-49.19 CenterY=50.5 CenterZ=0 NormalX=0 NormalY=0 NormalZ=1 AngleXU=0 Radius=1.5 StartAngle=1.5708 EndAngle=4.71239
    g4: ArcOfCircle CenterX=-49.19 CenterY=44.75 CenterZ=0 NormalX=0 NormalY=0 NormalZ=1 AngleXU=0 Radius=1.5 StartAngle=1.5708 EndAngle=4.71239
    g5: ArcOfCircle CenterX=-49.19 CenterY=39 CenterZ=0 NormalX=0 NormalY=0 NormalZ=1 AngleXU=0 Radius=1.5 StartAngle=1.5708 EndAngle=4.71239
    g6: ArcOfCircle CenterX=-49.19 CenterY=33 CenterZ=0 NormalX=0 NormalY=0 NormalZ=1 AngleXU=0 Radius=1.5 StartAngle=1.5708 EndAngle=4.71239
    g7: ArcOfCircle CenterX=-49.19 CenterY=27.25 CenterZ=0 NormalX=0 NormalY=0 NormalZ=1 AngleXU=0 Radius=1.5 StartAngle=1.5708 EndAngle=4.71239
    g8: ArcOfCircle CenterX=-49.19 CenterY=21.5 CenterZ=0 NormalX=0 NormalY=0 NormalZ=1 AngleXU=0 Radius=1.5 StartAngle=1.5708 EndAngle=4.71239
    g9: ArcOfCircle CenterX=-49.19 CenterY=15.75 CenterZ=0 NormalX=0 NormalY=0 NormalZ=1 AngleXU=0 Radius=1.5 StartAngle=1.5708 EndAngle=4.71239
    g10: ArcOfCircle CenterX=-49.19 CenterY=10 CenterZ=0 NormalX=0 NormalY=0 NormalZ=1 AngleXU=0 Radius=1.5 StartAngle=1.5708 EndAngle=4.71239
    g11: ArcOfCircle CenterX=-49.19 CenterY=4.25 CenterZ=0 NormalX=0 NormalY=0 NormalZ=1 AngleXU=0 Radius=1.5 StartAngle=1.5708 EndAngle=4.71239
    g12: LineSegment StartX=-49.19 StartY=69.25 StartZ=0 EndX=-49.19 EndY=66.25 EndZ=0
    g13: LineSegment StartX=-49.19 StartY=63.5 StartZ=0 EndX=-49.19 EndY=60.5 EndZ=0
    g14: LineSegment StartX=-49.19 StartY=57.75 StartZ=0 EndX=-49.19 EndY=54.75 EndZ=0
    g15: LineSegment StartX=-49.19 StartY=52 StartZ=0 EndX=-49.19 EndY=49 EndZ=0
    g16: LineSegment StartX=-49.19 StartY=46.25 StartZ=0 EndX=-49.19 EndY=43.25 EndZ=0
    g17: LineSegment StartX=-49.19 StartY=40.5 StartZ=0 EndX=-49.19 EndY=37.5 EndZ=0
    g18: LineSegment StartX=-49.19 StartY=34.5 StartZ=0 EndX=-49.19 EndY=31.5 EndZ=0
    g19: LineSegment StartX=-49.19 StartY=28.75 StartZ=0 EndX=-49.19 EndY=25.75 EndZ=0
    g20: LineSegment StartX=-49.19 StartY=23 StartZ=0 EndX=-49.19 EndY=20 EndZ=0
    g21: LineSegment StartX=-49.19 StartY=17.25 StartZ=0 EndX=-49.19 EndY=14.25 EndZ=0
    g22: LineSegment StartX=-49.19 StartY=11.5 StartZ=0 EndX=-49.19 EndY=8.5 EndZ=0
    g23: LineSegment StartX=-49.19 StartY=5.75 StartZ=0 EndX=-49.19 EndY=2.75 EndZ=0
  constraints (48):
    c: Block(g0)
    c: Block(g1)
    c: Block(g2)
    c: Block(g3)
    c: Block(g4)
    c: Block(g5)
    c: Block(g6)
    c: Block(g7)
    c: Block(g8)
    c: Block(g9)
    c: Block(g10)
    c: Block(g11)
    c: Coincident(g12,g0)
    c: Coincident(g12,g0)
    c: Vertical(g12)
    c: Vertical(g13)
    c: Coincident(g13,g1)
    c: Vertical(g14)
    c: Coincident(g14,g2)
    c: Vertical(g15)
    c: Coincident(g15,g3)
    c: Vertical(g16)
    c: Coincident(g16,g4)
    c: Vertical(g17)
    c: Coincident(g17,g5)
    c: Vertical(g18)
    c: Coincident(g18,g6)
    c: Vertical(g19)
    c: Coincident(g19,g7)
    c: Vertical(g20)
    c: Coincident(g20,g8)
    c: Vertical(g21)
    c: Coincident(g21,g9)
    c: Vertical(g22)
    c: Coincident(g22,g10)
    c: Vertical(g23)
    c: Coincident(g23,g11)
    c: Block(g23)
    c: Block(g22)
    c: Block(g21)
    c: Block(g20)
    c: Block(g13)
    c: Block(g14)
    c: Block(g15)
    c: Block(g16)
    c: Block(g17)
    c: Block(g18)
    c: Block(g19)
FEATURE [Part::Extrusion] Extrude022
  Base = -> Sketch030
  Dir = (1,-2e-16,2e-16)
  DirMode = 2
  FaceMakerClass = Part::FaceMakerBullseye
  LengthFwd = 19
  LengthRev = 0
  Placement = pos=(-19,0,0) rot=(0,0,1;0rad)
  Solid = true
  Symmetric = false
FEATURE [Part::Fillet] Fillet022
  Base = -> Extrude022
  Edges = 24 edges r=1.49: [Edge6,Edge11,Edge18,Edge23,Edge30,Edge35,Edge42,Edge47,Edge54,Edge59,Edge66,Edge71,Edge78,Edge83,Edge90,Edge95,Edge102,Edge107,Edge114,Edge119,Edge126,Edge131,Edge138,Edge143]
FEATURE [Part::Cut] Cut020  label="top010"
  Base = -> Cut019
  Tool = -> Fillet022
FEATURE [Sketcher::SketchObject] Sketch032
  FullyConstrained = true
  Placement = pos=(117,19,0) rot=(0.57735,0.57735,0.57735;2.0944rad)
  sketch-geometry (48):
    g0: LineSegment StartX=-49.19 StartY=69.25 StartZ=0 EndX=-49.19 EndY=66.25 EndZ=0
    g1: LineSegment StartX=-49.19 StartY=63.5 StartZ=0 EndX=-49.19 EndY=60.5 EndZ=0
    g2: LineSegment StartX=-49.19 StartY=57.75 StartZ=0 EndX=-49.19 EndY=54.75 EndZ=0
    g3: LineSegment StartX=-49.19 StartY=52 StartZ=0 EndX=-49.19 EndY=49 EndZ=0
    g4: LineSegment StartX=-49.19 StartY=46.25 StartZ=0 EndX=-49.19 EndY=43.25 EndZ=0
    g5: LineSegment StartX=-49.19 StartY=40.5 StartZ=0 EndX=-49.19 EndY=37.5 EndZ=0
    g6: LineSegment StartX=-49.19 StartY=34.5 StartZ=0 EndX=-49.19 EndY=31.5 EndZ=0
    g7: LineSegment StartX=-49.19 StartY=28.75 StartZ=0 EndX=-49.19 EndY=25.75 EndZ=0
    g8: LineSegment StartX=-49.19 StartY=23 StartZ=0 EndX=-49.19 EndY=20 EndZ=0
    g9: LineSegment StartX=-49.19 StartY=17.25 StartZ=0 EndX=-49.19 EndY=14.25 EndZ=0
    g10: LineSegment StartX=-49.19 StartY=11.5 StartZ=0 EndX=-49.19 EndY=8.5 EndZ=0
    g11: LineSegment StartX=-49.19 StartY=5.75 StartZ=0 EndX=-49.19 EndY=2.75 EndZ=0
    g12: ArcOfCircle CenterX=-1.5 CenterY=67.75 CenterZ=0 NormalX=0 NormalY=0 NormalZ=1 AngleXU=0 Radius=1.5 StartAngle=4.71239 EndAngle=7.85398
    g13: ArcOfCircle CenterX=-1.5 CenterY=62 CenterZ=0 NormalX=0 NormalY=0 NormalZ=1 AngleXU=0 Radius=1.5 StartAngle=4.71239 EndAngle=7.85398
    g14: ArcOfCircle CenterX=-1.5 CenterY=56.25 CenterZ=0 NormalX=0 NormalY=0 NormalZ=1 AngleXU=0 Radius=1.5 StartAngle=4.71239 EndAngle=7.85398
    g15: ArcOfCircle CenterX=-11.49 CenterY=50.5 CenterZ=0 NormalX=0 NormalY=0 NormalZ=1 AngleXU=0 Radius=1.5 StartAngle=4.71239 EndAngle=7.85398
    g16: ArcOfCircle CenterX=-16.28 CenterY=44.75 CenterZ=0 NormalX=0 NormalY=0 NormalZ=1 AngleXU=0 Radius=1.5 StartAngle=4.71239 EndAngle=7.85398
    g17: ArcOfCircle CenterX=-18.2337 CenterY=39 CenterZ=0 NormalX=0 NormalY=0 NormalZ=1 AngleXU=0 Radius=1.5 StartAngle=4.71485 EndAngle=7.85398
    g18: ArcOfCircle CenterX=-16.2837 CenterY=27.25 CenterZ=0 NormalX=0 NormalY=0 NormalZ=1 AngleXU=0 Radius=1.5 StartAngle=4.71485 EndAngle=7.85398
    g19: ArcOfCircle CenterX=-18.2337 CenterY=33 CenterZ=0 NormalX=0 NormalY=0 NormalZ=1 AngleXU=0 Radius=1.5 StartAngle=4.71485 EndAngle=7.85398
    g20: ArcOfCircle CenterX=-11.49 CenterY=21.5 CenterZ=0 NormalX=0 NormalY=0 NormalZ=1 AngleXU=0 Radius=1.5 StartAngle=4.71239 EndAngle=7.85398
    g21: ArcOfCircle CenterX=-1.5 CenterY=4.25 CenterZ=0 NormalX=0 NormalY=0 NormalZ=1 AngleXU=0 Radius=1.5 StartAngle=4.71239 EndAngle=7.85398
    g22: ArcOfCircle CenterX=-1.5 CenterY=10 CenterZ=0 NormalX=0 NormalY=0 NormalZ=1 AngleXU=0 Radius=1.5 StartAngle=4.71239 EndAngle=7.85398
    g23: ArcOfCircle CenterX=-1.5 CenterY=15.75 CenterZ=0 NormalX=0 NormalY=0 NormalZ=1 AngleXU=0 Radius=1.5 StartAngle=4.71239 EndAngle=7.85398
    g24: LineSegment StartX=-49.19 StartY=69.25 StartZ=0 EndX=-1.5 EndY=69.25 EndZ=0
    g25: LineSegment StartX=-49.19 StartY=66.25 StartZ=0 EndX=-1.5 EndY=66.25 EndZ=0
    g26: LineSegment StartX=-49.19 StartY=63.5 StartZ=0 EndX=-1.5 EndY=63.5 EndZ=0
    g27: LineSegment StartX=-49.19 StartY=60.5 StartZ=0 EndX=-1.5 EndY=60.5 EndZ=0
    g28: LineSegment StartX=-49.19 StartY=57.75 StartZ=0 EndX=-1.5 EndY=57.75 EndZ=0
    g29: LineSegment StartX=-49.19 StartY=54.75 StartZ=0 EndX=-1.5 EndY=54.75 EndZ=0
    g30: LineSegment StartX=-49.19 StartY=52 StartZ=0 EndX=-11.49 EndY=52 EndZ=0
    g31: LineSegment StartX=-49.19 StartY=49 StartZ=0 EndX=-11.49 EndY=49 EndZ=0
    g32: LineSegment StartX=-49.19 StartY=46.25 StartZ=0 EndX=-16.28 EndY=46.25 EndZ=0
    g33: LineSegment StartX=-49.19 StartY=43.25 StartZ=0 EndX=-16.28 EndY=43.25 EndZ=0
    g34: LineSegment StartX=-49.19 StartY=40.5 StartZ=0 EndX=-18.2337 EndY=40.5 EndZ=0
    g35: LineSegment StartX=-49.19 StartY=37.5 StartZ=0 EndX=-18.23 EndY=37.5 EndZ=0
    g36: LineSegment StartX=-49.19 StartY=34.5 StartZ=0 EndX=-18.2337 EndY=34.5 EndZ=0
    g37: LineSegment StartX=-49.19 StartY=31.5 StartZ=0 EndX=-18.23 EndY=31.5 EndZ=0
    g38: LineSegment StartX=-49.19 StartY=28.75 StartZ=0 EndX=-16.2837 EndY=28.75 EndZ=0
    g39: LineSegment StartX=-49.19 StartY=25.75 StartZ=0 EndX=-16.28 EndY=25.75 EndZ=0
    g40: LineSegment StartX=-49.19 StartY=23 StartZ=0 EndX=-11.49 EndY=23 EndZ=0
    g41: LineSegment StartX=-49.19 StartY=20 StartZ=0 EndX=-11.49 EndY=20 EndZ=0
    g42: LineSegment StartX=-49.19 StartY=17.25 StartZ=0 EndX=-1.5 EndY=17.25 EndZ=0
    g43: LineSegment StartX=-49.19 StartY=14.25 StartZ=0 EndX=-1.5 EndY=14.25 EndZ=0
    g44: LineSegment StartX=-49.19 StartY=11.5 StartZ=0 EndX=-1.5 EndY=11.5 EndZ=0
    g45: LineSegment StartX=-49.19 StartY=8.5 StartZ=0 EndX=-1.5 EndY=8.5 EndZ=0
    g46: LineSegment StartX=-49.19 StartY=5.75 StartZ=0 EndX=-1.5 EndY=5.75 EndZ=0
    g47: LineSegment StartX=-49.19 StartY=2.75 StartZ=0 EndX=-1.5 EndY=2.75 EndZ=0
  constraints (120):
    c: Vertical(g0)
    c: Distance(g0) = 3
    c: Block(g0)
    c: Vertical(g1)
    c: Distance(g1) = 3
    c: Vertical(g2)
    c: Equal(g0,g2) = 3
    c: Block(g2)
    c: Vertical(g3)
    c: Equal(g1,g3) = 3
    c: Vertical(g4)
    c: Equal(g0,g4) = 3
    c: Block(g4)
    c: Vertical(g5)
    c: Equal(g1,g5) = 3
    c: Vertical(g6)
    c: Equal(g0,g6) = 3
    c: Block(g6)
    c: Vertical(g7)
    c: Equal(g1,g7) = 3
    c: Vertical(g8)
    c: Equal(g0,g8) = 3
    c: Block(g8)
    c: Vertical(g9)
    c: Equal(g1,g9) = 3
    c: Vertical(g10)
    c: Equal(g0,g10) = 3
    c: Block(g10)
    c: Vertical(g11)
    c: Equal(g1,g11) = 3
    c: Block(g12)
    c: Block(g13)
    c: Block(g14)
    c: Block(g15)
    c: Block(g16)
    c: Block(g17)
    c: Block(g18)
    c: Block(g19)
    c: Block(g20)
    c: Block(g21)
    c: Block(g22)
    c: Block(g23)
    c: Block(g11)
    c: Block(g9)
    c: Block(g7)
    c: Block(g5)
    c: Block(g3)
    c: Block(g1)
    c: Coincident(g24,g0)
    c: Coincident(g24,g12)
    c: Horizontal(g24)
    c: Coincident(g25,g0)
    c: Coincident(g25,g12)
    c: Horizontal(g25)
    c: Coincident(g26,g1)
    c: Coincident(g26,g13)
    c: Horizontal(g26)
    c: Coincident(g27,g1)
    c: Coincident(g27,g13)
    c: Horizontal(g27)
    c: Coincident(g28,g2)
    c: Coincident(g28,g14)
    c: Horizontal(g28)
    c: Coincident(g29,g2)
    c: Coincident(g29,g14)
    c: Horizontal(g29)
    c: Coincident(g30,g3)
    c: Coincident(g30,g15)
    c: Horizontal(g30)
    c: Coincident(g31,g3)
    c: Coincident(g31,g15)
    c: Horizontal(g31)
    c: Coincident(g32,g4)
    c: Coincident(g32,g16)
    c: Horizontal(g32)
    c: Coincident(g33,g4)
    c: Coincident(g33,g16)
    c: Horizontal(g33)
    c: Coincident(g34,g5)
    c: Coincident(g34,g17)
    c: Horizontal(g34)
    c: Coincident(g35,g5)
    c: Coincident(g35,g17)
    c: Horizontal(g35)
    c: Coincident(g36,g6)
    c: Coincident(g36,g19)
    c: Horizontal(g36)
    c: Coincident(g37,g6)
    c: Coincident(g37,g19)
    c: Horizontal(g37)
    c: Coincident(g38,g7)
    c: Coincident(g38,g18)
    c: Horizontal(g38)
    c: Coincident(g39,g7)
    c: Coincident(g39,g18)
    c: Horizontal(g39)
    c: Coincident(g40,g8)
    c: Coincident(g40,g20)
    c: Horizontal(g40)
    c: Coincident(g41,g8)
    c: Coincident(g41,g20)
    c: Horizontal(g41)
    c: Coincident(g42,g9)
    c: Coincident(g42,g23)
    c: Horizontal(g42)
    c: Coincident(g43,g9)
    c: Coincident(g43,g23)
    c: Horizontal(g43)
    c: Coincident(g44,g10)
    c: Coincident(g44,g22)
    c: Horizontal(g44)
    c: Coincident(g45,g10)
    c: Coincident(g45,g22)
    c: Horizontal(g45)
    c: Coincident(g46,g11)
    c: Coincident(g46,g21)
    c: Horizontal(g46)
    c: Coincident(g47,g11)
    c: Coincident(g47,g21)
    c: Horizontal(g47)
FEATURE [Part::Extrusion] Extrude023
  Base = -> Sketch032
  Dir = (1,-2e-16,2e-16)
  DirMode = 2
  FaceMakerClass = Part::FaceMakerBullseye
  LengthFwd = 19
  LengthRev = 0
  Placement = pos=(-19,0,0) rot=(0,0,1;0rad)
  Solid = true
  Symmetric = false
FEATURE [Part::Fillet] Fillet023
  Base = -> Extrude023
  Edges = <same value as first occurrence — deduplicated (x3 in doc)>
  Placement = pos=(0,0.05,0) rot=(0,0,1;0rad)
FEATURE [Part::Cut] Cut014  label="bottom003"
  Base = -> Cut007
  Tool = -> Fusion047
FEATURE [Part::Cut] Cut021  label="bottom004"
  Base = -> Cut014
  Tool = -> Fillet023
FEATURE [Sketcher::SketchObject] Sketch033
  FullyConstrained = true
  Placement = pos=(117,19,0) rot=(0.57735,0.57735,0.57735;2.0944rad)
  sketch-geometry (8):
    g0: LineSegment StartX=-49.19 StartY=69.25 StartZ=0 EndX=-49.19 EndY=66.25 EndZ=0
    g1: LineSegment StartX=-49.19 StartY=5.75 StartZ=0 EndX=-49.19 EndY=2.75 EndZ=0
    g2: ArcOfCircle CenterX=-1.5 CenterY=67.75 CenterZ=0 NormalX=0 NormalY=0 NormalZ=1 AngleXU=0 Radius=1.5 StartAngle=4.71239 EndAngle=7.85398
    g3: ArcOfCircle CenterX=-1.5 CenterY=4.25 CenterZ=0 NormalX=0 NormalY=0 NormalZ=1 AngleXU=0 Radius=1.5 StartAngle=4.71239 EndAngle=7.85398
    g4: LineSegment StartX=-49.19 StartY=69.25 StartZ=0 EndX=-1.5 EndY=69.25 EndZ=0
    g5: LineSegment StartX=-49.19 StartY=66.25 StartZ=0 EndX=-1.5 EndY=66.25 EndZ=0
    g6: LineSegment StartX=-49.19 StartY=5.75 StartZ=0 EndX=-1.5 EndY=5.75 EndZ=0
    g7: LineSegment StartX=-49.19 StartY=2.75 StartZ=0 EndX=-1.5 EndY=2.75 EndZ=0
  constraints (19):
    c: Vertical(g0)
    c: Distance(g0) = 3
    c: Block(g0)
    c: Vertical(g1)
    c: Block(g2)
    c: Block(g3)
    c: Block(g1)
    c: Coincident(g4,g0)
    c: Coincident(g4,g2)
    c: Horizontal(g4)
    c: Coincident(g5,g0)
    c: Coincident(g5,g2)
    c: Horizontal(g5)
    c: Coincident(g6,g1)
    c: Coincident(g6,g3)
    c: Horizontal(g6)
    c: Coincident(g7,g1)
    c: Coincident(g7,g3)
    c: Horizontal(g7)
FEATURE [Sketcher::SketchObject] Sketch034
  FullyConstrained = true
  Placement = pos=(117,19,0) rot=(0.57735,0.57735,0.57735;2.0944rad)
  sketch-geometry (8):
    g0: LineSegment StartX=-49.19 StartY=63.5 StartZ=0 EndX=-49.19 EndY=60.5 EndZ=0
    g1: LineSegment StartX=-49.19 StartY=11.5 StartZ=0 EndX=-49.19 EndY=8.5 EndZ=0
    g2: ArcOfCircle CenterX=-1.5 CenterY=62 CenterZ=0 NormalX=0 NormalY=0 NormalZ=1 AngleXU=0 Radius=1.5 StartAngle=4.71239 EndAngle=7.85398
    g3: ArcOfCircle CenterX=-1.5 CenterY=10 CenterZ=0 NormalX=0 NormalY=0 NormalZ=1 AngleXU=0 Radius=1.5 StartAngle=4.71239 EndAngle=7.85398
    g4: LineSegment StartX=-49.19 StartY=63.5 StartZ=0 EndX=-1.5 EndY=63.5 EndZ=0
    g5: LineSegment StartX=-49.19 StartY=60.5 StartZ=0 EndX=-1.5 EndY=60.5 EndZ=0
    g6: LineSegment StartX=-49.19 StartY=11.5 StartZ=0 EndX=-1.5 EndY=11.5 EndZ=0
    g7: LineSegment StartX=-49.19 StartY=8.5 StartZ=0 EndX=-1.5 EndY=8.5 EndZ=0
  constraints (19):
    c: Vertical(g0)
    c: Distance(g0) = 3
    c: Vertical(g1)
    c: Block(g1)
    c: Block(g2)
    c: Block(g3)
    c: Block(g0)
    c: Coincident(g4,g0)
    c: Coincident(g4,g2)
    c: Horizontal(g4)
    c: Coincident(g5,g0)
    c: Coincident(g5,g2)
    c: Horizontal(g5)
    c: Coincident(g6,g1)
    c: Coincident(g6,g3)
    c: Horizontal(g6)
    c: Coincident(g7,g1)
    c: Coincident(g7,g3)
    c: Horizontal(g7)
FEATURE [Part::Extrusion] Extrude024
  Base = -> Sketch033
  Dir = (1,0,0)
  DirMode = 2
  FaceMakerClass = Part::FaceMakerBullseye
  LengthFwd = 10
  LengthRev = 0
  Solid = true
  Symmetric = false
FEATURE [Part::Extrusion] Extrude025
  Base = -> Sketch034
  Dir = (1,0,0)
  DirMode = 2
  FaceMakerClass = Part::FaceMakerBullseye
  LengthFwd = 10
  LengthRev = 0
  Solid = true
  Symmetric = false
FEATURE [Part::Fillet] Fillet024  label="removeFromtMoreFrontCaseScrewRetainers"
  Base = -> Extrude024
  Edges = 4 edges r=1.49: [Edge6,Edge11,Edge18,Edge23]
  Placement = pos=(-11,0,0) rot=(0,0,1;0rad)
FEATURE [Part::Fillet] Fillet025  label="removeFromtMoreFrontCaseScrewRetainers001"
  Base = -> Extrude025
  Edges = 4 edges r=1.49: [Edge6,Edge11,Edge18,Edge23]
  Placement = pos=(-19,0,0) rot=(0,0,1;0rad)
FEATURE [Part::Cut] Cut022
  Base = -> Cut015
  Tool = -> Fillet025
FEATURE [Part::Cut] Cut023  label="screwRetainers"
  Base = -> Cut022
  Tool = -> Fillet024
FEATURE [Part::MultiFuse] Fusion056  label="bottom005"
  Shapes = -> [Fusion044,Cut021]
FEATURE [Part::MultiFuse] Fusion057  label="casePillars001"
  Shapes = -> [Cut016,Fusion052]
FEATURE [Part::MultiFuse] Fusion058  label="bottom006"
  Shapes = -> [Fusion056,Cut023]
FEATURE [Part::MultiFuse] Fusion059  label="bottom007"
  Shapes = -> [Fusion058,Fillet005]
FEATURE [Part::MultiFuse] Fusion060  label="bottom008"
  Shapes = -> [Fusion059,Fusion]
FEATURE [Part::MultiFuse] Fusion061  label="top011"
  Shapes = -> [Cut006,Cut020]
FEATURE [Part::MultiFuse] Fusion062  label="top012"
  Shapes = -> [Fusion057,Fusion061]
FEATURE [Sketcher::SketchObject] Sketch035  label="topSketch007"
  FullyConstrained = true
  sketch-geometry (6):
    g0: LineSegment StartX=19 StartY=38 StartZ=0 EndX=117 EndY=38 EndZ=0
    g1: ArcOfCircle CenterX=19 CenterY=19 CenterZ=0 NormalX=0 NormalY=0 NormalZ=1 AngleXU=0 Radius=19 StartAngle=1.5708 EndAngle=3.14159
    g2: LineSegment StartX=117 StartY=38 StartZ=0 EndX=117 EndY=19 EndZ=0
    g3: LineSegment StartX=98 StartY=1.0161e-12 StartZ=0 EndX=5.22862e-06 EndY=1.0161e-12 EndZ=0
    g4: LineSegment StartX=5.22862e-06 StartY=19 StartZ=0 EndX=5.22862e-06 EndY=1.0161e-12 EndZ=0
    g5: ArcOfCircle CenterX=98 CenterY=19 CenterZ=0 NormalX=0 NormalY=0 NormalZ=1 AngleXU=0 Radius=19 StartAngle=4.71239 EndAngle=6.28319
  constraints (16):
    c: Horizontal(g0)
    c: Distance(g0) = 98
    c: Coincident(g1,g0)
    c: Block(g1)
    c: Coincident(g2,g0)
    c: Vertical(g2)
    c: Distance(g2) = 19
    c: Horizontal(g3)
    c: Coincident(g4,g1)
    c: Vertical(g4)
    c: Coincident(g3,g4)
    c: Block(g3)
    c: Coincident(g5,g2)
    c: Coincident(g5,g3)
    c: Block(g0)
    c: Block(g5)
FEATURE [Part::Extrusion] Extrude026  label="sideA001"
  Base = -> Sketch035
  Dir = (0,0,1)
  DirMode = 2
  FaceMakerClass = Part::FaceMakerBullseye
  LengthFwd = 3
  LengthRev = 0
  Placement = pos=(0,0,-2.7) rot=(0,0,1;0rad)
  Solid = true
  Symmetric = false
FEATURE [Sketcher::SketchObject] Sketch036  label="topSketch008"
  FullyConstrained = true
  sketch-geometry (6):
    g0: LineSegment StartX=19 StartY=38 StartZ=0 EndX=117 EndY=38 EndZ=0
    g1: ArcOfCircle CenterX=19 CenterY=19 CenterZ=0 NormalX=0 NormalY=0 NormalZ=1 AngleXU=0 Radius=19 StartAngle=1.5708 EndAngle=3.14159
    g2: LineSegment StartX=117 StartY=38 StartZ=0 EndX=117 EndY=19 EndZ=0
    g3: LineSegment StartX=98 StartY=1.0161e-12 StartZ=0 EndX=5.22862e-06 EndY=1.0161e-12 EndZ=0
    g4: LineSegment StartX=5.22862e-06 StartY=19 StartZ=0 EndX=5.22862e-06 EndY=1.0161e-12 EndZ=0
    g5: ArcOfCircle CenterX=98 CenterY=19 CenterZ=0 NormalX=0 NormalY=0 NormalZ=1 AngleXU=0 Radius=19 StartAngle=4.71239 EndAngle=6.28319
  constraints (16):
    c: Horizontal(g0)
    c: Distance(g0) = 98
    c: Coincident(g1,g0)
    c: Block(g1)
    c: Coincident(g2,g0)
    c: Vertical(g2)
    c: Distance(g2) = 19
    c: Horizontal(g3)
    c: Coincident(g4,g1)
    c: Vertical(g4)
    c: Coincident(g3,g4)
    c: Block(g3)
    c: Coincident(g5,g2)
    c: Coincident(g5,g3)
    c: Block(g0)
    c: Block(g5)
FEATURE [Part::Extrusion] Extrude027  label="sideB001"
  Base = -> Sketch036
  Dir = (0,0,1)
  DirMode = 2
  FaceMakerClass = Part::FaceMakerBullseye
  LengthFwd = 3
  LengthRev = 0
  Placement = pos=(0,0,71.7) rot=(0,0,1;0rad)
  Solid = true
  Symmetric = false
FEATURE [Part::MultiFuse] Fusion064  label="removeFromBottom"
  Shapes = -> [Extrude026,Extrude027]
FEATURE [Part::Cut] Cut024  label="bottom009"
  Base = -> Fusion060
  Tool = -> Fusion064
FEATURE [Sketcher::SketchObject] Sketch037  label="topSketch009"
  FullyConstrained = true
  sketch-geometry (6):
    g0: ArcOfCircle CenterX=19 CenterY=19 CenterZ=0 NormalX=0 NormalY=0 NormalZ=1 AngleXU=0 Radius=19 StartAngle=1.5708 EndAngle=3.14159
    g1: LineSegment StartX=5.22862e-06 StartY=19 StartZ=0 EndX=5.22862e-06 EndY=1.19904e-11 EndZ=0
    g2: LineSegment StartX=19 StartY=38 StartZ=0 EndX=124 EndY=38 EndZ=0
    g3: LineSegment StartX=5.22862e-06 StartY=1.19904e-11 StartZ=0 EndX=105 EndY=1.19904e-11 EndZ=0
    g4: ArcOfCircle CenterX=105 CenterY=19 CenterZ=0 NormalX=0 NormalY=0 NormalZ=1 AngleXU=0 Radius=19 StartAngle=4.71239 EndAngle=6.28319
    g5: LineSegment StartX=124 StartY=38 StartZ=0 EndX=124 EndY=19 EndZ=0
  constraints (16):
    c: Block(g0)
    c: Coincident(g1,g0)
    c: Vertical(g1)
    c: Horizontal(g2)
    c: Distance(g2) = 105
    c: Coincident(g2,g0)
    c: Distance(g1) = 19
    c: Coincident(g3,g1)
    c: Horizontal(g3)
    c: Distance(g3) = 105
    c: Block(g4)
    c: Coincident(g4,g3)
    c: Coincident(g5,g2)
    c: Coincident(g5,g4)
    c: Vertical(g5)
    c: Distance(g5) = 19
FEATURE [Part::Extrusion] Extrude028  label="sideB"
  Base = -> Sketch037
  Dir = (0,0,1)
  DirMode = 2
  FaceMakerClass = Part::FaceMakerBullseye
  LengthFwd = 3
  LengthRev = 0
  Placement = pos=(0,0,72) rot=(0,0,1;0rad)
  Solid = true
  Symmetric = false
FEATURE [Sketcher::SketchObject] Sketch038  label="topSketch010"
  FullyConstrained = true
  sketch-geometry (22):
    g0: LineSegment StartX=5.21097e-06 StartY=3 StartZ=0 EndX=5.21097e-06 EndY=19 EndZ=0
    g1: ArcOfCircle CenterX=19 CenterY=19 CenterZ=0 NormalX=0 NormalY=0 NormalZ=1 AngleXU=0 Radius=19 StartAngle=1.5708 EndAngle=3.14159
    g2: ArcOfCircle CenterX=19 CenterY=19 CenterZ=0 NormalX=0 NormalY=0 NormalZ=1 AngleXU=0 Radius=16 StartAngle=1.5708 EndAngle=3.14159
    g3: LineSegment StartX=114 StartY=35 StartZ=0 EndX=19 EndY=35 EndZ=0
    g4: LineSegment StartX=5.21097e-06 StartY=3 StartZ=0 EndX=5.21097e-06 EndY=0 EndZ=0
    g5: LineSegment StartX=3 StartY=0 StartZ=0 EndX=5.21097e-06 EndY=0 EndZ=0
    g6: LineSegment StartX=3 StartY=19 StartZ=0 EndX=3 EndY=0 EndZ=0
    g7: LineSegment StartX=19 StartY=38 StartZ=0 EndX=124 EndY=38 EndZ=0
    g8: Circle CenterX=119 CenterY=35 CenterZ=0 NormalX=0 NormalY=0 NormalZ=1 AngleXU=0 Radius=1
    g9: Circle CenterX=121 CenterY=35 CenterZ=0 NormalX=0 NormalY=0 NormalZ=1 AngleXU=0 Radius=1
    g10: Circle CenterX=121 CenterY=33 CenterZ=0 NormalX=0 NormalY=0 NormalZ=1 AngleXU=0 Radius=1
    g11: BSplineCurve PolesCount=3 KnotsCount=2 Degree=2 IsPeriodic=0
    g12: GeomPoint X=119 Y=35 Z=0
    g13: GeomPoint X=121 Y=33 Z=0
    g14: LineSegment StartX=119 StartY=35 StartZ=0 EndX=114 EndY=35 EndZ=0
    g15: ArcOfCircle CenterX=105 CenterY=19 CenterZ=0 NormalX=0 NormalY=0 NormalZ=1 AngleXU=0 Radius=16 StartAngle=5.60905 EndAngle=6.28319
    g16: LineSegment StartX=121 StartY=33 StartZ=0 EndX=121 EndY=19 EndZ=0
    g17: LineSegment StartX=117.5 StartY=9.01251 StartZ=0 EndX=121.163 EndY=9.0125 EndZ=0
    g18: ArcOfCircle CenterX=105 CenterY=19 CenterZ=0 NormalX=0 NormalY=0 NormalZ=1 AngleXU=0 Radius=20.6155 StartAngle=5.7297 EndAngle=6.28319
    g19: LineSegment StartX=121.163 StartY=9.0125 StartZ=0 EndX=122.538 EndY=8.16329 EndZ=0
    g20: LineSegment StartX=124 StartY=38 StartZ=0 EndX=125.616 EndY=38 EndZ=0
    g21: LineSegment StartX=125.616 StartY=19 StartZ=0 EndX=125.616 EndY=38 EndZ=0
  constraints (49):
    c: Vertical(g0)
    c: Block(g0)
    c: Coincident(g1,g0)
    c: Block(g1)
    c: Coincident(g2,g1)
    c: Block(g2)
    c: Coincident(g3,g2)
    c: Horizontal(g3)
    c: Tangent(g3,g2)
    c: Coincident(g4,g0)
    c: Distance(g4) = 3
    c: Vertical(g4)
    c: Coincident(g5,g4)
    c: Horizontal(g5)
    c: Coincident(g6,g2)
    c: Coincident(g6,g5)
    c: Vertical(g6)
    c: Horizontal(g7)
    c: Distance(g7) = 105
    c: Coincident(g7,g1)
    c: Block(g3)
    c: Weight(g8) = 1
    c: Equal(g8,g9)
    c: Equal(g8,g10)
    c: InternalAlignment(g8,g11)
    c: InternalAlignment(g9,g11)
    c: InternalAlignment(g10,g11)
    c: InternalAlignment(g12,g11)
    c: InternalAlignment(g13,g11)
    c: Block(g11)
    c: Coincident(g14,g11)
    c: Coincident(g14,g3)
    c: Horizontal(g14)
    c: Block(g15)
    c: Coincident(g16,g11)
    c: Coincident(g16,g15)
    c: Vertical(g16)
    c: Distance(g16) = 14
    c: Coincident(g17,g15)
    c: Block(g18)
    c: Coincident(g19,g18)
    c: Coincident(g20,g7)
    c: Horizontal(g20)
    c: Vertical(g21)
    c: Coincident(g20,g21)
    c: Block(g20)
    c: Block(g21)
    c: Block(g19)
    c: Block(g17)
FEATURE [Part::Extrusion] Extrude029
  Base = -> Sketch038
  Dir = (0,0,1)
  DirMode = 2
  FaceMakerClass = Part::FaceMakerBullseye
  LengthFwd = 72
  LengthRev = 0
  Solid = true
  Symmetric = false
FEATURE [Part::Feature] Face085
  shape: bbox 4.8 x 25.5 x 2e-07 mm, 1 faces, 0 solids (baked)
FEATURE [Part::Revolution] Revolve089  label="moreFrontCaseScrewPost003"
  Angle = 360
  Axis = (0,1,0)
  Base = (0,0,0)
  FaceMakerClass = Part::FaceMakerBullseye
  Placement = pos=(109.5,4.5,3.5) rot=(0,0,1;0rad)
  Solid = false
  Source = -> Face085
  Symmetric = false
FEATURE [Part::Feature] Face086
  shape: bbox 4.8 x 25.5 x 2e-07 mm, 1 faces, 0 solids (baked)
FEATURE [Part::Revolution] Revolve090  label="moreFrontCaseScrewPost004"
  Angle = 360
  Axis = (0,1,0)
  Base = (0,0,0)
  FaceMakerClass = Part::FaceMakerBullseye
  Placement = pos=(109.5,4.5,68.5) rot=(0,0,1;0rad)
  Solid = false
  Source = -> Face086
  Symmetric = false
FEATURE [Part::Fillet] Fillet026  label="top013"
  Base = -> Extrude029
  Edges = 1 edges r=2: [Edge35]
FEATURE [Sketcher::SketchObject] Sketch039
  FullyConstrained = true
  sketch-geometry (7):
    g0: LineSegment StartX=0 StartY=0 StartZ=0 EndX=0 EndY=6 EndZ=0
    g1: Circle CenterX=0 CenterY=0 CenterZ=0 NormalX=0 NormalY=0 NormalZ=1 AngleXU=0 Radius=1
    g2: Circle CenterX=8 CenterY=6 CenterZ=0 NormalX=0 NormalY=0 NormalZ=1 AngleXU=0 Radius=1
    g3: BSplineCurve PolesCount=3 KnotsCount=2 Degree=2 IsPeriodic=0
    g4: GeomPoint X=0 Y=0 Z=0
    g5: GeomPoint X=8 Y=6 Z=0
    g6: LineSegment StartX=0 StartY=6 StartZ=0 EndX=8 EndY=6 EndZ=0
  constraints (14):
    c: Coincident(g0,g-1)
    c: Distance(g0) = 6
    c: Vertical(g0)
    c: Coincident(g3,g0)
    c: Weight(g1) = 1
    c: Equal(g1,g2)
    c: InternalAlignment(g1,g3)
    c: InternalAlignment(g2,g3)
    c: InternalAlignment(g4,g3)
    c: InternalAlignment(g5,g3)
    c: Block(g3)
    c: Coincident(g6,g0)
    c: Coincident(g6,g3)
    c: Horizontal(g6)
FEATURE [Sketcher::SketchObject] Sketch040
  FullyConstrained = true
  sketch-geometry (7):
    g0: LineSegment StartX=0 StartY=0 StartZ=0 EndX=0 EndY=6 EndZ=0
    g1: Circle CenterX=0 CenterY=0 CenterZ=0 NormalX=0 NormalY=0 NormalZ=1 AngleXU=0 Radius=1
    g2: Circle CenterX=8 CenterY=6 CenterZ=0 NormalX=0 NormalY=0 NormalZ=1 AngleXU=0 Radius=1
    g3: BSplineCurve PolesCount=3 KnotsCount=2 Degree=2 IsPeriodic=0
    g4: GeomPoint X=0 Y=0 Z=0
    g5: GeomPoint X=8 Y=6 Z=0
    g6: LineSegment StartX=0 StartY=6 StartZ=0 EndX=8 EndY=6 EndZ=0
  constraints (14):
    c: Coincident(g0,g-1)
    c: Distance(g0) = 6
    c: Vertical(g0)
    c: Coincident(g3,g0)
    c: Weight(g1) = 1
    c: Equal(g1,g2)
    c: InternalAlignment(g1,g3)
    c: InternalAlignment(g2,g3)
    c: InternalAlignment(g4,g3)
    c: InternalAlignment(g5,g3)
    c: Block(g3)
    c: Coincident(g6,g0)
    c: Coincident(g6,g3)
    c: Horizontal(g6)
FEATURE [Sketcher::SketchObject] Sketch041
  FullyConstrained = true
  sketch-geometry (7):
    g0: LineSegment StartX=0 StartY=0 StartZ=0 EndX=0 EndY=6 EndZ=0
    g1: Circle CenterX=0 CenterY=0 CenterZ=0 NormalX=0 NormalY=0 NormalZ=1 AngleXU=0 Radius=1
    g2: Circle CenterX=8 CenterY=6 CenterZ=0 NormalX=0 NormalY=0 NormalZ=1 AngleXU=0 Radius=1
    g3: BSplineCurve PolesCount=3 KnotsCount=2 Degree=2 IsPeriodic=0
    g4: GeomPoint X=0 Y=0 Z=0
    g5: GeomPoint X=8 Y=6 Z=0
    g6: LineSegment StartX=0 StartY=6 StartZ=0 EndX=8 EndY=6 EndZ=0
  constraints (14):
    c: Coincident(g0,g-1)
    c: Distance(g0) = 6
    c: Vertical(g0)
    c: Coincident(g3,g0)
    c: Weight(g1) = 1
    c: Equal(g1,g2)
    c: InternalAlignment(g1,g3)
    c: InternalAlignment(g2,g3)
    c: InternalAlignment(g4,g3)
    c: InternalAlignment(g5,g3)
    c: Block(g3)
    c: Coincident(g6,g0)
    c: Coincident(g6,g3)
    c: Horizontal(g6)
FEATURE [Sketcher::SketchObject] Sketch042
  FullyConstrained = true
  sketch-geometry (7):
    g0: LineSegment StartX=0 StartY=0 StartZ=0 EndX=0 EndY=6 EndZ=0
    g1: Circle CenterX=0 CenterY=0 CenterZ=0 NormalX=0 NormalY=0 NormalZ=1 AngleXU=0 Radius=1
    g2: Circle CenterX=8 CenterY=6 CenterZ=0 NormalX=0 NormalY=0 NormalZ=1 AngleXU=0 Radius=1
    g3: BSplineCurve PolesCount=3 KnotsCount=2 Degree=2 IsPeriodic=0
    g4: GeomPoint X=0 Y=0 Z=0
    g5: GeomPoint X=8 Y=6 Z=0
    g6: LineSegment StartX=0 StartY=6 StartZ=0 EndX=8 EndY=6 EndZ=0
  constraints (14):
    c: Coincident(g0,g-1)
    c: Distance(g0) = 6
    c: Vertical(g0)
    c: Coincident(g3,g0)
    c: Weight(g1) = 1
    c: Equal(g1,g2)
    c: InternalAlignment(g1,g3)
    c: InternalAlignment(g2,g3)
    c: InternalAlignment(g4,g3)
    c: InternalAlignment(g5,g3)
    c: Block(g3)
    c: Coincident(g6,g0)
    c: Coincident(g6,g3)
    c: Horizontal(g6)
FEATURE [Part::Extrusion] Extrude030  label="caseScrewPillarBracket008"
  Base = -> Sketch039
  Dir = (0,0,1)
  DirMode = 2
  FaceMakerClass = Part::FaceMakerBullseye
  LengthFwd = 2.4
  LengthRev = 0
  Placement = pos=(15.76,29,8.8) rot=(0,1,0;0rad)
  Solid = true
  Symmetric = false
FEATURE [Part::Extrusion] Extrude031  label="caseScrewPillarBracket009"
  Base = -> Sketch040
  Dir = (0,0,1)
  DirMode = 2
  FaceMakerClass = Part::FaceMakerBullseye
  LengthFwd = 2.4
  LengthRev = 0
  Placement = pos=(15.76,29,60.8) rot=(0,0,1;0rad)
  Solid = true
  Symmetric = false
FEATURE [Part::Extrusion] Extrude032  label="caseScrewPillarBracket010"
  Base = -> Sketch041
  Dir = (0,0,1)
  DirMode = 2
  FaceMakerClass = Part::FaceMakerBullseye
  LengthFwd = 2.4
  LengthRev = 0
  Placement = pos=(13.7,29,13.26) rot=(0,-1,0;1.5708rad)
  Solid = true
  Symmetric = false
FEATURE [Part::Extrusion] Extrude033  label="caseScrewPillarBracket011"
  Base = -> Sketch042
  Dir = (0,0,1)
  DirMode = 2
  FaceMakerClass = Part::FaceMakerBullseye
  LengthFwd = 2.4
  LengthRev = 0
  Placement = pos=(11.3,29,58.74) rot=(0,1,0;1.5708rad)
  Solid = true
  Symmetric = false
FEATURE [Sketcher::SketchObject] Sketch043
  FullyConstrained = true
  sketch-geometry (7):
    g0: LineSegment StartX=0 StartY=0 StartZ=0 EndX=0 EndY=6 EndZ=0
    g1: Circle CenterX=0 CenterY=0 CenterZ=0 NormalX=0 NormalY=0 NormalZ=1 AngleXU=0 Radius=1
    g2: Circle CenterX=8 CenterY=6 CenterZ=0 NormalX=0 NormalY=0 NormalZ=1 AngleXU=0 Radius=1
    g3: BSplineCurve PolesCount=3 KnotsCount=2 Degree=2 IsPeriodic=0
    g4: GeomPoint X=0 Y=0 Z=0
    g5: GeomPoint X=8 Y=6 Z=0
    g6: LineSegment StartX=0 StartY=6 StartZ=0 EndX=8 EndY=6 EndZ=0
  constraints (14):
    c: Coincident(g0,g-1)
    c: Distance(g0) = 6
    c: Vertical(g0)
    c: Coincident(g3,g0)
    c: Weight(g1) = 1
    c: Equal(g1,g2)
    c: InternalAlignment(g1,g3)
    c: InternalAlignment(g2,g3)
    c: InternalAlignment(g4,g3)
    c: InternalAlignment(g5,g3)
    c: Block(g3)
    c: Coincident(g6,g0)
    c: Coincident(g6,g3)
    c: Horizontal(g6)
FEATURE [Part::Extrusion] Extrude034  label="caseScrewPillarBracket012"
  Base = -> Sketch043
  Dir = (0,0,1)
  DirMode = 2
  FaceMakerClass = Part::FaceMakerBullseye
  LengthFwd = 2.4
  LengthRev = 0
  Placement = pos=(88.3,29,65.23) rot=(0,1,0;1.5708rad)
  Solid = true
  Symmetric = false
FEATURE [Sketcher::SketchObject] Sketch044
  FullyConstrained = true
  sketch-geometry (7):
    g0: LineSegment StartX=0 StartY=0 StartZ=0 EndX=0 EndY=6 EndZ=0
    g1: Circle CenterX=0 CenterY=0 CenterZ=0 NormalX=0 NormalY=0 NormalZ=1 AngleXU=0 Radius=1
    g2: Circle CenterX=8 CenterY=6 CenterZ=0 NormalX=0 NormalY=0 NormalZ=1 AngleXU=0 Radius=1
    g3: BSplineCurve PolesCount=3 KnotsCount=2 Degree=2 IsPeriodic=0
    g4: GeomPoint X=0 Y=0 Z=0
    g5: GeomPoint X=8 Y=6 Z=0
    g6: LineSegment StartX=0 StartY=6 StartZ=0 EndX=8 EndY=6 EndZ=0
  constraints (14):
    c: Coincident(g0,g-1)
    c: Distance(g0) = 6
    c: Vertical(g0)
    c: Coincident(g3,g0)
    c: Weight(g1) = 1
    c: Equal(g1,g2)
    c: InternalAlignment(g1,g3)
    c: InternalAlignment(g2,g3)
    c: InternalAlignment(g4,g3)
    c: InternalAlignment(g5,g3)
    c: Block(g3)
    c: Coincident(g6,g0)
    c: Coincident(g6,g3)
    c: Horizontal(g6)
FEATURE [Part::Extrusion] Extrude035  label="caseScrewPillarBracket013"
  Base = -> Sketch044
  Dir = (0,0,1)
  DirMode = 2
  FaceMakerClass = Part::FaceMakerBullseye
  LengthFwd = 2.4
  LengthRev = 0
  Placement = pos=(90.7,29,6.77) rot=(0,-1,0;1.5708rad)
  Solid = true
  Symmetric = false
FEATURE [Sketcher::SketchObject] Sketch045
  FullyConstrained = true
  sketch-geometry (7):
    g0: LineSegment StartX=0 StartY=0 StartZ=0 EndX=0 EndY=6 EndZ=0
    g1: Circle CenterX=0 CenterY=0 CenterZ=0 NormalX=0 NormalY=0 NormalZ=1 AngleXU=0 Radius=1
    g2: Circle CenterX=8 CenterY=6 CenterZ=0 NormalX=0 NormalY=0 NormalZ=1 AngleXU=0 Radius=1
    g3: BSplineCurve PolesCount=3 KnotsCount=2 Degree=2 IsPeriodic=0
    g4: GeomPoint X=0 Y=0 Z=0
    g5: GeomPoint X=8 Y=6 Z=0
    g6: LineSegment StartX=0 StartY=6 StartZ=0 EndX=8 EndY=6 EndZ=0
  constraints (14):
    c: Coincident(g0,g-1)
    c: Distance(g0) = 6
    c: Vertical(g0)
    c: Coincident(g3,g0)
    c: Weight(g1) = 1
    c: Equal(g1,g2)
    c: InternalAlignment(g1,g3)
    c: InternalAlignment(g2,g3)
    c: InternalAlignment(g4,g3)
    c: InternalAlignment(g5,g3)
    c: Block(g3)
    c: Coincident(g6,g0)
    c: Coincident(g6,g3)
    c: Horizontal(g6)
FEATURE [Sketcher::SketchObject] Sketch046
  FullyConstrained = true
  sketch-geometry (7):
    g0: LineSegment StartX=0 StartY=0 StartZ=0 EndX=0 EndY=6 EndZ=0
    g1: Circle CenterX=0 CenterY=0 CenterZ=0 NormalX=0 NormalY=0 NormalZ=1 AngleXU=0 Radius=1
    g2: Circle CenterX=8 CenterY=6 CenterZ=0 NormalX=0 NormalY=0 NormalZ=1 AngleXU=0 Radius=1
    g3: BSplineCurve PolesCount=3 KnotsCount=2 Degree=2 IsPeriodic=0
    g4: GeomPoint X=0 Y=0 Z=0
    g5: GeomPoint X=8 Y=6 Z=0
    g6: LineSegment StartX=0 StartY=6 StartZ=0 EndX=8 EndY=6 EndZ=0
  constraints (14):
    c: Coincident(g0,g-1)
    c: Distance(g0) = 6
    c: Vertical(g0)
    c: Coincident(g3,g0)
    c: Weight(g1) = 1
    c: Equal(g1,g2)
    c: InternalAlignment(g1,g3)
    c: InternalAlignment(g2,g3)
    c: InternalAlignment(g4,g3)
    c: InternalAlignment(g5,g3)
    c: Block(g3)
    c: Coincident(g6,g0)
    c: Coincident(g6,g3)
    c: Horizontal(g6)
FEATURE [Part::Extrusion] Extrude036  label="caseScrewPillarBracket014"
  Base = -> Sketch045
  Dir = (0,0,1)
  DirMode = 2
  FaceMakerClass = Part::FaceMakerBullseye
  LengthFwd = 2.4
  LengthRev = 0
  Placement = pos=(110.7,29,6.77) rot=(0,-1,0;1.5708rad)
  Solid = true
  Symmetric = false
FEATURE [Part::Extrusion] Extrude037  label="caseScrewPillarBracket015"
  Base = -> Sketch046
  Dir = (0,0,1)
  DirMode = 2
  FaceMakerClass = Part::FaceMakerBullseye
  LengthFwd = 2.4
  LengthRev = 0
  Placement = pos=(108.3,29,65.23) rot=(0,1,0;1.5708rad)
  Solid = true
  Symmetric = false
FEATURE [Part::Box] Box013  label="frontCaseScrewPillarBracket002"
  AttacherType = Attacher::AttachEngine3D
  Height = 2.4
  Length = 22
  Placement = pos=(87,28,2.3) rot=(0,0,1;0rad)
  Width = 7
FEATURE [Part::Box] Box014  label="frontCaseScrewPillarBracket003"
  AttacherType = Attacher::AttachEngine3D
  Height = 2.4
  Length = 22
  Placement = pos=(87,28,67.3) rot=(0,0,1;0rad)
  Width = 7
FEATURE [Part::Feature] Face087
  shape: bbox 4.8 x 30.2 x 2e-07 mm, 1 faces, 0 solids (baked)
FEATURE [Part::Revolution] Revolve091  label="frontCaseScrewPost004"
  Angle = 360
  Axis = (0,1,0)
  Base = (0,0,0)
  FaceMakerClass = Part::FaceMakerBullseye
  Placement = pos=(89.5,4.5,3.5) rot=(0,0,1;0rad)
  Solid = false
  Source = -> Face087
  Symmetric = false
FEATURE [Part::Feature] Face088
  shape: bbox 4.8 x 30.2 x 2e-07 mm, 1 faces, 0 solids (baked)
FEATURE [Part::Revolution] Revolve092  label="frontCaseScrewPost005"
  Angle = 360
  Axis = (0,1,0)
  Base = (0,0,0)
  FaceMakerClass = Part::FaceMakerBullseye
  Placement = pos=(89.5,4.5,68.5) rot=(0,0,1;0rad)
  Solid = false
  Source = -> Face088
  Symmetric = false
FEATURE [Part::Feature] Face089
  shape: bbox 3.5 x 30.2 x 2e-07 mm, 1 faces, 0 solids (baked)
FEATURE [Part::Revolution] Revolve093  label="backCaseScrewPost002"
  Angle = 360
  Axis = (0,1,0)
  Base = (0,0,0)
  FaceMakerClass = Part::FaceMakerBullseye
  Placement = pos=(12.5,4.5,10) rot=(0,0,1;0rad)
  Solid = false
  Source = -> Face089
  Symmetric = false
FEATURE [Part::Feature] Face090
  shape: bbox 3.5 x 30.2 x 2e-07 mm, 1 faces, 0 solids (baked)
FEATURE [Part::Revolution] Revolve094  label="backCaseScrewPost003"
  Angle = 360
  Axis = (0,1,0)
  Base = (0,0,0)
  FaceMakerClass = Part::FaceMakerBullseye
  Placement = pos=(12.5,4.5,62) rot=(0,0,1;0rad)
  Solid = false
  Source = -> Face090
  Symmetric = false
FEATURE [Part::Box] Box015  label="Cube011"
  AttacherType = Attacher::AttachEngine3D
  Height = 28.8
  Length = 3
  Placement = pos=(107.3,28,21.6) rot=(0,0,1;0rad)
  Width = 7
FEATURE [Part::Box] Box016  label="Cube012"
  AttacherType = Attacher::AttachEngine3D
  Height = 3
  Length = 7.4
  Placement = pos=(107.3,28,18.6) rot=(0,0,1;0rad)
  Width = 7
FEATURE [Part::Box] Box017  label="Cube013"
  AttacherType = Attacher::AttachEngine3D
  Height = 3
  Length = 7.4
  Placement = pos=(107.3,28,50.4) rot=(0,0,1;0rad)
  Width = 7
FEATURE [Part::Cylinder] Cylinder024
  Angle = 360
  AttacherType = Attacher::AttachEngine3D
  Height = 20
  Placement = pos=(0,0,36.15) rot=(0,0,1;0rad)
  Radius = 14.3
FEATURE [Part::Cylinder] Cylinder025
  Angle = 360
  AttacherType = Attacher::AttachEngine3D
  Height = 10
  Placement = pos=(0,0,36.15) rot=(0,0,1;0rad)
  Radius = 4
FEATURE [Part::MultiFuse] Fusion066  label="removeToCreteHoleForPlugHousing009"
  Placement = pos=(70,19,36) rot=(0,1,0;1.5708rad)
  Shapes = -> [Cylinder024,Cylinder025]
FEATURE [Part::MultiFuse] Fusion065  label="plugHousingBracketHolder002"
  Shapes = -> [Box017,Box015,Box016]
FEATURE [Part::Cut] Cut025  label="plugHousingBracketHolder003"
  Base = -> Fusion065
  Placement = pos=(7,0,0) rot=(0,0,1;0rad)
  Tool = -> Fusion066
FEATURE [Sketcher::SketchObject] Sketch047
  FullyConstrained = false
  Placement = pos=(0,0,0) rot=(1,0,0;1.5708rad)
  sketch-geometry (24):
    g0: ArcOfCircle CenterX=-4 CenterY=-10.5 CenterZ=0 NormalX=0 NormalY=0 NormalZ=1 AngleXU=0 Radius=1.5 StartAngle=6e-16 EndAngle=3.14159
    g1: ArcOfCircle CenterX=-34.2 CenterY=-10.5 CenterZ=0 NormalX=0 NormalY=0 NormalZ=1 AngleXU=0 Radius=1.5 StartAngle=0 EndAngle=3.14159
    g2: ArcOfCircle CenterX=-34.2 CenterY=-27.7 CenterZ=0 NormalX=0 NormalY=0 NormalZ=1 AngleXU=0 Radius=1.5 StartAngle=3.14159 EndAngle=6.28319
    g3: ArcOfCircle CenterX=-4 CenterY=-27.7 CenterZ=0 NormalX=0 NormalY=0 NormalZ=1 AngleXU=0 Radius=1.5 StartAngle=3.1416 EndAngle=6.28319
    g4: ArcOfCircle CenterX=-10 CenterY=-4.3 CenterZ=0 NormalX=0 NormalY=0 NormalZ=1 AngleXU=0 Radius=1.5 StartAngle=2e-16 EndAngle=3.14159
    g5: ArcOfCircle CenterX=-16.1 CenterY=-1.8 CenterZ=0 NormalX=0 NormalY=0 NormalZ=1 AngleXU=0 Radius=1.5 StartAngle=5e-16 EndAngle=3.14159
    g6: ArcOfCircle CenterX=-22.1 CenterY=-1.8 CenterZ=0 NormalX=0 NormalY=0 NormalZ=1 AngleXU=0 Radius=1.5 StartAngle=5e-16 EndAngle=3.14159
    g7: ArcOfCircle CenterX=-28.2 CenterY=-4.3 CenterZ=0 NormalX=0 NormalY=0 NormalZ=1 AngleXU=0 Radius=1.5 StartAngle=2e-16 EndAngle=3.14159
    g8: ArcOfCircle CenterX=-10 CenterY=-33.9 CenterZ=0 NormalX=0 NormalY=0 NormalZ=1 AngleXU=0 Radius=1.5 StartAngle=3.14159 EndAngle=6.28319
    g9: ArcOfCircle CenterX=-16.1 CenterY=-36.4 CenterZ=0 NormalX=0 NormalY=0 NormalZ=1 AngleXU=0 Radius=1.5 StartAngle=3.14159 EndAngle=6.28319
    g10: ArcOfCircle CenterX=-22.1 CenterY=-36.4 CenterZ=0 NormalX=0 NormalY=0 NormalZ=1 AngleXU=0 Radius=1.5 StartAngle=3.14159 EndAngle=6.28319
    g11: ArcOfCircle CenterX=-28.2 CenterY=-33.9 CenterZ=0 NormalX=0 NormalY=0 NormalZ=1 AngleXU=0 Radius=1.5 StartAngle=3.14159 EndAngle=6.28319
    g12: LineSegment StartX=-35.7 StartY=-10.5 StartZ=0 EndX=-35.7 EndY=-27.7 EndZ=0
    g13: LineSegment StartX=-32.7 StartY=-10.5 StartZ=0 EndX=-32.7 EndY=-27.7 EndZ=0
    g14: LineSegment StartX=-29.7 StartY=-33.9 StartZ=0 EndX=-29.7 EndY=-4.3 EndZ=0
    g15: LineSegment StartX=-26.7 StartY=-33.9 StartZ=0 EndX=-26.7 EndY=-4.3 EndZ=0
    g16: LineSegment StartX=-2.5 StartY=-10.5 StartZ=0 EndX=-2.5 EndY=-27.7 EndZ=0
    g17: LineSegment StartX=-8.5 StartY=-4.3 StartZ=0 EndX=-8.5 EndY=-33.9 EndZ=0
    g18: LineSegment StartX=-5.5 StartY=-10.5 StartZ=0 EndX=-5.5 EndY=-27.7 EndZ=0
    g19: LineSegment StartX=-11.5 StartY=-4.3 StartZ=0 EndX=-11.5 EndY=-33.9 EndZ=0
    g20: LineSegment StartX=-14.6 StartY=-1.8 StartZ=0 EndX=-14.6 EndY=-36.4 EndZ=0
    g21: LineSegment StartX=-17.6 StartY=-1.8 StartZ=0 EndX=-17.6 EndY=-36.4 EndZ=0
    g22: LineSegment StartX=-20.6 StartY=-36.4 StartZ=0 EndX=-20.6 EndY=-1.8 EndZ=0
    g23: LineSegment StartX=-23.6 StartY=-1.8 StartZ=0 EndX=-23.6 EndY=-36.4 EndZ=0
  constraints (48):
    c: Block(g0)
    c: Block(g1)
    c: Block(g2)
    c: Block(g3)
    c: Block(g4)
    c: Block(g5)
    c: Block(g6)
    c: Block(g7)
    c: Block(g8)
    c: Block(g9)
    c: Block(g10)
    c: Block(g11)
    c: Coincident(g12,g1)
    c: Coincident(g12,g2)
    c: Vertical(g12)
    c: Coincident(g13,g1)
    c: Coincident(g13,g2)
    c: Vertical(g13)
    c: Coincident(g14,g11)
    c: Coincident(g14,g7)
    c: Vertical(g14)
    c: Coincident(g15,g11)
    c: Coincident(g15,g7)
    c: Vertical(g15)
    c: Coincident(g16,g0)
    c: Coincident(g16,g3)
    c: Vertical(g16)
    c: Coincident(g17,g4)
    c: Coincident(g17,g8)
    c: Vertical(g17)
    c: Coincident(g18,g0)
    c: Coincident(g18,g3)
    c: Vertical(g18)
    c: Coincident(g19,g4)
    c: Coincident(g19,g8)
    c: Vertical(g19)
    c: Coincident(g20,g5)
    c: Coincident(g20,g9)
    c: Vertical(g20)
    c: Coincident(g21,g5)
    c: Coincident(g21,g9)
    c: Vertical(g21)
    c: Coincident(g22,g10)
    c: Coincident(g22,g6)
    c: Vertical(g22)
    c: Coincident(g23,g6)
    c: Coincident(g23,g10)
    c: Vertical(g23)
FEATURE [Part::Extrusion] Extrude038  label="removeToCreateFanGrillHoles001"
  Base = -> Sketch047
  Dir = (0,-1,6e-16)
  DirMode = 2
  FaceMakerClass = Part::FaceMakerBullseye
  LengthFwd = 10
  LengthRev = 0
  Placement = pos=(65.4,44,54.82) rot=(0,0,1;0rad)
  Solid = true
  Symmetric = false
FEATURE [Part::Feature] Wire004
  shape: bbox 11 x 5.2 x 2e-07 mm, 0 faces, 0 solids (baked)
FEATURE [Part::Revolution] Revolve095
  Angle = 360
  Axis = (0,1,0)
  Base = (0,0,0)
  FaceMakerClass = Part::FaceMakerBullseye
  Placement = pos=(30.3,38,19.7) rot=(0,0,1;0rad)
  Solid = true
  Source = -> Wire004
  Symmetric = false
FEATURE [Part::Feature] Wire005
  shape: bbox 11 x 5.2 x 2e-07 mm, 0 faces, 0 solids (baked)
FEATURE [Part::Revolution] Revolve096
  Angle = 360
  Axis = (0,1,0)
  Base = (0,0,0)
  FaceMakerClass = Part::FaceMakerBullseye
  Placement = pos=(30.3,38,51.7) rot=(0,0,1;0rad)
  Solid = true
  Source = -> Wire005
  Symmetric = false
FEATURE [Part::Feature] Wire006
  shape: bbox 11 x 5.2 x 2e-07 mm, 0 faces, 0 solids (baked)
FEATURE [Part::Revolution] Revolve097
  Angle = 360
  Axis = (0,1,0)
  Base = (0,0,0)
  FaceMakerClass = Part::FaceMakerBullseye
  Placement = pos=(62.3,38,51.7) rot=(0,0,1;0rad)
  Solid = true
  Source = -> Wire006
  Symmetric = false
FEATURE [Part::Feature] Wire007
  shape: bbox 11 x 5.2 x 2e-07 mm, 0 faces, 0 solids (baked)
FEATURE [Part::Revolution] Revolve098
  Angle = 360
  Axis = (0,1,0)
  Base = (0,0,0)
  FaceMakerClass = Part::FaceMakerBullseye
  Placement = pos=(62.3,38,19.7) rot=(0,0,1;0rad)
  Solid = true
  Source = -> Wire007
  Symmetric = false
FEATURE [Part::MultiFuse] Fusion067  label="fanScrewHousing002"
  Shapes = -> [Revolve098,Revolve097,Revolve096,Revolve095]
FEATURE [Part::Feature] Face091 .. Face094  x4 (patterned run collapsed; names and placements below)
  shape: bbox 3.5 x 17.8 x 2e-07 mm, 1 faces, 0 solids (baked)
FEATURE [Part::Revolution] Revolve099  label="removeToCreateScrewAndThreadedInsertHole026"
  Angle = 360
  Axis = (0,1,0)
  Base = (0,0,0)
  FaceMakerClass = Part::FaceMakerBullseye
  Placement = pos=(62.3,30.3,19.7) rot=(0,0,1;0rad)
  Solid = false
  Source = -> Face091
  Symmetric = false
FEATURE [Part::Revolution] Revolve100  label="removeToCreateScrewAndThreadedInsertHole027"
  Angle = 360
  Axis = (0,1,0)
  Base = (0,0,0)
  FaceMakerClass = Part::FaceMakerBullseye
  Placement = pos=(62.3,30.3,51.7) rot=(0,0,1;0rad)
  Solid = false
  Source = -> Face092
  Symmetric = false
FEATURE [Part::Revolution] Revolve101  label="removeToCreateScrewAndThreadedInsertHole028"
  Angle = 360
  Axis = (0,1,0)
  Base = (0,0,0)
  FaceMakerClass = Part::FaceMakerBullseye
  Placement = pos=(30.3,30.3,19.7) rot=(0,0,1;0rad)
  Solid = false
  Source = -> Face093
  Symmetric = false
FEATURE [Part::Revolution] Revolve102  label="removeToCreateScrewAndThreadedInsertHole029"
  Angle = 360
  Axis = (0,1,0)
  Base = (0,0,0)
  FaceMakerClass = Part::FaceMakerBullseye
  Placement = pos=(30.3,30.3,51.7) rot=(0,0,1;0rad)
  Solid = false
  Source = -> Face094
  Symmetric = false
FEATURE [Part::MultiFuse] Fusion068  label="createThreadedInsertHolesForFan002"
  Shapes = -> [Revolve099,Revolve100,Revolve101,Revolve102]
FEATURE [Part::Cut] Cut026  label="fanScrewHousing003"
  Base = -> Fusion067
  Tool = -> Fusion068
FEATURE [Sketcher::SketchObject] Sketch048
  FullyConstrained = false
  Placement = pos=(0,0,0) rot=(1,0,0;1.5708rad)
  sketch-geometry (24):
    g0: ArcOfCircle CenterX=-4 CenterY=-10.5 CenterZ=0 NormalX=0 NormalY=0 NormalZ=1 AngleXU=0 Radius=1.5 StartAngle=6e-16 EndAngle=3.14159
    g1: ArcOfCircle CenterX=-34.2 CenterY=-10.5 CenterZ=0 NormalX=0 NormalY=0 NormalZ=1 AngleXU=0 Radius=1.5 StartAngle=0 EndAngle=3.14159
    g2: ArcOfCircle CenterX=-34.2 CenterY=-27.7 CenterZ=0 NormalX=0 NormalY=0 NormalZ=1 AngleXU=0 Radius=1.5 StartAngle=3.14159 EndAngle=6.28319
    g3: ArcOfCircle CenterX=-4 CenterY=-27.7 CenterZ=0 NormalX=0 NormalY=0 NormalZ=1 AngleXU=0 Radius=1.5 StartAngle=3.1416 EndAngle=6.28319
    g4: ArcOfCircle CenterX=-10 CenterY=-4.3 CenterZ=0 NormalX=0 NormalY=0 NormalZ=1 AngleXU=0 Radius=1.5 StartAngle=2e-16 EndAngle=3.14159
    g5: ArcOfCircle CenterX=-16.1 CenterY=-1.8 CenterZ=0 NormalX=0 NormalY=0 NormalZ=1 AngleXU=0 Radius=1.5 StartAngle=5e-16 EndAngle=3.14159
    g6: ArcOfCircle CenterX=-22.1 CenterY=-1.8 CenterZ=0 NormalX=0 NormalY=0 NormalZ=1 AngleXU=0 Radius=1.5 StartAngle=5e-16 EndAngle=3.14159
    g7: ArcOfCircle CenterX=-28.2 CenterY=-4.3 CenterZ=0 NormalX=0 NormalY=0 NormalZ=1 AngleXU=0 Radius=1.5 StartAngle=2e-16 EndAngle=3.14159
    g8: ArcOfCircle CenterX=-10 CenterY=-33.9 CenterZ=0 NormalX=0 NormalY=0 NormalZ=1 AngleXU=0 Radius=1.5 StartAngle=3.14159 EndAngle=6.28319
    g9: ArcOfCircle CenterX=-16.1 CenterY=-36.4 CenterZ=0 NormalX=0 NormalY=0 NormalZ=1 AngleXU=0 Radius=1.5 StartAngle=3.14159 EndAngle=6.28319
    g10: ArcOfCircle CenterX=-22.1 CenterY=-36.4 CenterZ=0 NormalX=0 NormalY=0 NormalZ=1 AngleXU=0 Radius=1.5 StartAngle=3.14159 EndAngle=6.28319
    g11: ArcOfCircle CenterX=-28.2 CenterY=-33.9 CenterZ=0 NormalX=0 NormalY=0 NormalZ=1 AngleXU=0 Radius=1.5 StartAngle=3.14159 EndAngle=6.28319
    g12: LineSegment StartX=-35.7 StartY=-10.5 StartZ=0 EndX=-35.7 EndY=-27.7 EndZ=0
    g13: LineSegment StartX=-32.7 StartY=-10.5 StartZ=0 EndX=-32.7 EndY=-27.7 EndZ=0
    g14: LineSegment StartX=-29.7 StartY=-33.9 StartZ=0 EndX=-29.7 EndY=-4.3 EndZ=0
    g15: LineSegment StartX=-26.7 StartY=-33.9 StartZ=0 EndX=-26.7 EndY=-4.3 EndZ=0
    g16: LineSegment StartX=-2.5 StartY=-10.5 StartZ=0 EndX=-2.5 EndY=-27.7 EndZ=0
    g17: LineSegment StartX=-8.5 StartY=-4.3 StartZ=0 EndX=-8.5 EndY=-33.9 EndZ=0
    g18: LineSegment StartX=-5.5 StartY=-10.5 StartZ=0 EndX=-5.5 EndY=-27.7 EndZ=0
    g19: LineSegment StartX=-11.5 StartY=-4.3 StartZ=0 EndX=-11.5 EndY=-33.9 EndZ=0
    g20: LineSegment StartX=-14.6 StartY=-1.8 StartZ=0 EndX=-14.6 EndY=-36.4 EndZ=0
    g21: LineSegment StartX=-17.6 StartY=-1.8 StartZ=0 EndX=-17.6 EndY=-36.4 EndZ=0
    g22: LineSegment StartX=-20.6 StartY=-36.4 StartZ=0 EndX=-20.6 EndY=-1.8 EndZ=0
    g23: LineSegment StartX=-23.6 StartY=-1.8 StartZ=0 EndX=-23.6 EndY=-36.4 EndZ=0
  constraints (48):
    c: Block(g0)
    c: Block(g1)
    c: Block(g2)
    c: Block(g3)
    c: Block(g4)
    c: Block(g5)
    c: Block(g6)
    c: Block(g7)
    c: Block(g8)
    c: Block(g9)
    c: Block(g10)
    c: Block(g11)
    c: Coincident(g12,g1)
    c: Coincident(g12,g2)
    c: Vertical(g12)
    c: Coincident(g13,g1)
    c: Coincident(g13,g2)
    c: Vertical(g13)
    c: Coincident(g14,g11)
    c: Coincident(g14,g7)
    c: Vertical(g14)
    c: Coincident(g15,g11)
    c: Coincident(g15,g7)
    c: Vertical(g15)
    c: Coincident(g16,g0)
    c: Coincident(g16,g3)
    c: Vertical(g16)
    c: Coincident(g17,g4)
    c: Coincident(g17,g8)
    c: Vertical(g17)
    c: Coincident(g18,g0)
    c: Coincident(g18,g3)
    c: Vertical(g18)
    c: Coincident(g19,g4)
    c: Coincident(g19,g8)
    c: Vertical(g19)
    c: Coincident(g20,g5)
    c: Coincident(g20,g9)
    c: Vertical(g20)
    c: Coincident(g21,g5)
    c: Coincident(g21,g9)
    c: Vertical(g21)
    c: Coincident(g22,g10)
    c: Coincident(g22,g6)
    c: Vertical(g22)
    c: Coincident(g23,g6)
    c: Coincident(g23,g10)
    c: Vertical(g23)
FEATURE [Part::Extrusion] Extrude039  label="removeToCreateFanGrillHoles002"
  Base = -> Sketch048
  Dir = (0,-1,6e-16)
  DirMode = 2
  FaceMakerClass = Part::FaceMakerBullseye
  LengthFwd = 10
  LengthRev = 0
  Placement = pos=(65.4,44,54.82) rot=(0,0,1;0rad)
  Solid = true
  Symmetric = false
FEATURE [Part::Cut] Cut027  label="fanScrewHousing004"
  Base = -> Cut026
  Tool = -> Extrude038
FEATURE [Part::Cut] Cut028  label="top014"
  Base = -> Fillet026
  Tool = -> Extrude039
FEATURE [Part::Feature] Face095 .. Face098  x4 (patterned run collapsed; names and placements below)
  shape: bbox 3.5 x 17.8 x 2e-07 mm, 1 faces, 0 solids (baked)
FEATURE [Part::Revolution] Revolve103  label="removeToCreateScrewAndThreadedInsertHole030"
  Angle = 360
  Axis = (0,1,0)
  Base = (0,0,0)
  FaceMakerClass = Part::FaceMakerBullseye
  Placement = pos=(62.3,30.3,19.7) rot=(0,0,1;0rad)
  Solid = false
  Source = -> Face095
  Symmetric = false
FEATURE [Part::Revolution] Revolve104  label="removeToCreateScrewAndThreadedInsertHole031"
  Angle = 360
  Axis = (0,1,0)
  Base = (0,0,0)
  FaceMakerClass = Part::FaceMakerBullseye
  Placement = pos=(62.3,30.3,51.7) rot=(0,0,1;0rad)
  Solid = false
  Source = -> Face096
  Symmetric = false
FEATURE [Part::Revolution] Revolve105  label="removeToCreateScrewAndThreadedInsertHole032"
  Angle = 360
  Axis = (0,1,0)
  Base = (0,0,0)
  FaceMakerClass = Part::FaceMakerBullseye
  Placement = pos=(30.3,30.3,19.7) rot=(0,0,1;0rad)
  Solid = false
  Source = -> Face097
  Symmetric = false
FEATURE [Part::Revolution] Revolve106  label="removeToCreateScrewAndThreadedInsertHole033"
  Angle = 360
  Axis = (0,1,0)
  Base = (0,0,0)
  FaceMakerClass = Part::FaceMakerBullseye
  Placement = pos=(30.3,30.3,51.7) rot=(0,0,1;0rad)
  Solid = false
  Source = -> Face098
  Symmetric = false
FEATURE [Part::MultiFuse] Fusion069  label="createThreadedInsertHolesForFan003"
  Shapes = -> [Revolve103,Revolve104,Revolve105,Revolve106]
FEATURE [Part::Cut] Cut029  label="top015"
  Base = -> Cut028
  Tool = -> Fusion054
FEATURE [Part::Cut] Cut030  label="fanScrewHousing005"
  Base = -> Cut027
  Tool = -> Fusion069
FEATURE [Part::Cylinder] Cylinder026  label="removeToCreteHoleForPlugHousing010"
  Angle = 360
  AttacherType = Attacher::AttachEngine3D
  Height = 20
  Placement = pos=(-2,19,36) rot=(0,1,0;1.5708rad)
  Radius = 14.3
FEATURE [Part::Box] Box018  label="removeToCreteHoleForPlugHousing011"
  AttacherType = Attacher::AttachEngine3D
  Height = 28.6
  Length = 10
  Placement = pos=(-2,0,21.7) rot=(0,0,1;0rad)
  Width = 19
FEATURE [Part::Box] Box019  label="wireHolderBottomCaseBit"
  AttacherType = Attacher::AttachEngine3D
  Height = 28
  Length = 3
  Placement = pos=(0,0,22) rot=(0,0,1;0rad)
  Width = 21
FEATURE [Part::Cylinder] Cylinder027  label="removeToCreteHoleForPlugHousing012"
  Angle = 360
  AttacherType = Attacher::AttachEngine3D
  Height = 20
  Placement = pos=(-2,19,36) rot=(0,1,0;1.5708rad)
  Radius = 14.3
FEATURE [Part::Cut] Cut031  label="wireHolderBottomCaseBit001"
  Base = -> Box019
  Tool = -> Cylinder027
FEATURE [Part::MultiFuse] Fusion070  label="removeToCreteHoleForPlugHousing013"
  Shapes = -> [Box018,Cylinder026]
FEATURE [Part::Cut] Cut032  label="top016"
  Base = -> Cut029
  Tool = -> Fusion070
FEATURE [Part::Cylinder] Cylinder028
  Angle = 360
  AttacherType = Attacher::AttachEngine3D
  Height = 20
  Placement = pos=(0,0,36.15) rot=(0,0,1;0rad)
  Radius = 14.3
FEATURE [Part::Cylinder] Cylinder029
  Angle = 360
  AttacherType = Attacher::AttachEngine3D
  Height = 10
  Placement = pos=(0,0,36.15) rot=(0,0,1;0rad)
  Radius = 4
FEATURE [Part::MultiFuse] Fusion071  label="removeToCreteHoleForPlugHousing014"
  Placement = pos=(70,19,36) rot=(0,1,0;1.5708rad)
  Shapes = -> [Cylinder028,Cylinder029]
FEATURE [Sketcher::SketchObject] Sketch049  label="topSketch011"
  FullyConstrained = false
  sketch-geometry (4):
    g0: ArcOfCircle CenterX=105 CenterY=19 CenterZ=0 NormalX=0 NormalY=0 NormalZ=1 AngleXU=0 Radius=16 StartAngle=5.54125 EndAngle=6.28319
    g1: ArcOfCircle CenterX=105 CenterY=19 CenterZ=0 NormalX=0 NormalY=0 NormalZ=1 AngleXU=0 Radius=19 StartAngle=5.54125 EndAngle=6.28319
    g2: LineSegment StartX=116.795 StartY=8.18859 StartZ=0 EndX=119.006 EndY=6.16145 EndZ=0
    g3: LineSegment StartX=121 StartY=19 StartZ=0 EndX=124 EndY=19 EndZ=0
  constraints (9):
    c: Block(g0)
    c: Block(g2)
    c: Block(g1)
    c: Coincident(g2,g1)
    c: Coincident(g2,g0)
    c: Coincident(g3,g0)
    c: Coincident(g3,g1)
    c: Horizontal(g3)
    c: Block(g3)
FEATURE [Part::Box] Box020  label="removeToCreteHoleForPlugHousing015"
  AttacherType = Attacher::AttachEngine3D
  Height = 28.6
  Length = 20
  Placement = pos=(106.15,0,21.7) rot=(0,0,1;0rad)
  Width = 19
FEATURE [Part::MultiFuse] Fusion072  label="removeToCreteHoleForPlugHousing016"
  Shapes = -> [Box020,Fusion071]
FEATURE [Part::Cut] Cut033  label="removeToCreteHoleForPlugHousing017"
  Base = -> Cut032
  Tool = -> Fusion072
FEATURE [Part::Cylinder] Cylinder030
  Angle = 360
  AttacherType = Attacher::AttachEngine3D
  Height = 20
  Placement = pos=(0,0,36.15) rot=(0,0,1;0rad)
  Radius = 14.3
FEATURE [Part::Cylinder] Cylinder031
  Angle = 360
  AttacherType = Attacher::AttachEngine3D
  Height = 10
  Placement = pos=(0,0,36.15) rot=(0,0,1;0rad)
  Radius = 4
FEATURE [Part::Box] Box021  label="removeToCreteHoleForPlugHousing019"
  AttacherType = Attacher::AttachEngine3D
  Height = 28.6
  Length = 20
  Placement = pos=(106.15,0,21.7) rot=(0,0,1;0rad)
  Width = 19
FEATURE [Part::MultiFuse] Fusion074  label="removeToCreteHoleForPlugHousing020"
  Placement = pos=(70,19,36) rot=(0,1,0;1.5708rad)
  Shapes = -> [Cylinder030,Cylinder031]
FEATURE [Part::MultiFuse] Fusion073  label="removeToCreteHoleForPlugHousing018"
  Placement = pos=(0,0,28.3) rot=(0,0,1;0rad)
  Shapes = -> [Box021,Fusion074]
FEATURE [Part::Cylinder] Cylinder032
  Angle = 360
  AttacherType = Attacher::AttachEngine3D
  Height = 20
  Placement = pos=(0,0,36.15) rot=(0,0,1;0rad)
  Radius = 14.3
FEATURE [Part::Cylinder] Cylinder033
  Angle = 360
  AttacherType = Attacher::AttachEngine3D
  Height = 10
  Placement = pos=(0,0,36.15) rot=(0,0,1;0rad)
  Radius = 4
FEATURE [Part::Box] Box022  label="removeToCreteHoleForPlugHousing021"
  AttacherType = Attacher::AttachEngine3D
  Height = 28.6
  Length = 20
  Placement = pos=(106.15,0,21.7) rot=(0,0,1;0rad)
  Width = 19
FEATURE [Part::MultiFuse] Fusion076  label="removeToCreteHoleForPlugHousing023"
  Placement = pos=(70,19,36) rot=(0,1,0;1.5708rad)
  Shapes = -> [Cylinder032,Cylinder033]
FEATURE [Part::MultiFuse] Fusion075  label="removeToCreteHoleForPlugHousing022"
  Placement = pos=(0,0,-28.3) rot=(0,0,1;0rad)
  Shapes = -> [Box022,Fusion076]
FEATURE [Part::MultiFuse] Fusion077  label="removeToCreatePlugHousingBottomBit"
  Shapes = -> [Fusion075,Fusion073]
FEATURE [Part::Cylinder] Cylinder034
  Angle = 360
  AttacherType = Attacher::AttachEngine3D
  Height = 20
  Placement = pos=(0,0,36.15) rot=(0,0,1;0rad)
  Radius = 14.3
FEATURE [Part::Cylinder] Cylinder035
  Angle = 360
  AttacherType = Attacher::AttachEngine3D
  Height = 10
  Placement = pos=(0,0,36.15) rot=(0,0,1;0rad)
  Radius = 4
FEATURE [Part::MultiFuse] Fusion078  label="removeToCreteHoleForPlugHousing024"
  Placement = pos=(70,19,36) rot=(0,1,0;1.5708rad)
  Shapes = -> [Cylinder034,Cylinder035]
FEATURE [Part::MultiFuse] Fusion079  label="removeToCreatePlugHousingBottomBit001"
  Shapes = -> [Fusion078,Fusion077]
FEATURE [Part::Extrusion] Extrude040  label="bottomPlugHousingBit"
  Base = -> Sketch049
  Dir = (0,0,1)
  DirMode = 2
  FaceMakerClass = Part::FaceMakerBullseye
  LengthFwd = 72
  LengthRev = 0
  Solid = true
  Symmetric = false
FEATURE [Part::Cut] Cut034  label="bottomPlugHousingBit001"
  Base = -> Extrude040
  Tool = -> Fusion079
FEATURE [Part::Box] Box023  label="Cube014"
  AttacherType = Attacher::AttachEngine3D
  Height = 16
  Length = 8
  Placement = pos=(12.7,31.52,28) rot=(0,0,1;0rad)
  Width = 4
FEATURE [Part::Cylinder] Cylinder036
  Angle = 360
  AttacherType = Attacher::AttachEngine3D
  Height = 10
  Placement = pos=(0,0,36.15) rot=(0,0,1;0rad)
  Radius = 4
FEATURE [Part::Cylinder] Cylinder037
  Angle = 360
  AttacherType = Attacher::AttachEngine3D
  Height = 20
  Placement = pos=(0,0,36.15) rot=(0,0,1;0rad)
  Radius = 8.2
FEATURE [Part::MultiFuse] Fusion080  label="removeToCreteHoleForPlugHousing025"
  Placement = pos=(-42,19,36) rot=(0,1,0;1.5708rad)
  Shapes = -> [Cylinder037,Cylinder036]
FEATURE [Sketcher::SketchObject] Sketch050  label="topSketch012"
  FullyConstrained = true
  sketch-geometry (4):
    g0: LineSegment StartX=16.8446 StartY=31.512 StartZ=0 EndX=16.3251 EndY=34.4666 EndZ=0
    g1: ArcOfCircle CenterX=19 CenterY=19.2524 CenterZ=0 NormalX=0 NormalY=0 NormalZ=1 AngleXU=0 Radius=15.4476 StartAngle=1.74483 EndAngle=2.72717
    g2: ArcOfCircle CenterX=19 CenterY=19.2524 CenterZ=0 NormalX=0 NormalY=0 NormalZ=1 AngleXU=0 Radius=12.4476 StartAngle=1.74483 EndAngle=2.73189
    g3: LineSegment StartX=4.86004 StartY=25.4725 StartZ=0 EndX=7.58253 EndY=24.2107 EndZ=0
  constraints (7):
    c: Block(g0)
    c: Coincident(g1,g0)
    c: Coincident(g2,g0)
    c: Coincident(g3,g1)
    c: Coincident(g3,g2)
    c: Block(g1)
    c: Block(g2)
FEATURE [Part::Extrusion] Extrude041
  Base = -> Sketch050
  Dir = (0,0,1)
  DirMode = 2
  FaceMakerClass = Part::FaceMakerBullseye
  LengthFwd = 10.6
  LengthRev = 0
  Placement = pos=(0,0,31) rot=(0,0,1;0rad)
  Solid = true
  Symmetric = false
FEATURE [Part::Cut] Cut035
  Base = -> Extrude041
  Placement = pos=(0,0,-0.3) rot=(0,0,1;0rad)
  Tool = -> Fusion080
FEATURE [Part::Cut] Cut036
  Base = -> Box023
  Tool = -> Cut035
FEATURE [Part::Fillet] Fillet027
  Base = -> Cut036
  Edges = 1 edges r=0.7: [Edge13]
FEATURE [Part::Fillet] Fillet028
  Base = -> Fillet027
  Edges = 1 edges r=0.7: [Edge13]
FEATURE [Part::Fillet] Fillet029
  Base = -> Fillet028
  Edges = 1 edges r=0.7: [Edge16]
FEATURE [Part::Fillet] Fillet030
  Base = -> Fillet029
  Edges = 1 edges r=0.7: [Edge11]
FEATURE [Part::Fillet] Fillet031
  Base = -> Fillet030
  Edges = 1 edges r=0.7: [Edge10]
FEATURE [Part::Fillet] Fillet032
  Base = -> Fillet031
  Edges = 1 edges r=1.2: [Edge5]
FEATURE [Part::Fillet] Fillet033
  Base = -> Fillet032
  Edges = 1 edges r=1.2: [Edge12]
FEATURE [Part::Fillet] Fillet034  label="wireHousingRetainer"
  Base = -> Fillet033
  Edges = 1 edges r=2: [Edge1]
  Placement = pos=(0.3,0,0) rot=(0,0,1;0rad)
FEATURE [Part::Feature] Face099
  shape: bbox 3.5 x 17.8 x 2e-07 mm, 1 faces, 0 solids (baked)
FEATURE [Part::Revolution] Revolve107  label="removeToCreateScrewAndThreadedInsertHole034"
  Angle = 360
  Axis = (0,1,0)
  Base = (0,0,0)
  FaceMakerClass = Part::FaceMakerBullseye
  Placement = pos=(12.5,0,10) rot=(0,0,1;0rad)
  Solid = false
  Source = -> Face099
  Symmetric = false
FEATURE [Part::Feature] Face100
  shape: bbox 3.5 x 17.8 x 2e-07 mm, 1 faces, 0 solids (baked)
FEATURE [Part::Revolution] Revolve108  label="removeToCreateScrewAndThreadedInsertHole035"
  Angle = 360
  Axis = (0,1,0)
  Base = (0,0,0)
  FaceMakerClass = Part::FaceMakerBullseye
  Placement = pos=(12.5,0,62) rot=(0,0,1;0rad)
  Solid = false
  Source = -> Face100
  Symmetric = false
FEATURE [Part::Feature] Face101
  shape: bbox 3.5 x 17.8 x 2e-07 mm, 1 faces, 0 solids (baked)
FEATURE [Part::Revolution] Revolve109  label="removeToCreateScrewAndThreadedInsertHole036"
  Angle = 360
  Axis = (0,1,0)
  Base = (0,0,0)
  FaceMakerClass = Part::FaceMakerBullseye
  Placement = pos=(89.5,0,68.5) rot=(0,0,1;0rad)
  Solid = false
  Source = -> Face101
  Symmetric = false
FEATURE [Part::Feature] Face102
  shape: bbox 3.5 x 17.8 x 2e-07 mm, 1 faces, 0 solids (baked)
FEATURE [Part::Revolution] Revolve110  label="removeToCreateScrewAndThreadedInsertHole037"
  Angle = 360
  Axis = (0,1,0)
  Base = (0,0,0)
  FaceMakerClass = Part::FaceMakerBullseye
  Placement = pos=(89.5,0,3.5) rot=(0,0,1;0rad)
  Solid = false
  Source = -> Face102
  Symmetric = false
FEATURE [Part::Feature] Face103
  shape: bbox 3.5 x 17.8 x 2e-07 mm, 1 faces, 0 solids (baked)
FEATURE [Part::Revolution] Revolve111  label="removeToCreateScrewAndThreadedInsertHole038"
  Angle = 360
  Axis = (0,1,0)
  Base = (0,0,0)
  FaceMakerClass = Part::FaceMakerBullseye
  Placement = pos=(109.5,4.7,3.5) rot=(0,0,1;0rad)
  Solid = false
  Source = -> Face103
  Symmetric = false
FEATURE [Part::Feature] Face104
  shape: bbox 3.5 x 17.8 x 2e-07 mm, 1 faces, 0 solids (baked)
FEATURE [Part::Revolution] Revolve112  label="removeToCreateScrewAndThreadedInsertHole039"
  Angle = 360
  Axis = (0,1,0)
  Base = (0,0,0)
  FaceMakerClass = Part::FaceMakerBullseye
  Placement = pos=(109.5,4.7,68.5) rot=(0,0,1;0rad)
  Solid = false
  Source = -> Face104
  Symmetric = false
FEATURE [Part::MultiFuse] Fusion081  label="removeToCreateScrewAndThreadedInsertHole040"
  Shapes = -> [Revolve107,Revolve108,Revolve109,Revolve110,Revolve111,Revolve112]
FEATURE [Part::MultiFuse] Fusion082  label="casePillars002"
  Shapes = -> [Revolve094,Revolve092,Revolve090,Revolve089,Revolve091,Revolve093]
FEATURE [Part::Cut] Cut037  label="casePillars003"
  Base = -> Fusion082
  Tool = -> Fusion081
FEATURE [Sketcher::SketchObject] Sketch051
  FullyConstrained = true
  Placement = pos=(117,19,0) rot=(0.57735,0.57735,0.57735;2.0944rad)
  sketch-geometry (48):
    g0: LineSegment StartX=-49.19 StartY=69.25 StartZ=0 EndX=-49.19 EndY=66.25 EndZ=0
    g1: LineSegment StartX=-49.19 StartY=63.5 StartZ=0 EndX=-49.19 EndY=60.5 EndZ=0
    g2: LineSegment StartX=-49.19 StartY=57.75 StartZ=0 EndX=-49.19 EndY=54.75 EndZ=0
    g3: LineSegment StartX=-49.19 StartY=52 StartZ=0 EndX=-49.19 EndY=49 EndZ=0
    g4: LineSegment StartX=-49.19 StartY=46.25 StartZ=0 EndX=-49.19 EndY=43.25 EndZ=0
    g5: LineSegment StartX=-49.19 StartY=40.5 StartZ=0 EndX=-49.19 EndY=37.5 EndZ=0
    g6: LineSegment StartX=-49.19 StartY=34.5 StartZ=0 EndX=-49.19 EndY=31.5 EndZ=0
    g7: LineSegment StartX=-49.19 StartY=28.75 StartZ=0 EndX=-49.19 EndY=25.75 EndZ=0
    g8: LineSegment StartX=-49.19 StartY=23 StartZ=0 EndX=-49.19 EndY=20 EndZ=0
    g9: LineSegment StartX=-49.19 StartY=17.25 StartZ=0 EndX=-49.19 EndY=14.25 EndZ=0
    g10: LineSegment StartX=-49.19 StartY=11.5 StartZ=0 EndX=-49.19 EndY=8.5 EndZ=0
    g11: LineSegment StartX=-49.19 StartY=5.75 StartZ=0 EndX=-49.19 EndY=2.75 EndZ=0
    g12: ArcOfCircle CenterX=-1.5 CenterY=67.75 CenterZ=0 NormalX=0 NormalY=0 NormalZ=1 AngleXU=0 Radius=1.5 StartAngle=4.71239 EndAngle=7.85398
    g13: ArcOfCircle CenterX=-1.5 CenterY=62 CenterZ=0 NormalX=0 NormalY=0 NormalZ=1 AngleXU=0 Radius=1.5 StartAngle=4.71239 EndAngle=7.85398
    g14: ArcOfCircle CenterX=-1.5 CenterY=56.25 CenterZ=0 NormalX=0 NormalY=0 NormalZ=1 AngleXU=0 Radius=1.5 StartAngle=4.71239 EndAngle=7.85398
    g15: ArcOfCircle CenterX=-11.49 CenterY=50.5 CenterZ=0 NormalX=0 NormalY=0 NormalZ=1 AngleXU=0 Radius=1.5 StartAngle=4.71239 EndAngle=7.85398
    g16: ArcOfCircle CenterX=-16.28 CenterY=44.75 CenterZ=0 NormalX=0 NormalY=0 NormalZ=1 AngleXU=0 Radius=1.5 StartAngle=4.71239 EndAngle=7.85398
    g17: ArcOfCircle CenterX=-18.2337 CenterY=39 CenterZ=0 NormalX=0 NormalY=0 NormalZ=1 AngleXU=0 Radius=1.5 StartAngle=4.71485 EndAngle=7.85398
    g18: ArcOfCircle CenterX=-16.2837 CenterY=27.25 CenterZ=0 NormalX=0 NormalY=0 NormalZ=1 AngleXU=0 Radius=1.5 StartAngle=4.71485 EndAngle=7.85398
    g19: ArcOfCircle CenterX=-18.2337 CenterY=33 CenterZ=0 NormalX=0 NormalY=0 NormalZ=1 AngleXU=0 Radius=1.5 StartAngle=4.71485 EndAngle=7.85398
    g20: ArcOfCircle CenterX=-11.49 CenterY=21.5 CenterZ=0 NormalX=0 NormalY=0 NormalZ=1 AngleXU=0 Radius=1.5 StartAngle=4.71239 EndAngle=7.85398
    g21: ArcOfCircle CenterX=-1.5 CenterY=4.25 CenterZ=0 NormalX=0 NormalY=0 NormalZ=1 AngleXU=0 Radius=1.5 StartAngle=4.71239 EndAngle=7.85398
    g22: ArcOfCircle CenterX=-1.5 CenterY=10 CenterZ=0 NormalX=0 NormalY=0 NormalZ=1 AngleXU=0 Radius=1.5 StartAngle=4.71239 EndAngle=7.85398
    g23: ArcOfCircle CenterX=-1.5 CenterY=15.75 CenterZ=0 NormalX=0 NormalY=0 NormalZ=1 AngleXU=0 Radius=1.5 StartAngle=4.71239 EndAngle=7.85398
    g24: LineSegment StartX=-49.19 StartY=69.25 StartZ=0 EndX=-1.5 EndY=69.25 EndZ=0
    g25: LineSegment StartX=-49.19 StartY=66.25 StartZ=0 EndX=-1.5 EndY=66.25 EndZ=0
    g26: LineSegment StartX=-49.19 StartY=63.5 StartZ=0 EndX=-1.5 EndY=63.5 EndZ=0
    g27: LineSegment StartX=-49.19 StartY=60.5 StartZ=0 EndX=-1.5 EndY=60.5 EndZ=0
    g28: LineSegment StartX=-49.19 StartY=57.75 StartZ=0 EndX=-1.5 EndY=57.75 EndZ=0
    g29: LineSegment StartX=-49.19 StartY=54.75 StartZ=0 EndX=-1.5 EndY=54.75 EndZ=0
    g30: LineSegment StartX=-49.19 StartY=52 StartZ=0 EndX=-11.49 EndY=52 EndZ=0
    g31: LineSegment StartX=-49.19 StartY=49 StartZ=0 EndX=-11.49 EndY=49 EndZ=0
    g32: LineSegment StartX=-49.19 StartY=46.25 StartZ=0 EndX=-16.28 EndY=46.25 EndZ=0
    g33: LineSegment StartX=-49.19 StartY=43.25 StartZ=0 EndX=-16.28 EndY=43.25 EndZ=0
    g34: LineSegment StartX=-49.19 StartY=40.5 StartZ=0 EndX=-18.2337 EndY=40.5 EndZ=0
    g35: LineSegment StartX=-49.19 StartY=37.5 StartZ=0 EndX=-18.23 EndY=37.5 EndZ=0
    g36: LineSegment StartX=-49.19 StartY=34.5 StartZ=0 EndX=-18.2337 EndY=34.5 EndZ=0
    g37: LineSegment StartX=-49.19 StartY=31.5 StartZ=0 EndX=-18.23 EndY=31.5 EndZ=0
    g38: LineSegment StartX=-49.19 StartY=28.75 StartZ=0 EndX=-16.2837 EndY=28.75 EndZ=0
    g39: LineSegment StartX=-49.19 StartY=25.75 StartZ=0 EndX=-16.28 EndY=25.75 EndZ=0
    g40: LineSegment StartX=-49.19 StartY=23 StartZ=0 EndX=-11.49 EndY=23 EndZ=0
    g41: LineSegment StartX=-49.19 StartY=20 StartZ=0 EndX=-11.49 EndY=20 EndZ=0
    g42: LineSegment StartX=-49.19 StartY=17.25 StartZ=0 EndX=-1.5 EndY=17.25 EndZ=0
    g43: LineSegment StartX=-49.19 StartY=14.25 StartZ=0 EndX=-1.5 EndY=14.25 EndZ=0
    g44: LineSegment StartX=-49.19 StartY=11.5 StartZ=0 EndX=-1.5 EndY=11.5 EndZ=0
    g45: LineSegment StartX=-49.19 StartY=8.5 StartZ=0 EndX=-1.5 EndY=8.5 EndZ=0
    g46: LineSegment StartX=-49.19 StartY=5.75 StartZ=0 EndX=-1.5 EndY=5.75 EndZ=0
    g47: LineSegment StartX=-49.19 StartY=2.75 StartZ=0 EndX=-1.5 EndY=2.75 EndZ=0
  constraints (120):
    c: Vertical(g0)
    c: Distance(g0) = 3
    c: Block(g0)
    c: Vertical(g1)
    c: Distance(g1) = 3
    c: Vertical(g2)
    c: Equal(g0,g2) = 3
    c: Block(g2)
    c: Vertical(g3)
    c: Equal(g1,g3) = 3
    c: Vertical(g4)
    c: Equal(g0,g4) = 3
    c: Block(g4)
    c: Vertical(g5)
    c: Equal(g1,g5) = 3
    c: Vertical(g6)
    c: Equal(g0,g6) = 3
    c: Block(g6)
    c: Vertical(g7)
    c: Equal(g1,g7) = 3
    c: Vertical(g8)
    c: Equal(g0,g8) = 3
    c: Block(g8)
    c: Vertical(g9)
    c: Equal(g1,g9) = 3
    c: Vertical(g10)
    c: Equal(g0,g10) = 3
    c: Block(g10)
    c: Vertical(g11)
    c: Equal(g1,g11) = 3
    c: Block(g12)
    c: Block(g13)
    c: Block(g14)
    c: Block(g15)
    c: Block(g16)
    c: Block(g17)
    c: Block(g18)
    c: Block(g19)
    c: Block(g20)
    c: Block(g21)
    c: Block(g22)
    c: Block(g23)
    c: Block(g11)
    c: Block(g9)
    c: Block(g7)
    c: Block(g5)
    c: Block(g3)
    c: Block(g1)
    c: Coincident(g24,g0)
    c: Coincident(g24,g12)
    c: Horizontal(g24)
    c: Coincident(g25,g0)
    c: Coincident(g25,g12)
    c: Horizontal(g25)
    c: Coincident(g26,g1)
    c: Coincident(g26,g13)
    c: Horizontal(g26)
    c: Coincident(g27,g1)
    c: Coincident(g27,g13)
    c: Horizontal(g27)
    c: Coincident(g28,g2)
    c: Coincident(g28,g14)
    c: Horizontal(g28)
    c: Coincident(g29,g2)
    c: Coincident(g29,g14)
    c: Horizontal(g29)
    c: Coincident(g30,g3)
    c: Coincident(g30,g15)
    c: Horizontal(g30)
    c: Coincident(g31,g3)
    c: Coincident(g31,g15)
    c: Horizontal(g31)
    c: Coincident(g32,g4)
    c: Coincident(g32,g16)
    c: Horizontal(g32)
    c: Coincident(g33,g4)
    c: Coincident(g33,g16)
    c: Horizontal(g33)
    c: Coincident(g34,g5)
    c: Coincident(g34,g17)
    c: Horizontal(g34)
    c: Coincident(g35,g5)
    c: Coincident(g35,g17)
    c: Horizontal(g35)
    c: Coincident(g36,g6)
    c: Coincident(g36,g19)
    c: Horizontal(g36)
    c: Coincident(g37,g6)
    c: Coincident(g37,g19)
    c: Horizontal(g37)
    c: Coincident(g38,g7)
    c: Coincident(g38,g18)
    c: Horizontal(g38)
    c: Coincident(g39,g7)
    c: Coincident(g39,g18)
    c: Horizontal(g39)
    c: Coincident(g40,g8)
    c: Coincident(g40,g20)
    c: Horizontal(g40)
    c: Coincident(g41,g8)
    c: Coincident(g41,g20)
    c: Horizontal(g41)
    c: Coincident(g42,g9)
    c: Coincident(g42,g23)
    c: Horizontal(g42)
    c: Coincident(g43,g9)
    c: Coincident(g43,g23)
    c: Horizontal(g43)
    c: Coincident(g44,g10)
    c: Coincident(g44,g22)
    c: Horizontal(g44)
    c: Coincident(g45,g10)
    c: Coincident(g45,g22)
    c: Horizontal(g45)
    c: Coincident(g46,g11)
    c: Coincident(g46,g21)
    c: Horizontal(g46)
    c: Coincident(g47,g11)
    c: Coincident(g47,g21)
    c: Horizontal(g47)
FEATURE [Part::Extrusion] Extrude042
  Base = -> Sketch051
  Dir = (1,-2e-16,2e-16)
  DirMode = 2
  FaceMakerClass = Part::FaceMakerBullseye
  LengthFwd = 19
  LengthRev = 0
  Placement = pos=(-19,0,0) rot=(0,0,1;0rad)
  Solid = true
  Symmetric = false
FEATURE [Part::Fillet] Fillet035  label="removeToCreateVentalationHoles"
  Base = -> Extrude042
  Edges = <same value as first occurrence — deduplicated (x3 in doc)>
  Placement = pos=(7,0,0) rot=(0,0,1;0rad)
FEATURE [Part::Cut] Cut038  label="top017"
  Base = -> Cut033
  Tool = -> Fillet035
FEATURE [Sketcher::SketchObject] Sketch052  label="bottomSketch001"
  FullyConstrained = true
  sketch-geometry (26):
    g0: LineSegment StartX=6.29999 StartY=8 StartZ=0 EndX=3.29999 EndY=8 EndZ=0
    g1: LineSegment StartX=3.29999 StartY=8 StartZ=0 EndX=3.29999 EndY=-6.03275e-07 EndZ=0
    g2: ArcOfCircle CenterX=8.29999 CenterY=5 CenterZ=0 NormalX=0 NormalY=0 NormalZ=1 AngleXU=0 Radius=2 StartAngle=3.14159 EndAngle=4.71239
    g3: LineSegment StartX=6.29999 StartY=8 StartZ=0 EndX=6.29999 EndY=5 EndZ=0
    g4: ArcOfCircle CenterX=105 CenterY=19 CenterZ=0 NormalX=0 NormalY=0 NormalZ=1 AngleXU=0 Radius=12.7 StartAngle=4.71239 EndAngle=6.28319
    g5-g11: Circle x7 (B-spline internal-alignment scaffolding for g12; pole/knot coordinates omitted)
    g12: BSplineCurve PolesCount=7 KnotsCount=5 Degree=3 IsPeriodic=0
    g13-g17: GeomPoint x5 (B-spline internal-alignment scaffolding for g12; pole/knot coordinates omitted)
    g18: ArcOfCircle CenterX=105 CenterY=19 CenterZ=0 NormalX=0 NormalY=0 NormalZ=1 AngleXU=0 Radius=15.7 StartAngle=5.81226 EndAngle=6.28319
    g19: LineSegment StartX=117.7 StartY=19 StartZ=0 EndX=120.7 EndY=19 EndZ=0
    g20: BSplineCurve PolesCount=5 KnotsCount=3 Degree=3 IsPeriodic=0
    g21: LineSegment StartX=8.29999 StartY=3 StartZ=0 EndX=101.7 EndY=3 EndZ=0
    g22: LineSegment StartX=3.29999 StartY=-6.03275e-07 StartZ=0 EndX=105 EndY=-6.03275e-07 EndZ=0
    g23: LineSegment StartX=120.974 StartY=8.71251 StartZ=0 EndX=122.332 EndY=7.83778 EndZ=0
    g24: LineSegment StartX=105 StartY=-6.03274e-07 StartZ=0 EndX=113 EndY=-6.03274e-07 EndZ=0
    g25: ArcOfCircle CenterX=105 CenterY=19 CenterZ=0 NormalX=0 NormalY=0 NormalZ=1 AngleXU=0 Radius=20.6155 StartAngle=5.11091 EndAngle=5.71103
  constraints (38):
    c: Horizontal(g0)
    c: Distance(g0) = 3
    c: Coincident(g1,g0)
    c: Vertical(g1)
    c: Block(g2)
    c: Block(g0)
    c: Coincident(g3,g0)
    c: Coincident(g3,g2)
    c: Vertical(g3)
    c: Block(g1)
    c: Block(g4)
    c: Coincident(g20,g4)
    c: Block(g20)
    c: Equal(g5, g6-g11) x6
    c: InternalAlignment(g5-g11 -> g12) x7
    c: InternalAlignment(g13-g17 -> g12) x5
    c: Block(g12)
    c: Coincident(g18,g12)
    c: Coincident(g19,g4)
    c: Coincident(g19,g18)
    c: Horizontal(g19)
    c: Block(g19)
    c: Block(g18)
    c: Coincident(g21,g2)
    c: Coincident(g21,g20)
    c: Horizontal(g21)
    c: Distance(g21) = 93.4
    c: Coincident(g22,g1)
    c: Horizontal(g22)
    c: Distance(g22) = 101.7
    c: Horizontal(g24)
    c: Distance(g24) = 8
    c: Coincident(g25,g24)
    c: Block(g24)
    c: Coincident(g23,g25)
    c: Block(g25)
    c: Block(g23)
    c: Distance(g23) = 1.61553
FEATURE [Part::Extrusion] Extrude043  label="bottom010"
  Base = -> Sketch052
  Dir = (0,0,1)
  DirMode = 2
  FaceMakerClass = Part::FaceMakerBullseye
  LengthFwd = 71.4
  LengthRev = 0
  Placement = pos=(0,0,0.3) rot=(0,0,1;0rad)
  Solid = true
  Symmetric = false
FEATURE [Sketcher::SketchObject] Sketch053  label="topSketch013"
  FullyConstrained = true
  sketch-geometry (22):
    g0: LineSegment StartX=5.21097e-06 StartY=3 StartZ=0 EndX=5.21097e-06 EndY=19 EndZ=0
    g1: ArcOfCircle CenterX=19 CenterY=19 CenterZ=0 NormalX=0 NormalY=0 NormalZ=1 AngleXU=0 Radius=19 StartAngle=1.5708 EndAngle=3.14159
    g2: ArcOfCircle CenterX=19 CenterY=19 CenterZ=0 NormalX=0 NormalY=0 NormalZ=1 AngleXU=0 Radius=16 StartAngle=1.5708 EndAngle=3.14159
    g3: LineSegment StartX=114 StartY=35 StartZ=0 EndX=19 EndY=35 EndZ=0
    g4: LineSegment StartX=5.21097e-06 StartY=3 StartZ=0 EndX=5.21097e-06 EndY=0 EndZ=0
    g5: LineSegment StartX=3 StartY=0 StartZ=0 EndX=5.21097e-06 EndY=0 EndZ=0
    g6: LineSegment StartX=3 StartY=19 StartZ=0 EndX=3 EndY=0 EndZ=0
    g7: LineSegment StartX=19 StartY=38 StartZ=0 EndX=124 EndY=38 EndZ=0
    g8: Circle CenterX=119 CenterY=35 CenterZ=0 NormalX=0 NormalY=0 NormalZ=1 AngleXU=0 Radius=1
    g9: Circle CenterX=121 CenterY=35 CenterZ=0 NormalX=0 NormalY=0 NormalZ=1 AngleXU=0 Radius=1
    g10: Circle CenterX=121 CenterY=33 CenterZ=0 NormalX=0 NormalY=0 NormalZ=1 AngleXU=0 Radius=1
    g11: BSplineCurve PolesCount=3 KnotsCount=2 Degree=2 IsPeriodic=0
    g12: GeomPoint X=119 Y=35 Z=0
    g13: GeomPoint X=121 Y=33 Z=0
    g14: LineSegment StartX=119 StartY=35 StartZ=0 EndX=114 EndY=35 EndZ=0
    g15: ArcOfCircle CenterX=105 CenterY=19 CenterZ=0 NormalX=0 NormalY=0 NormalZ=1 AngleXU=0 Radius=16 StartAngle=5.60905 EndAngle=6.28319
    g16: LineSegment StartX=121 StartY=33 StartZ=0 EndX=121 EndY=19 EndZ=0
    g17: LineSegment StartX=117.5 StartY=9.01251 StartZ=0 EndX=121.163 EndY=9.0125 EndZ=0
    g18: ArcOfCircle CenterX=105 CenterY=19 CenterZ=0 NormalX=0 NormalY=0 NormalZ=1 AngleXU=0 Radius=20.6155 StartAngle=5.7297 EndAngle=6.28319
    g19: LineSegment StartX=121.163 StartY=9.0125 StartZ=0 EndX=122.538 EndY=8.16329 EndZ=0
    g20: LineSegment StartX=124 StartY=38 StartZ=0 EndX=125.616 EndY=38 EndZ=0
    g21: LineSegment StartX=125.616 StartY=19 StartZ=0 EndX=125.616 EndY=38 EndZ=0
  constraints (49):
    c: Vertical(g0)
    c: Block(g0)
    c: Coincident(g1,g0)
    c: Block(g1)
    c: Coincident(g2,g1)
    c: Block(g2)
    c: Coincident(g3,g2)
    c: Horizontal(g3)
    c: Tangent(g3,g2)
    c: Coincident(g4,g0)
    c: Distance(g4) = 3
    c: Vertical(g4)
    c: Coincident(g5,g4)
    c: Horizontal(g5)
    c: Coincident(g6,g2)
    c: Coincident(g6,g5)
    c: Vertical(g6)
    c: Horizontal(g7)
    c: Distance(g7) = 105
    c: Coincident(g7,g1)
    c: Block(g3)
    c: Weight(g8) = 1
    c: Equal(g8,g9)
    c: Equal(g8,g10)
    c: InternalAlignment(g8,g11)
    c: InternalAlignment(g9,g11)
    c: InternalAlignment(g10,g11)
    c: InternalAlignment(g12,g11)
    c: InternalAlignment(g13,g11)
    c: Block(g11)
    c: Coincident(g14,g11)
    c: Coincident(g14,g3)
    c: Horizontal(g14)
    c: Block(g15)
    c: Coincident(g16,g11)
    c: Coincident(g16,g15)
    c: Vertical(g16)
    c: Distance(g16) = 14
    c: Coincident(g17,g15)
    c: Block(g18)
    c: Coincident(g19,g18)
    c: Coincident(g20,g7)
    c: Horizontal(g20)
    c: Vertical(g21)
    c: Coincident(g20,g21)
    c: Block(g20)
    c: Block(g21)
    c: Block(g19)
    c: Block(g17)
FEATURE [Part::Extrusion] Extrude044
  Base = -> Sketch053
  Dir = (0,0,1)
  DirMode = 2
  FaceMakerClass = Part::FaceMakerBullseye
  LengthFwd = 72
  LengthRev = 0
  Solid = true
  Symmetric = false
FEATURE [Part::Fillet] Fillet036
  Base = -> Extrude044
  Edges = 1 edges r=2: [Edge41]
